FCSTD DOCUMENT  (FreeCAD 0.21R33668 +7 (Git))
Label: assembly
License: All rights reserved
LicenseURL: http://en.wikipedia.org/wiki/All_rights_reserved
objects: App::Link×21, App::DocumentObjectGroup×2, PartDesign::CoordinateSystem×1, App::FeaturePython×1, Sketcher::SketchObject×1, App::Part×1
note: 2 computed .brp shape members not serialized (recipe doc carries the construction recipe); baked Part::Feature solids carry a one-line shape summary decoded from their .brp
EXTERNAL_REF file=planB.FCStd obj=LCS_0
EXTERNAL_REF file=planB.FCStd obj=main
EXTERNAL_REF file=ES-holder-end.FCStd obj=LCS_0
EXTERNAL_REF file=ES-holder-end.FCStd obj=ES_holder
EXTERNAL_REF file=ES-holder.FCStd obj=LCS_0
EXTERNAL_REF file=ES-holder.FCStd obj=ES_holder
EXTERNAL_REF file=ES-holder-end-other.FCStd obj=LCS_0
EXTERNAL_REF file=ES-holder-end-other.FCStd obj=ES_holder
EXTERNAL_REF file=back-base.FCStd obj=LCS_0
EXTERNAL_REF file=back-base.FCStd obj=back_base
EXTERNAL_REF file=speakerbox.FCStd obj=LCS_0
EXTERNAL_REF file=speakerbox.FCStd obj=speakerbox
EXTERNAL_REF file=L-back.FCStd obj=LCS_0
EXTERNAL_REF file=L-back.FCStd obj=L_back
EXTERNAL_REF file=L-front.FCStd obj=LCS_0
EXTERNAL_REF file=L-front.FCStd obj=L_front
EXTERNAL_REF file=side_front_L.FCStd obj=LCS_0
EXTERNAL_REF file=side_front_L.FCStd obj=side_front_L
EXTERNAL_REF file=L-grip-1.FCStd obj=LCS_0
EXTERNAL_REF file=L-grip-1.FCStd obj=L_grip_1
EXTERNAL_REF file=speakerbox-L.FCStd obj=LCS_0
EXTERNAL_REF file=speakerbox-L.FCStd obj=speakerbox
EXTERNAL_REF file=side_front_R.FCStd obj=LCS_0
EXTERNAL_REF file=side_front_R.FCStd obj=side_front_L
EXTERNAL_REF file=planB.FCStd obj=Spreadsheet
EXTERNAL_REF file=leg1.FCStd obj=LCS_0
EXTERNAL_REF file=leg1.FCStd obj=leg1
EXTERNAL_REF file=speaker.FCStd obj=LCS_0
EXTERNAL_REF file=speaker.FCStd obj=speaker
EXTERNAL_REF file=speaker-enclosure-L.FCStd obj=LCS_0
EXTERNAL_REF file=speaker-enclosure-L.FCStd obj=enc_L
EXTERNAL_REF file=speaker-enclosure-R.FCStd obj=LCS_0
EXTERNAL_REF file=speaker-enclosure-R.FCStd obj=enc_L
EXTERNAL_REF file=speaker-enclosure-lid-R.FCStd obj=LCS_0
EXTERNAL_REF file=speaker-enclosure-lid-R.FCStd obj=enc_lid_L
EXTERNAL_REF file=speaker-enclosure-lid-L.FCStd obj=LCS_0
EXTERNAL_REF file=speaker-enclosure-lid-L.FCStd obj=enc_lid_L
EXTERNAL_REF file=volume knob.FCStd obj=LCS_0
EXTERNAL_REF file=volume knob.FCStd obj=knob

FEATURE [App::DocumentObjectGroup] Parts
FEATURE [PartDesign::CoordinateSystem] LCS_Origin
  AttacherType = Attacher::AttachEngine3D
  MapMode = 2
  Support = -> [X_Axis]
FEATURE [App::DocumentObjectGroup] Constraints
FEATURE [App::FeaturePython] Variables  # WARN: FeaturePython — macro-defined, semantics opaque (R4)
FEATURE [App::Link] planB_main
  AssemblyType = Asm4EE
  AttachedBy = #LCS_0
  AttachedTo = Parent Assembly#LCS_Origin
  LinkedObject = -> <external planB.FCStd>#main
  expr: Placement = LCS_Origin.Placement * AttachmentOffset * planB#LCS_0.Placement ^ -1
FEATURE [App::Link] ES_holder_ES_holder  label="ES_holder_end"
  AssemblyType = Asm4EE
  AttachedBy = #LCS_0
  AttachedTo = planB_main#LCS_0
  AttachmentOffset = pos=(87,5,484) rot=(0,0,1;0rad)
  LinkPlacement = pos=(87,5,484) rot=(0,0,1;0rad)
  LinkedObject = -> <external ES-holder-end.FCStd>#ES_holder
  Placement = pos=(87,5,484) rot=(0,0,1;0rad)
  expr: Placement = planB_main.Placement * planB#LCS_0.Placement * AttachmentOffset * ES_holder_end#LCS_0.Placement ^ -1
FEATURE [App::Link] ES_holder1_ES_holder
  AssemblyType = Asm4EE
  AttachedBy = #LCS_0
  AttachedTo = ES_holder_ES_holder#LCS_0
  AttachmentOffset = pos=(0,0,-133) rot=(0,0,1;0rad)
  LinkPlacement = pos=(87,5,351) rot=(0,0,1;0rad)
  LinkedObject = -> <external ES-holder.FCStd>#ES_holder
  Placement = pos=(87,5,351) rot=(0,0,1;0rad)
  expr: Placement = ES_holder_ES_holder.Placement * ES_holder_end#LCS_0.Placement * AttachmentOffset * ES_holder#LCS_0.Placement ^ -1
FEATURE [App::Link] ES_holder1_ES_holder_2
  AssemblyType = Asm4EE
  AttachedBy = #LCS_0
  AttachedTo = ES_holder1_ES_holder#LCS_0
  AttachmentOffset = pos=(0,0,-133) rot=(0,0,1;0rad)
  LinkPlacement = pos=(87,5,218) rot=(0,0,1;0rad)
  LinkedObject = -> <external ES-holder.FCStd>#ES_holder
  Placement = pos=(87,5,218) rot=(0,0,1;0rad)
  expr: Placement = ES_holder1_ES_holder.Placement * ES_holder#LCS_0.Placement * AttachmentOffset * ES_holder#LCS_0.Placement ^ -1
FEATURE [App::Link] ES_holder_ES_holder_otherend  label="ES_holder_ES_holder-otherend"
  AssemblyType = Asm4EE
  AttachedBy = #LCS_0
  AttachedTo = ES_holder1_ES_holder_2#LCS_0
  AttachmentOffset = pos=(0,0,-133) rot=(0,0,1;0rad)
  LinkPlacement = pos=(87,5,85) rot=(0,0,1;0rad)
  LinkedObject = -> <external ES-holder-end-other.FCStd>#ES_holder
  Placement = pos=(87,5,85) rot=(0,0,1;0rad)
  expr: Placement = ES_holder1_ES_holder_2.Placement * ES_holder#LCS_0.Placement * AttachmentOffset * ES_holder_end_other#LCS_0.Placement ^ -1
FEATURE [App::Link] back_base
  AssemblyType = Part::Link
  AttachedBy = #LCS_0
  AttachedTo = planB_main#LCS_0
  AttachmentOffset = pos=(0,0,0) rot=(1,0,0;4.71239rad)
  LinkPlacement = pos=(0,0,0) rot=(1,0,0;4.71239rad)
  LinkedObject = -> <external back-base.FCStd>#back_base
  Placement = pos=(0,0,0) rot=(1,0,0;4.71239rad)
  SolverId = Asm4EE
  expr: Placement = planB_main.Placement * planB#LCS_0.Placement * AttachmentOffset * back_base#LCS_0.Placement ^ -1
FEATURE [App::Link] speakerbox_speakerbox
  AssemblyType = Asm4EE
  AttachedBy = #LCS_0
  AttachedTo = planB_main#LCS_0
  AttachmentOffset = pos=(0,30,0) rot=(0,0,1;0rad)
  LinkPlacement = pos=(0,30,0) rot=(0,0,1;0rad)
  LinkedObject = -> <external speakerbox.FCStd>#speakerbox
  Placement = pos=(0,30,0) rot=(0,0,1;0rad)
  expr: Placement = planB_main.Placement * planB#LCS_0.Placement * AttachmentOffset * speakerbox#LCS_0.Placement ^ -1
FEATURE [App::Link] L_back_L_back
  AssemblyType = Asm4EE
  AttachedBy = #LCS_0
  AttachedTo = planB_main#LCS_0
  AttachmentOffset = pos=(6.4,99.1,5) rot=(0,0,1;0rad)
  LinkPlacement = pos=(6.4,99.1,5) rot=(0,0,1;0rad)
  LinkedObject = -> <external L-back.FCStd>#L_back
  Placement = pos=(6.4,99.1,5) rot=(0,0,1;0rad)
  expr: Placement = planB_main.Placement * planB#LCS_0.Placement * AttachmentOffset * L_back#LCS_0.Placement ^ -1
FEATURE [App::Link] L_front_L_front
  AssemblyType = Asm4EE
  AttachedBy = #LCS_0
  AttachedTo = planB_main#LCS_0
  AttachmentOffset = pos=(299.2,97,5) rot=(0,0,1;1.5708rad)
  LinkPlacement = pos=(299.2,97,5) rot=(0,0,1;1.5708rad)
  LinkedObject = -> <external L-front.FCStd>#L_front
  Placement = pos=(299.2,97,5) rot=(0,0,1;1.5708rad)
  expr: Placement = planB_main.Placement * planB#LCS_0.Placement * AttachmentOffset * L_front#LCS_0.Placement ^ -1
FEATURE [App::Link] side_front_L_side_front_L
  AssemblyType = Asm4EE
  AttachedBy = #LCS_0
  AttachedTo = planB_main#LCS_0
  AttachmentOffset = pos=(168.6,5,0) rot=(0,0,1;0rad)
  LinkPlacement = pos=(168.6,5,0) rot=(0,0,1;0rad)
  LinkedObject = -> <external side_front_L.FCStd>#side_front_L
  Placement = pos=(168.6,5,0) rot=(0,0,1;0rad)
  expr: Placement = planB_main.Placement * planB#LCS_0.Placement * AttachmentOffset * side_front_L#LCS_0.Placement ^ -1
FEATURE [App::Link] L_grip_1_L_grip_1
  AssemblyType = Asm4EE
  AttachedBy = #LCS_0
  AttachedTo = L_front_L_front#LCS_0
  AttachmentOffset = pos=(-0.4,-0.4,491) rot=(0,0,1;0rad)
  LinkPlacement = pos=(299.6,96.6,496) rot=(0,0,1;1.5708rad)
  LinkedObject = -> <external L-grip-1.FCStd>#L_grip_1
  Placement = pos=(299.6,96.6,496) rot=(0,0,1;1.5708rad)
  expr: Placement = L_front_L_front.Placement * L_front#LCS_0.Placement * AttachmentOffset * L_grip_1#LCS_0.Placement ^ -1
FEATURE [App::Link] L_grip_1_L_grip_2
  AssemblyType = Asm4EE
  AttachedBy = #LCS_0
  AttachedTo = L_back_L_back#LCS_0
  AttachmentOffset = pos=(0,0,491) rot=(0,0,1;0rad)
  LinkPlacement = pos=(6.4,99.1,496) rot=(0,0,1;0rad)
  LinkedObject = -> <external L-grip-1.FCStd>#L_grip_1
  Placement = pos=(6.4,99.1,496) rot=(0,0,1;0rad)
  expr: Placement = L_back_L_back.Placement * L_back#LCS_0.Placement * AttachmentOffset * L_grip_1#LCS_0.Placement ^ -1
FEATURE [App::Link] speakerbox_L_speakerbox_L  label="speakerbox_L_speakerbox-L"
  AssemblyType = Asm4EE
  AttachedBy = #LCS_0
  AttachedTo = planB_main#LCS_0
  AttachmentOffset = pos=(0,30,440) rot=(0,0,1;0rad)
  LinkPlacement = pos=(0,30,440) rot=(0,0,1;0rad)
  LinkedObject = -> <external speakerbox-L.FCStd>#speakerbox
  Placement = pos=(0,30,440) rot=(0,0,1;0rad)
  expr: Placement = planB_main.Placement * planB#LCS_0.Placement * AttachmentOffset * speakerbox_L#LCS_0.Placement ^ -1
FEATURE [App::Link] side_front_R_side_front_L
  AssemblyType = Asm4EE
  AttachedBy = #LCS_0
  AttachedTo = planB_main#LCS_0
  AttachmentOffset = pos=(169,5,484) rot=(0,0,1;0rad)
  LinkPlacement = pos=(169,5,484) rot=(0,0,1;0rad)
  LinkedObject = -> <external side_front_R.FCStd>#side_front_L
  Placement = pos=(169,5,484) rot=(0,0,1;0rad)
  expr: Placement = planB_main.Placement * planB#LCS_0.Placement * AttachmentOffset * side_front_R#LCS_0.Placement ^ -1
FEATURE [Sketcher::SketchObject] Sketch003
  FullyConstrained = false
  MapMode = 5
  Support = -> [XY_Plane]
  expr: Constraints[1] = planB#<<data>>.clearance_m3
  sketch-geometry (38):
    g0: Circle CenterX=3.5 CenterY=-246.571 CenterZ=0 NormalX=0 NormalY=0 NormalZ=1 AngleXU=0 Radius=1.75
    g1: Circle CenterX=3.5 CenterY=-253.429 CenterZ=0 NormalX=0 NormalY=0 NormalZ=1 AngleXU=0 Radius=1.75
    g2: LineSegment StartX=3.5 StartY=-246.571 StartZ=0 EndX=3.5 EndY=-253.429 EndZ=0
    g3: GeomPoint X=3.5 Y=-250 Z=0
    g4: LineSegment StartX=227.2 StartY=-93 StartZ=0 EndX=227.2 EndY=-492 EndZ=0
    g5: LineSegment StartX=227.2 StartY=-93 StartZ=0 EndX=99 EndY=-93 EndZ=0
    g6: LineSegment StartX=99 StartY=-93 StartZ=0 EndX=99 EndY=-492 EndZ=0
    g7: LineSegment StartX=176.6 StartY=-93 StartZ=0 EndX=176.6 EndY=-492 EndZ=0
    g8: LineSegment StartX=144.6 StartY=-93 StartZ=0 EndX=144.6 EndY=-492 EndZ=0
    g9: LineSegment StartX=99 StartY=-492 StartZ=0 EndX=227.2 EndY=-492 EndZ=0
    g10: LineSegment StartX=227.2 StartY=-226 StartZ=0 EndX=99 EndY=-226 EndZ=0
    g11: LineSegment StartX=99 StartY=-359 StartZ=0 EndX=227.2 EndY=-359 EndZ=0
    g12: LineSegment StartX=99 StartY=-492 StartZ=0 EndX=12 EndY=-492 EndZ=0
    g13: LineSegment StartX=70 StartY=-492 StartZ=0 EndX=70 EndY=-8 EndZ=0
    g14: LineSegment StartX=227.2 StartY=-93 StartZ=0 EndX=227.2 EndY=-8 EndZ=0
    g15: LineSegment StartX=227.2 StartY=-8 StartZ=0 EndX=12 EndY=-8 EndZ=0
    g16: LineSegment StartX=12 StartY=-8 StartZ=0 EndX=12 EndY=-492 EndZ=0
    g17: Circle CenterX=227.2 CenterY=-492 CenterZ=0 NormalX=0 NormalY=0 NormalZ=1 AngleXU=0 Radius=3.6145
    g18: Circle CenterX=176.6 CenterY=-492 CenterZ=0 NormalX=0 NormalY=0 NormalZ=1 AngleXU=0 Radius=3.6145
    g19: Circle CenterX=144.6 CenterY=-492 CenterZ=0 NormalX=0 NormalY=0 NormalZ=1 AngleXU=0 Radius=3.6145
    g20: Circle CenterX=99 CenterY=-492 CenterZ=0 NormalX=0 NormalY=0 NormalZ=1 AngleXU=0 Radius=3.6145
    g21: Circle CenterX=70 CenterY=-492 CenterZ=0 NormalX=0 NormalY=0 NormalZ=1 AngleXU=0 Radius=3.6145
    g22: Circle CenterX=12 CenterY=-492 CenterZ=0 NormalX=0 NormalY=0 NormalZ=1 AngleXU=0 Radius=3.6145
    g23: Circle CenterX=99 CenterY=-359 CenterZ=0 NormalX=0 NormalY=0 NormalZ=1 AngleXU=0 Radius=3.6145
    g24: Circle CenterX=144.6 CenterY=-359 CenterZ=0 NormalX=0 NormalY=0 NormalZ=1 AngleXU=0 Radius=3.6145
    g25: Circle CenterX=176.6 CenterY=-359 CenterZ=0 NormalX=0 NormalY=0 NormalZ=1 AngleXU=0 Radius=3.6145
    g26: Circle CenterX=227.2 CenterY=-359 CenterZ=0 NormalX=0 NormalY=0 NormalZ=1 AngleXU=0 Radius=3.6145
    g27: Circle CenterX=227.2 CenterY=-226 CenterZ=0 NormalX=0 NormalY=0 NormalZ=1 AngleXU=0 Radius=3.6145
    g28: Circle CenterX=99 CenterY=-226 CenterZ=0 NormalX=0 NormalY=0 NormalZ=1 AngleXU=0 Radius=3.6145
    g29: Circle CenterX=144.6 CenterY=-226 CenterZ=0 NormalX=0 NormalY=0 NormalZ=1 AngleXU=0 Radius=3.6145
    g30: Circle CenterX=176.6 CenterY=-226 CenterZ=0 NormalX=0 NormalY=0 NormalZ=1 AngleXU=0 Radius=3.6145
    g31: Circle CenterX=176.6 CenterY=-93 CenterZ=0 NormalX=0 NormalY=0 NormalZ=1 AngleXU=0 Radius=3.6145
    g32: Circle CenterX=144.6 CenterY=-93 CenterZ=0 NormalX=0 NormalY=0 NormalZ=1 AngleXU=0 Radius=3.6145
    g33: Circle CenterX=99 CenterY=-93 CenterZ=0 NormalX=0 NormalY=0 NormalZ=1 AngleXU=0 Radius=3.6145
    g34: Circle CenterX=227.2 CenterY=-93 CenterZ=0 NormalX=0 NormalY=0 NormalZ=1 AngleXU=0 Radius=3.6145
    g35: Circle CenterX=227.2 CenterY=-8 CenterZ=0 NormalX=0 NormalY=0 NormalZ=1 AngleXU=0 Radius=3.6145
    g36: Circle CenterX=70 CenterY=-8 CenterZ=0 NormalX=0 NormalY=0 NormalZ=1 AngleXU=0 Radius=3.6145
    g37: Circle CenterX=12 CenterY=-8 CenterZ=0 NormalX=0 NormalY=0 NormalZ=1 AngleXU=0 Radius=3.6145
  constraints (96):
    c: Equal(g1,g0)
    c: Diameter(g0) = 3.5
    c: Coincident(g2,g0)
    c: Coincident(g2,g1)
    c: Vertical(g2)
    c: Symmetric(g1,g0,g3)
    c: DistanceX(g3) = 3.5
    c: DistanceY(g3) = -250
    c: Vertical(g4)
    c: Coincident(g5,g4)
    c: Horizontal(g5)
    c: Coincident(g6,g5)
    c: Vertical(g6)
    c: PointOnObject(g7,g5)
    c: Vertical(g7)
    c: PointOnObject(g8,g5)
    c: Vertical(g8)
    c: Coincident(g9,g6)
    c: Coincident(g9,g4)
    c: Horizontal(g9)
    c: PointOnObject(g7,g9)
    c: PointOnObject(g8,g9)
    c: PointOnObject(g10,g4)
    c: PointOnObject(g10,g6)
    c: Horizontal(g10)
    c: PointOnObject(g11,g6)
    c: PointOnObject(g11,g4)
    c: Horizontal(g11)
    c: Distance(g11,g9) = 133
    c: Distance(g11,g10) = 133
    c: Distance(g10,g5) = 133
    c: DistanceX(g4) = 227.2
    c: DistanceY(g4) = -93
    c: DistanceX(g7) = 176.6
    c: DistanceX(g8) = 144.6
    c: DistanceX(g5) = 99
    c: Horizontal(g12)
    c: PointOnObject(g13,g12)
    c: Vertical(g13)
    c: Vertical(g14)
    c: Coincident(g4,g14)
    c: Horizontal(g15)
    c: Vertical(g16)
    c: Coincident(g12,g16)
    c: Coincident(g15,g16)
    c: PointOnObject(g13,g15)
    c: Coincident(g15,g14)
    c: DistanceY(g14) = -8
    c: DistanceX(g15) = 12
    c: DistanceX(g13) = 70
    c: Coincident(g12,g6)
    c: Coincident(g17,g4)
    c: Coincident(g18,g7)
    c: Coincident(g19,g8)
    c: Coincident(g20,g6)
    c: Coincident(g21,g13)
    c: Coincident(g22,g12)
    c: Coincident(g23,g11)
    c: PointOnObject(g24,g8)
    c: PointOnObject(g25,g7)
    c: Coincident(g26,g11)
    c: Coincident(g27,g10)
    c: Coincident(g28,g10)
    c: PointOnObject(g29,g8)
    c: PointOnObject(g30,g7)
    c: Coincident(g31,g7)
    c: Coincident(g32,g8)
    c: Coincident(g33,g5)
    c: Coincident(g34,g4)
    c: Coincident(g35,g14)
    c: Coincident(g36,g13)
    c: Coincident(g37,g15)
    c: Equal(g35,g36)
    c: Equal(g36,g37)
    c: Equal(g37,g33)
    c: Equal(g33,g32)
    c: Equal(g32,g31)
    c: Equal(g31,g34)
    c: Equal(g34,g27)
    c: Equal(g27,g28)
    c: Equal(g28,g29)
    c: Equal(g29,g30)
    c: Equal(g30,g26)
    c: Equal(g26,g25)
    c: Equal(g25,g24)
    c: Equal(g24,g23)
    c: Equal(g23,g17)
    c: Equal(g17,g18)
    c: Equal(g18,g19)
    c: Equal(g19,g20)
    c: Equal(g20,g21)
    c: Equal(g21,g22)
    c: PointOnObject(g25,g11)
    c: PointOnObject(g24,g11)
    c: PointOnObject(g29,g10)
    c: PointOnObject(g30,g10)
FEATURE [App::Link] leg1_leg1
  AssemblyType = Asm4EE
  AttachedBy = #LCS_0
  AttachedTo = planB_main#LCS_0
  AttachmentOffset = pos=(82,12.5,30) rot=(0.707107,0,0.707107;3.14159rad)
  LinkPlacement = pos=(82,12.5,30) rot=(0.707107,0,0.707107;3.14159rad)
  LinkedObject = -> <external leg1.FCStd>#leg1
  Placement = pos=(82,12.5,30) rot=(0.707107,0,0.707107;3.14159rad)
  expr: Placement = planB_main.Placement * planB#LCS_0.Placement * AttachmentOffset * leg1#LCS_0.Placement ^ -1
FEATURE [App::Link] speaker_speaker
  AssemblyType = Asm4EE
  AttachedBy = #LCS_0
  AttachedTo = speakerbox_L_speakerbox_L#LCS_0
  AttachmentOffset = pos=(107,87,27.5) rot=(0.57735,-0.57735,0.57735;2.0944rad)
  LinkPlacement = pos=(107,117,467.5) rot=(0.57735,-0.57735,0.57735;2.0944rad)
  LinkedObject = -> <external speaker.FCStd>#speaker
  Placement = pos=(107,117,467.5) rot=(0.57735,-0.57735,0.57735;2.0944rad)
  expr: Placement = speakerbox_L_speakerbox_L.Placement * speakerbox_L#LCS_0.Placement * AttachmentOffset * speaker#LCS_0.Placement ^ -1
FEATURE [App::Link] speaker_enclosure_L_enc_L
  AssemblyType = Asm4EE
  AttachedBy = #LCS_0
  AttachedTo = speakerbox_L_speakerbox_L#LCS_0
  AttachmentOffset = pos=(147.3,93,0) rot=(0.57735,-0.57735,0.57735;2.0944rad)
  LinkPlacement = pos=(147.3,123,440) rot=(0.57735,-0.57735,0.57735;2.0944rad)
  LinkedObject = -> <external speaker-enclosure-L.FCStd>#enc_L
  Placement = pos=(147.3,123,440) rot=(0.57735,-0.57735,0.57735;2.0944rad)
  expr: Placement = speakerbox_L_speakerbox_L.Placement * speakerbox_L#LCS_0.Placement * AttachmentOffset * speaker_enclosure_L#LCS_0.Placement ^ -1
FEATURE [App::Link] speaker_enclosure_R_enc_R
  AssemblyType = Asm4EE
  AttachedBy = #LCS_0
  AttachedTo = speakerbox_speakerbox#LCS_0
  AttachmentOffset = pos=(147.3,94,5) rot=(0.57735,-0.57735,0.57735;2.0944rad)
  LinkPlacement = pos=(147.3,124,5) rot=(0.57735,-0.57735,0.57735;2.0944rad)
  LinkedObject = -> <external speaker-enclosure-R.FCStd>#enc_L
  Placement = pos=(147.3,124,5) rot=(0.57735,-0.57735,0.57735;2.0944rad)
  expr: Placement = speakerbox_speakerbox.Placement * speakerbox#LCS_0.Placement * AttachmentOffset * speaker_enclosure_R#LCS_0.Placement ^ -1
FEATURE [App::Link] speaker_enclosure_lid_L_enc_lid_R
  AssemblyType = Asm4EE
  AttachedBy = #LCS_0
  AttachedTo = speaker_enclosure_R_enc_R#LCS_0
  LinkPlacement = pos=(147.3,124,5) rot=(0.57735,-0.57735,0.57735;2.0944rad)
  LinkedObject = -> <external speaker-enclosure-lid-R.FCStd>#enc_lid_L
  Placement = pos=(147.3,124,5) rot=(0.57735,-0.57735,0.57735;2.0944rad)
  expr: Placement = speaker_enclosure_R_enc_R.Placement * speaker_enclosure_R#LCS_0.Placement * AttachmentOffset * speaker_enclosure_lid_R#LCS_0.Placement ^ -1
FEATURE [App::Link] speaker_enclosure_lid_L1_enc_lid__L
  AssemblyType = Asm4EE
  AttachedBy = #LCS_0
  AttachedTo = speaker_enclosure_L_enc_L#LCS_0
  LinkPlacement = pos=(147.3,123,440) rot=(0.57735,-0.57735,0.57735;2.0944rad)
  LinkedObject = -> <external speaker-enclosure-lid-L.FCStd>#enc_lid_L
  Placement = pos=(147.3,123,440) rot=(0.57735,-0.57735,0.57735;2.0944rad)
  expr: Placement = speaker_enclosure_L_enc_L.Placement * speaker_enclosure_L#LCS_0.Placement * AttachmentOffset * speaker_enclosure_lid_L#LCS_0.Placement ^ -1
FEATURE [App::Link] volume_knob_knob001
  AssemblyType = Asm4EE
  AttachedBy = #LCS_0
  AttachedTo = speaker_enclosure_lid_L1_enc_lid__L#LCS_0
  AttachmentOffset = pos=(27.5,112.3,0) rot=(0,0,1;0rad)
  LinkPlacement = pos=(35,123,467.5) rot=(0.57735,-0.57735,0.57735;2.0944rad)
  LinkedObject = -> <external volume knob.FCStd>#knob
  Placement = pos=(35,123,467.5) rot=(0.57735,-0.57735,0.57735;2.0944rad)
  expr: Placement = speaker_enclosure_lid_L1_enc_lid__L.Placement * speaker_enclosure_lid_L#LCS_0.Placement * AttachmentOffset * volume_knob#LCS_0.Placement ^ -1
FEATURE [App::Part] Model
  Configuration = 0
  Group = -> [LCS_Origin,Constraints,Variables,planB_main,ES_holder_ES_holder,ES_holder1_ES_holder,ES_holder1_ES_holder_2,ES_holder_ES_holder_otherend,back_base,speakerbox_speakerbox,L_back_L_back,L_front_L_front,side_front_L_side_front_L,L_grip_1_L_grip_1,L_grip_1_L_grip_2,speakerbox_L_speakerbox_L,side_front_R_side_front_L,leg1_leg1,speaker_speaker,speaker_enclosure_L_enc_L,speaker_enclosure_R_enc_R,+3 more]
  Origin = -> Origin
  Type = Assembly4 Model

RESOLVED EXTERNAL PARTS (link-assembly join: the EXTERNAL_REF files above that resolve inside this repo's crawl, each included once):
---- part ES-holder-end-other.FCStd = doc fcstd_7b380cd65d5b ----
FCSTD DOCUMENT  (FreeCAD 0.21R33668 +7 (Git))
Label: ES-holder-end-other
License: All rights reserved
LicenseURL: http://en.wikipedia.org/wiki/All_rights_reserved
objects: Sketcher::SketchObject×7, PartDesign::Pocket×4, PartDesign::Pad×3, PartDesign::CoordinateSystem×1, PartDesign::Plane×1, PartDesign::Chamfer×1, PartDesign::Body×1, App::Part×1
note: 26 computed .brp shape members not serialized (recipe doc carries the construction recipe); baked Part::Feature solids carry a one-line shape summary decoded from their .brp
EXTERNAL_REF file=planB.FCStd obj=Spreadsheet

FEATURE [Sketcher::SketchObject] Sketch
  FullyConstrained = false
  MapMode = 5
  Support = -> [XY_Plane]
  expr: Constraints[33] = <<planB>>#<<data>>.es3_d + 1
  expr: Constraints[34] = <<planB>>#<<data>>.es6_d
  sketch-geometry (19):
    g0: LineSegment StartX=0 StartY=0 StartZ=0 EndX=0 EndY=43 EndZ=0
    g1: LineSegment StartX=152.2 StartY=31 StartZ=0 EndX=152.2 EndY=0 EndZ=0
    g2: LineSegment StartX=152.2 StartY=0 StartZ=0 EndX=0 EndY=0 EndZ=0
    g3: LineSegment StartX=22.6 StartY=-1.74507e-05 StartZ=0 EndX=20 EndY=-1.74507e-05 EndZ=0
    g4: LineSegment StartX=20 StartY=-1.74507e-05 StartZ=0 EndX=20 EndY=43 EndZ=0
    g5: LineSegment StartX=20 StartY=43 StartZ=0 EndX=22.6 EndY=43 EndZ=0
    g6: LineSegment StartX=22.6 StartY=43 StartZ=0 EndX=22.6 EndY=-1.74507e-05 EndZ=0
    g7: LineSegment StartX=132.2 StartY=0 StartZ=0 EndX=129.6 EndY=0 EndZ=0
    g8: LineSegment StartX=129.6 StartY=0 StartZ=0 EndX=129.6 EndY=31 EndZ=0
    g9: LineSegment StartX=129.6 StartY=31 StartZ=0 EndX=132.2 EndY=31 EndZ=0
    g10: LineSegment StartX=132.2 StartY=31 StartZ=0 EndX=132.2 EndY=0 EndZ=0
    g11: LineSegment StartX=76.6 StartY=43 StartZ=0 EndX=76.6 EndY=31 EndZ=0
    g12: LineSegment StartX=76.6 StartY=31 StartZ=0 EndX=152.2 EndY=31 EndZ=0
    g13: LineSegment StartX=27.6 StartY=43 StartZ=0 EndX=27.6 EndY=28 EndZ=0
    g14: LineSegment StartX=27.6 StartY=28 StartZ=0 EndX=47.6 EndY=28 EndZ=0
    g15: LineSegment StartX=47.6 StartY=28 StartZ=0 EndX=47.6 EndY=43 EndZ=0
    g16: LineSegment StartX=0 StartY=43 StartZ=0 EndX=27.6 EndY=43 EndZ=0
    g17: LineSegment StartX=27.6 StartY=43 StartZ=0 EndX=47.6 EndY=43 EndZ=0
    g18: LineSegment StartX=47.6 StartY=43 StartZ=0 EndX=76.6 EndY=43 EndZ=0
  constraints (54):
    c: Coincident(g-1,g0)
    c: PointOnObject(g0,g-2)
    c: Coincident(g0,g16)
    c: Coincident(g12,g1)
    c: PointOnObject(g1,g-1)
    c: Vertical(g1)
    c: Coincident(g1,g2)
    c: Coincident(g3,g4)
    c: Coincident(g4,g5)
    c: Coincident(g5,g6)
    c: Coincident(g6,g3)
    c: Horizontal(g3)
    c: Horizontal(g5)
    c: Vertical(g4)
    c: Vertical(g6)
    c: Coincident(g7,g8)
    c: Coincident(g8,g9)
    c: Coincident(g9,g10)
    c: Coincident(g10,g7)
    c: Horizontal(g7)
    c: Horizontal(g9)
    c: Vertical(g8)
    c: Vertical(g10)
    c: PointOnObject(g7,g2)
    c: Equal(g3,g7)
    c: Distance(g3,g4) = 2.6
    c: Coincident(g18,g11)
    c: Coincident(g11,g12)
    c: Horizontal(g12)
    c: PointOnObject(g8,g12)
    c: Vertical(g11)
    c: Distance(g0) = 43
    c: Distance(g1) = 31
    c: Distance(g5,g11) = 54
    c: Distance(g11,g8) = 53
    c: Distance(g7,g1) = 20
    c: Distance(g3,g0) = 20
    c: Coincident(g2,g0)
    c: Coincident(g13,g14)
    c: Horizontal(g14)
    c: Coincident(g14,g15)
    c: Vertical(g15)
    c: Coincident(g16,g17)
    c: Horizontal(g16)
    c: PointOnObject(g4,g16)
    c: Coincident(g17,g18)
    c: Horizontal(g17)
    c: Horizontal(g18)
    c: Coincident(g17,g15)
    c: Coincident(g16,g13)
    c: Vertical(g13)
    c: Distance(g13) = 15
    c: Distance(g14) = 20
    c: Distance(g5,g13) = 5
FEATURE [PartDesign::Pad] Pad
  Direction = (0,0,1)
  Length = 16
  Length2 = 10
  Profile = -> Sketch
  ReferenceAxis = -> Sketch [N_Axis]
  Type = 0
FEATURE [Sketcher::SketchObject] Sketch001
  FullyConstrained = false
  MapMode = 5
  Placement = pos=(0,0,0) rot=(1,0,0;1.5708rad)
  Support = -> [XZ_Plane]
  expr: Constraints[52] = <<planB>>#<<data>>.es6_d + 1 + <<planB>>#<<data>>.es3_d
  expr: Constraints[60] = <<planB>>#<<data>>.insert_diameter
  expr: Constraints[61] = <<planB>>#<<data>>.insert_d + 5
  sketch-geometry (27):
    g0: LineSegment StartX=20 StartY=0 StartZ=0 EndX=20 EndY=17.2745 EndZ=0
    g1: LineSegment StartX=132.2 StartY=0 StartZ=0 EndX=132.2 EndY=26.3444 EndZ=0
    g2: LineSegment StartX=20 StartY=0 StartZ=0 EndX=22.6 EndY=0 EndZ=0
    g3: LineSegment StartX=22.6 StartY=0 StartZ=0 EndX=22.6 EndY=6 EndZ=0
    g4: LineSegment StartX=22.6 StartY=6 StartZ=0 EndX=20 EndY=6 EndZ=0
    g5: LineSegment StartX=20 StartY=6 StartZ=0 EndX=20 EndY=0 EndZ=0
    g6: LineSegment StartX=20 StartY=10 StartZ=0 EndX=22.6 EndY=10 EndZ=0
    g7: LineSegment StartX=22.6 StartY=10 StartZ=0 EndX=22.6 EndY=16 EndZ=0
    g8: LineSegment StartX=22.6 StartY=16 StartZ=0 EndX=20 EndY=16 EndZ=0
    g9: LineSegment StartX=20 StartY=16 StartZ=0 EndX=20 EndY=10 EndZ=0
    g10: LineSegment StartX=132.2 StartY=10 StartZ=0 EndX=129.6 EndY=10 EndZ=0
    g11: LineSegment StartX=129.6 StartY=10 StartZ=0 EndX=129.6 EndY=16 EndZ=0
    g12: LineSegment StartX=129.6 StartY=16 StartZ=0 EndX=132.2 EndY=16 EndZ=0
    g13: LineSegment StartX=132.2 StartY=16 StartZ=0 EndX=132.2 EndY=10 EndZ=0
    g14: LineSegment StartX=132.2 StartY=6 StartZ=0 EndX=129.6 EndY=6 EndZ=0
    g15: LineSegment StartX=129.6 StartY=6 StartZ=0 EndX=129.6 EndY=0 EndZ=0
    g16: LineSegment StartX=129.6 StartY=0 StartZ=0 EndX=132.2 EndY=0 EndZ=0
    g17: LineSegment StartX=132.2 StartY=0 StartZ=0 EndX=132.2 EndY=6 EndZ=0
    g18: Circle CenterX=12 CenterY=8 CenterZ=0 NormalX=0 NormalY=0 NormalZ=1 AngleXU=0 Radius=2.15
    g19: Circle CenterX=89.6 CenterY=8 CenterZ=0 NormalX=0 NormalY=0 NormalZ=1 AngleXU=0 Radius=2.15
    g20: Circle CenterX=140.2 CenterY=8 CenterZ=0 NormalX=0 NormalY=0 NormalZ=1 AngleXU=0 Radius=2.15
    g21: LineSegment StartX=12 StartY=8 StartZ=0 EndX=140.2 EndY=8 EndZ=0
    g22: Circle CenterX=57.6 CenterY=8 CenterZ=0 NormalX=0 NormalY=0 NormalZ=1 AngleXU=0 Radius=2.15
    g23: Circle CenterX=12 CenterY=-77 CenterZ=0 NormalX=0 NormalY=0 NormalZ=1 AngleXU=0 Radius=2.15
    g24: Circle CenterX=140.2 CenterY=-77 CenterZ=0 NormalX=0 NormalY=0 NormalZ=1 AngleXU=0 Radius=2.15
    g25: LineSegment StartX=12 StartY=-77 StartZ=0 EndX=140.2 EndY=-77 EndZ=0
    g26: LineSegment StartX=12 StartY=8 StartZ=0 EndX=12 EndY=-77 EndZ=0
  constraints (77):
    c: PointOnObject(g0,g-1)
    c: Vertical(g0)
    c: PointOnObject(g1,g-1)
    c: Vertical(g1)
    c: DistanceX(g0) = 20
    c: Coincident(g2,g3)
    c: Coincident(g3,g4)
    c: Coincident(g4,g5)
    c: Coincident(g5,g2)
    c: Horizontal(g2)
    c: Horizontal(g4)
    c: Vertical(g3)
    c: Vertical(g5)
    c: Coincident(g2,g0)
    c: Coincident(g6,g7)
    c: Coincident(g7,g8)
    c: Coincident(g8,g9)
    c: Coincident(g9,g6)
    c: Horizontal(g6)
    c: Horizontal(g8)
    c: Vertical(g7)
    c: Vertical(g9)
    c: PointOnObject(g6,g0)
    c: Coincident(g10,g11)
    c: Coincident(g11,g12)
    c: Coincident(g12,g13)
    c: Coincident(g13,g10)
    c: Horizontal(g10)
    c: Horizontal(g12)
    c: Vertical(g11)
    c: Vertical(g13)
    c: PointOnObject(g10,g1)
    c: Coincident(g14,g15)
    c: Coincident(g15,g16)
    c: Coincident(g16,g17)
    c: Coincident(g17,g14)
    c: Horizontal(g14)
    c: Horizontal(g16)
    c: Vertical(g15)
    c: Vertical(g17)
    c: PointOnObject(g14,g1)
    c: PointOnObject(g15,g-1)
    c: Equal(g2,g16)
    c: Equal(g16,g10)
    c: Equal(g10,g8)
    c: Equal(g3,g7)
    c: Equal(g7,g11)
    c: Equal(g11,g15)
    c: Distance(g16) = 2.6
    c: Distance(g11) = 6
    c: Distance(g14,g10) = 4
    c: Distance(g4,g6) = 4
    c: Distance(g7,g11) = 107
    c: Coincident(g21,g18)
    c: Coincident(g21,g20)
    c: Horizontal(g21)
    c: PointOnObject(g19,g21)
    c: Equal(g20,g19)
    c: Equal(g19,g18)
    c: DistanceY(g18) = 8
    c: Diameter(g18) = 4.3
    c: DistanceX(g18) = 12
    c: PointOnObject(g22,g21)
    c: Equal(g22,g19)
    c: Distance(g22,g3) = 35
    c: Distance(g19,g11) = 40
    c: Distance(g20,g13) = 8
    c: Equal(g24,g23)
    c: Equal(g23,g22)
    c: Coincident(g25,g23)
    c: Coincident(g25,g24)
    c: Horizontal(g25)
    c: Equal(g21,g25)
    c: Coincident(g26,g18)
    c: Coincident(g26,g23)
    c: Vertical(g26)
    c: Distance(g26) = 85
FEATURE [PartDesign::CoordinateSystem] LCS_0
  AttacherType = Attacher::AttachEngine3D
  MapMode = 2
  Support = -> [X_Axis001]
FEATURE [Sketcher::SketchObject] Sketch002
  FullyConstrained = true
  MapMode = 5
  Placement = pos=(0,0,0) rot=(0.57735,0.57735,0.57735;2.0944rad)
  Support = -> [YZ_Plane]
  expr: Constraints[0] = <<planB>>#<<data>>.insert_d + 5
  expr: Constraints[2] = <<planB>>#<<data>>.insert_diameter
  sketch-geometry (1):
    g0: Circle CenterX=12 CenterY=8 CenterZ=0 NormalX=0 NormalY=0 NormalZ=1 AngleXU=0 Radius=2.15
  constraints (3):
    c: DistanceX(g0) = 12
    c: DistanceY(g0) = 8
    c: Diameter(g0) = 4.3
FEATURE [PartDesign::Pocket] Pocket001
  BaseFeature = -> Pad
  Direction = (-1,2e-16,-3e-16)
  Length = 8
  Length2 = 5
  Profile = -> Sketch002
  ReferenceAxis = -> Sketch002 [N_Axis]
  Reversed = true
  Type = 0
  expr: Length = <<planB>>#<<data>>.insert_d + 1
FEATURE [PartDesign::Plane] DatumPlane
  AttachmentOffset = pos=(0,0,152.2) rot=(0,0,1;0rad)
  Length = 60
  MapMode = 5
  Placement = pos=(152.2,-3.38e-14,3.38e-14) rot=(0.57735,0.57735,0.57735;2.0944rad)
  ResizeMode = 0
  Support = -> [YZ_Plane]
  Width = 60
FEATURE [Sketcher::SketchObject] Sketch003
  FullyConstrained = true
  MapMode = 5
  Placement = pos=(152.2,-3.38e-14,3.38e-14) rot=(0.57735,0.57735,0.57735;2.0944rad)
  Support = -> [DatumPlane]
  expr: Constraints[0] = <<planB>>#<<data>>.insert_diameter
  expr: Constraints[1] = <<planB>>#<<data>>.insert_d + 5
  sketch-geometry (1):
    g0: Circle CenterX=12 CenterY=8 CenterZ=0 NormalX=0 NormalY=0 NormalZ=1 AngleXU=0 Radius=2.15
  constraints (3):
    c: Diameter(g0) = 4.3
    c: DistanceX(g0) = 12
    c: DistanceY(g0) = 8
FEATURE [PartDesign::Pocket] Pocket002
  BaseFeature = -> Pocket001
  Direction = (-1,1e-16,-1e-16)
  Length = 8
  Length2 = 5
  Profile = -> Sketch003
  ReferenceAxis = -> Sketch003 [N_Axis]
  Type = 0
  expr: Length = <<planB>>#<<data>>.insert_d + 1
FEATURE [Sketcher::SketchObject] Sketch004
  FullyConstrained = false
  MapMode = 5
  Placement = pos=(0,0,0) rot=(1,0,0;1.5708rad)
  Support = -> [XZ_Plane]
  sketch-geometry (25):
    g0: LineSegment StartX=128 StartY=0 StartZ=0 EndX=152.2 EndY=0 EndZ=0
    g1: LineSegment StartX=128 StartY=-65 StartZ=0 EndX=128 EndY=0 EndZ=0
    g2: LineSegment StartX=0 StartY=0 StartZ=0 EndX=12 EndY=0 EndZ=0
    g3: LineSegment StartX=12 StartY=0 StartZ=0 EndX=12 EndY=-65 EndZ=0
    g4: LineSegment StartX=0 StartY=-65 StartZ=0 EndX=0 EndY=0 EndZ=0
    g5: LineSegment StartX=0 StartY=-65 StartZ=0 EndX=0 EndY=-85 EndZ=0
    g6: LineSegment StartX=0 StartY=-85 StartZ=0 EndX=12 EndY=-85 EndZ=0
    g7: LineSegment StartX=12 StartY=-85 StartZ=0 EndX=12 EndY=-68 EndZ=0
    g8: LineSegment StartX=12 StartY=-68 StartZ=0 EndX=5.5 EndY=-68 EndZ=0
    g9: LineSegment StartX=5.5 StartY=-68 StartZ=0 EndX=5.5 EndY=-65 EndZ=0
    g10: LineSegment StartX=134.5 StartY=-65 StartZ=0 EndX=134.5 EndY=-68 EndZ=0
    g11: LineSegment StartX=134.5 StartY=-68 StartZ=0 EndX=128 EndY=-68 EndZ=0
    g12: LineSegment StartX=128 StartY=-68 StartZ=0 EndX=128 EndY=-85 EndZ=0
    g13: LineSegment StartX=128 StartY=-85 StartZ=0 EndX=152.2 EndY=-85 EndZ=0
    g14: LineSegment StartX=152.2 StartY=-85 StartZ=0 EndX=152.2 EndY=-69 EndZ=0
    g15: LineSegment StartX=12 StartY=-65 StartZ=0 EndX=5.5 EndY=-65 EndZ=0
    g16: LineSegment StartX=5.5 StartY=-65 StartZ=0 EndX=0 EndY=-65 EndZ=0
    g17: LineSegment StartX=134.5 StartY=-65 StartZ=0 EndX=128 EndY=-65 EndZ=0
    g18: LineSegment StartX=152.2 StartY=0 StartZ=0 EndX=152.2 EndY=-5 EndZ=0
    g19: LineSegment StartX=152.2 StartY=-5 StartZ=0 EndX=152.2 EndY=-69 EndZ=0
    g20: LineSegment StartX=152.2 StartY=-5 StartZ=0 EndX=133 EndY=-5 EndZ=0
    g21: LineSegment StartX=133 StartY=-5 StartZ=0 EndX=133 EndY=-60 EndZ=0
    g22: LineSegment StartX=133 StartY=-60 StartZ=0 EndX=139.92 EndY=-60 EndZ=0
    g23: LineSegment StartX=139.92 StartY=-60 StartZ=0 EndX=139.92 EndY=-69 EndZ=0
    g24: LineSegment StartX=139.92 StartY=-69 StartZ=0 EndX=152.2 EndY=-69 EndZ=0
  constraints (71):
    c: Coincident(g0,g18)
    c: Coincident(g17,g1)
    c: Coincident(g1,g0)
    c: Horizontal(g0)
    c: Vertical(g1)
    c: PointOnObject(g0,g-1)
    c: Coincident(g2,g3)
    c: Coincident(g3,g15)
    c: Coincident(g16,g4)
    c: Coincident(g4,g2)
    c: Horizontal(g2)
    c: Vertical(g3)
    c: Vertical(g4)
    c: Equal(g3,g1)
    c: Distance(g2,g1) = 116
    c: DistanceX(g2,g2) = 12
    c: Coincident(g2,g-1)
    c: Coincident(g16,g5)
    c: Vertical(g5)
    c: Coincident(g5,g6)
    c: Horizontal(g6)
    c: Coincident(g6,g7)
    c: Vertical(g7)
    c: Coincident(g7,g8)
    c: Horizontal(g8)
    c: Coincident(g8,g9)
    c: Vertical(g10)
    c: Coincident(g10,g11)
    c: Horizontal(g11)
    c: Coincident(g11,g12)
    c: Vertical(g12)
    c: Coincident(g12,g13)
    c: Horizontal(g13)
    c: Coincident(g13,g14)
    c: Vertical(g14)
    c: Vertical(g9)
    c: Coincident(g15,g16)
    c: Horizontal(g15)
    c: Horizontal(g16)
    c: Horizontal(g17)
    c: Coincident(g17,g10)
    c: Coincident(g9,g15)
    c: Equal(g9,g10)
    c: Equal(g17,g15)
    c: Equal(g7,g12)
    c: Distance(g9) = 3
    c: PointOnObject(g3,g7)
    c: DistanceY(g7,g7) = 17
    c: Distance(g15) = 6.5
    c: PointOnObject(g11,g1)
    c: DistanceX(g0) = 152.2
    c: Vertical(g18)
    c: Vertical(g19)
    c: Horizontal(g20)
    c: Coincident(g20,g21)
    c: Vertical(g21)
    c: Coincident(g21,g22)
    c: Horizontal(g22)
    c: Distance(g20,g1) = 5
    c: DistanceY(g4,g4) = 65
    c: Coincident(g22,g23)
    c: Vertical(g23)
    c: Coincident(g23,g24)
    c: Coincident(g24,g14)
    c: Horizontal(g24)
    c: Coincident(g19,g14)
    c: DistanceY(g18,g18) = 5
    c: Distance(g21,g17) = 5
    c: Coincident(g20,g19)
    c: Coincident(g18,g20)
    c: DistanceY(g14,g14) = 16
FEATURE [PartDesign::Pad] Pad001
  BaseFeature = -> Pocket002
  Direction = (0,-1,-2e-16)
  Length = 62
  Length2 = 10
  Profile = -> Sketch004
  ReferenceAxis = -> Sketch004 [N_Axis]
  Reversed = true
  Type = 0
FEATURE [Sketcher::SketchObject] Sketch005
  FullyConstrained = false
  MapMode = 5
  Support = -> [XY_Plane]
  expr: Constraints[35] = <<planB>>#<<data>>.es3_d + 1
  expr: Constraints[36] = <<planB>>#<<data>>.es6_d
  sketch-geometry (18):
    g0: LineSegment StartX=0 StartY=0 StartZ=0 EndX=0 EndY=43 EndZ=0
    g1: LineSegment StartX=152.2 StartY=31 StartZ=0 EndX=152.2 EndY=0 EndZ=0
    g2: LineSegment StartX=152.2 StartY=0 StartZ=0 EndX=0 EndY=0 EndZ=0
    g3: LineSegment StartX=22.6 StartY=0 StartZ=0 EndX=20 EndY=0 EndZ=0
    g4: LineSegment StartX=20 StartY=0 StartZ=0 EndX=20 EndY=43 EndZ=0
    g5: LineSegment StartX=20 StartY=43 StartZ=0 EndX=22.6 EndY=43 EndZ=0
    g6: LineSegment StartX=22.6 StartY=43 StartZ=0 EndX=22.6 EndY=0 EndZ=0
    g7: LineSegment StartX=132.2 StartY=0 StartZ=0 EndX=129.6 EndY=0 EndZ=0
    g8: LineSegment StartX=129.6 StartY=0 StartZ=0 EndX=129.6 EndY=31 EndZ=0
    g9: LineSegment StartX=129.6 StartY=31 StartZ=0 EndX=132.2 EndY=31 EndZ=0
    g10: LineSegment StartX=132.2 StartY=31 StartZ=0 EndX=132.2 EndY=0 EndZ=0
    g11: LineSegment StartX=0 StartY=43 StartZ=0 EndX=76.6 EndY=43 EndZ=0
    g12: LineSegment StartX=76.6 StartY=43 StartZ=0 EndX=76.6 EndY=31 EndZ=0
    g13: LineSegment StartX=76.6 StartY=31 StartZ=0 EndX=152.2 EndY=31 EndZ=0
    g14: LineSegment StartX=-256.513 StartY=459.686 StartZ=0 EndX=467.29 EndY=459.686 EndZ=0
    g15: LineSegment StartX=467.29 StartY=459.686 StartZ=0 EndX=467.29 EndY=-198.667 EndZ=0
    g16: LineSegment StartX=467.29 StartY=-198.667 StartZ=0 EndX=-256.513 EndY=-198.667 EndZ=0
    g17: LineSegment StartX=-256.513 StartY=-198.667 StartZ=0 EndX=-256.513 EndY=459.686 EndZ=0
  constraints (48):
    c: Coincident(g-1,g0)
    c: PointOnObject(g0,g-2)
    c: Coincident(g0,g11)
    c: Coincident(g13,g1)
    c: PointOnObject(g1,g-1)
    c: Vertical(g1)
    c: Coincident(g1,g2)
    c: Coincident(g3,g4)
    c: Coincident(g4,g5)
    c: Coincident(g5,g6)
    c: Coincident(g6,g3)
    c: Horizontal(g3)
    c: Horizontal(g5)
    c: Vertical(g4)
    c: Vertical(g6)
    c: Coincident(g7,g8)
    c: Coincident(g8,g9)
    c: Coincident(g9,g10)
    c: Coincident(g10,g7)
    c: Horizontal(g7)
    c: Horizontal(g9)
    c: Vertical(g8)
    c: Vertical(g10)
    c: PointOnObject(g7,g2)
    c: Equal(g3,g7)
    c: Distance(g3,g4) = 2.6
    c: Coincident(g11,g12)
    c: Horizontal(g11)
    c: PointOnObject(g4,g11)
    c: Coincident(g12,g13)
    c: Horizontal(g13)
    c: PointOnObject(g8,g13)
    c: Vertical(g12)
    c: Distance(g0) = 43
    c: Distance(g1) = 31
    c: Distance(g5,g12) = 54
    c: Distance(g12,g8) = 53
    c: Distance(g7,g1) = 20
    c: Distance(g3,g0) = 20
    c: Coincident(g2,g0)
    c: Coincident(g14,g15)
    c: Coincident(g15,g16)
    c: Coincident(g16,g17)
    c: Coincident(g17,g14)
    c: Horizontal(g14)
    c: Horizontal(g16)
    c: Vertical(g15)
    c: Vertical(g17)
FEATURE [PartDesign::Pocket] Pocket003
  BaseFeature = -> Pad001
  Direction = (0,0,-1)
  Length = 30
  Length2 = 5
  Profile = -> Sketch005
  ReferenceAxis = -> Sketch005 [N_Axis]
  Type = 0
FEATURE [PartDesign::Chamfer] Chamfer
  Angle = 45
  Base = -> Pocket003 [Edge74,Edge76,Edge78,Edge80,Edge36,Edge5]
  BaseFeature = -> Pocket003
  ChamferType = 0
  FlipDirection = false
  Size = 1
  Size2 = 1
  SupportTransform = false
  UseAllEdges = false
FEATURE [PartDesign::Pocket] Pocket
  BaseFeature = -> Chamfer
  Direction = (0,1,2e-16)
  Length = 5
  Length2 = 5
  Profile = -> Sketch001
  ReferenceAxis = -> Sketch001 [N_Axis]
  Type = 1
FEATURE [Sketcher::SketchObject] Sketch006
  FullyConstrained = true
  MapMode = 5
  Placement = pos=(0,0,0) rot=(1,0,0;1.5708rad)
  Support = -> [XZ_Plane]
  sketch-geometry (4):
    g0: LineSegment StartX=12 StartY=-85 StartZ=0 EndX=128 EndY=-85 EndZ=0
    g1: LineSegment StartX=128 StartY=-85 StartZ=0 EndX=128 EndY=-69 EndZ=0
    g2: LineSegment StartX=128 StartY=-69 StartZ=0 EndX=12 EndY=-69 EndZ=0
    g3: LineSegment StartX=12 StartY=-69 StartZ=0 EndX=12 EndY=-85 EndZ=0
  constraints (12):
    c: Coincident(g0,g1)
    c: Coincident(g1,g2)
    c: Coincident(g2,g3)
    c: Coincident(g3,g0)
    c: Horizontal(g0)
    c: Horizontal(g2)
    c: Vertical(g1)
    c: Vertical(g3)
    c: DistanceY(g1,g1) = 16
    c: DistanceX(g2) = 12
    c: DistanceX(g1) = 128
    c: DistanceY(g0) = -85
FEATURE [PartDesign::Pad] Pad002
  BaseFeature = -> Pocket
  Direction = (0,-1,-2e-16)
  Length = 2
  Length2 = 10
  Profile = -> Sketch006
  ReferenceAxis = -> Sketch006 [N_Axis]
  Reversed = true
  Type = 0
FEATURE [PartDesign::Body] Body
  Group = -> [Sketch,Pad,Sketch001,Sketch002,Pocket001,DatumPlane,Sketch003,Pocket002,Sketch004,Pad001,Sketch005,Pocket003,Chamfer,Pocket,Sketch006,Pad002]
  Origin = -> Origin
  Tip = -> Pad002
FEATURE [App::Part] ES_holder
  Group = -> [LCS_0,Body]
  Origin = -> Origin001
---- part ES-holder-end.FCStd = doc fcstd_aee367d4bce2 ----
FCSTD DOCUMENT  (FreeCAD 0.21R33668 +7 (Git))
Label: ES-holder-end
License: All rights reserved
LicenseURL: http://en.wikipedia.org/wiki/All_rights_reserved
objects: Sketcher::SketchObject×4, PartDesign::Pocket×3, PartDesign::Pad×1, PartDesign::CoordinateSystem×1, PartDesign::Plane×1, PartDesign::Chamfer×1, PartDesign::Body×1, App::Part×1
note: 17 computed .brp shape members not serialized (recipe doc carries the construction recipe); baked Part::Feature solids carry a one-line shape summary decoded from their .brp
EXTERNAL_REF file=planB.FCStd obj=Spreadsheet

FEATURE [Sketcher::SketchObject] Sketch
  FullyConstrained = false
  MapMode = 5
  Support = -> [XY_Plane]
  expr: Constraints[35] = <<planB>>#<<data>>.es3_d + 1
  expr: Constraints[36] = <<planB>>#<<data>>.es6_d
  sketch-geometry (14):
    g0: LineSegment StartX=0 StartY=0 StartZ=0 EndX=0 EndY=43 EndZ=0
    g1: LineSegment StartX=152.2 StartY=31 StartZ=0 EndX=152.2 EndY=0 EndZ=0
    g2: LineSegment StartX=152.2 StartY=0 StartZ=0 EndX=0 EndY=0 EndZ=0
    g3: LineSegment StartX=22.6 StartY=0 StartZ=0 EndX=20 EndY=0 EndZ=0
    g4: LineSegment StartX=20 StartY=0 StartZ=0 EndX=20 EndY=43 EndZ=0
    g5: LineSegment StartX=20 StartY=43 StartZ=0 EndX=22.6 EndY=43 EndZ=0
    g6: LineSegment StartX=22.6 StartY=43 StartZ=0 EndX=22.6 EndY=0 EndZ=0
    g7: LineSegment StartX=132.2 StartY=0 StartZ=0 EndX=129.6 EndY=0 EndZ=0
    g8: LineSegment StartX=129.6 StartY=0 StartZ=0 EndX=129.6 EndY=31 EndZ=0
    g9: LineSegment StartX=129.6 StartY=31 StartZ=0 EndX=132.2 EndY=31 EndZ=0
    g10: LineSegment StartX=132.2 StartY=31 StartZ=0 EndX=132.2 EndY=0 EndZ=0
    g11: LineSegment StartX=0 StartY=43 StartZ=0 EndX=76.6 EndY=43 EndZ=0
    g12: LineSegment StartX=76.6 StartY=43 StartZ=0 EndX=76.6 EndY=31 EndZ=0
    g13: LineSegment StartX=76.6 StartY=31 StartZ=0 EndX=152.2 EndY=31 EndZ=0
  constraints (40):
    c: Coincident(g-1,g0)
    c: PointOnObject(g0,g-2)
    c: Coincident(g0,g11)
    c: Coincident(g13,g1)
    c: PointOnObject(g1,g-1)
    c: Vertical(g1)
    c: Coincident(g1,g2)
    c: Coincident(g3,g4)
    c: Coincident(g4,g5)
    c: Coincident(g5,g6)
    c: Coincident(g6,g3)
    c: Horizontal(g3)
    c: Horizontal(g5)
    c: Vertical(g4)
    c: Vertical(g6)
    c: Coincident(g7,g8)
    c: Coincident(g8,g9)
    c: Coincident(g9,g10)
    c: Coincident(g10,g7)
    c: Horizontal(g7)
    c: Horizontal(g9)
    c: Vertical(g8)
    c: Vertical(g10)
    c: PointOnObject(g7,g2)
    c: Equal(g3,g7)
    c: Distance(g3,g4) = 2.6
    c: Coincident(g11,g12)
    c: Horizontal(g11)
    c: PointOnObject(g4,g11)
    c: Coincident(g12,g13)
    c: Horizontal(g13)
    c: PointOnObject(g8,g13)
    c: Vertical(g12)
    c: Distance(g0) = 43
    c: Distance(g1) = 31
    c: Distance(g5,g12) = 54
    c: Distance(g12,g8) = 53
    c: Distance(g7,g1) = 20
    c: Distance(g3,g0) = 20
    c: Coincident(g2,g0)
FEATURE [PartDesign::Pad] Pad
  Direction = (0,0,1)
  Length = 16
  Length2 = 10
  Profile = -> Sketch
  ReferenceAxis = -> Sketch [N_Axis]
  Type = 0
FEATURE [Sketcher::SketchObject] Sketch001
  FullyConstrained = false
  MapMode = 5
  Placement = pos=(0,0,0) rot=(1,0,0;1.5708rad)
  Support = -> [XZ_Plane]
  expr: Constraints[52] = <<planB>>#<<data>>.es6_d + 1 + <<planB>>#<<data>>.es3_d
  expr: Constraints[60] = <<planB>>#<<data>>.insert_diameter
  expr: Constraints[61] = <<planB>>#<<data>>.insert_d + 5
  sketch-geometry (23):
    g0: LineSegment StartX=20 StartY=0 StartZ=0 EndX=20 EndY=17.2745 EndZ=0
    g1: LineSegment StartX=132.2 StartY=0 StartZ=0 EndX=132.2 EndY=26.3444 EndZ=0
    g2: LineSegment StartX=20 StartY=0 StartZ=0 EndX=22.6 EndY=0 EndZ=0
    g3: LineSegment StartX=22.6 StartY=0 StartZ=0 EndX=22.6 EndY=6 EndZ=0
    g4: LineSegment StartX=22.6 StartY=6 StartZ=0 EndX=20 EndY=6 EndZ=0
    g5: LineSegment StartX=20 StartY=6 StartZ=0 EndX=20 EndY=0 EndZ=0
    g6: LineSegment StartX=20 StartY=10 StartZ=0 EndX=22.6 EndY=10 EndZ=0
    g7: LineSegment StartX=22.6 StartY=10 StartZ=0 EndX=22.6 EndY=16 EndZ=0
    g8: LineSegment StartX=22.6 StartY=16 StartZ=0 EndX=20 EndY=16 EndZ=0
    g9: LineSegment StartX=20 StartY=16 StartZ=0 EndX=20 EndY=10 EndZ=0
    g10: LineSegment StartX=132.2 StartY=10 StartZ=0 EndX=129.6 EndY=10 EndZ=0
    g11: LineSegment StartX=129.6 StartY=10 StartZ=0 EndX=129.6 EndY=16 EndZ=0
    g12: LineSegment StartX=129.6 StartY=16 StartZ=0 EndX=132.2 EndY=16 EndZ=0
    g13: LineSegment StartX=132.2 StartY=16 StartZ=0 EndX=132.2 EndY=10 EndZ=0
    g14: LineSegment StartX=132.2 StartY=6 StartZ=0 EndX=129.6 EndY=6 EndZ=0
    g15: LineSegment StartX=129.6 StartY=6 StartZ=0 EndX=129.6 EndY=0 EndZ=0
    g16: LineSegment StartX=129.6 StartY=0 StartZ=0 EndX=132.2 EndY=0 EndZ=0
    g17: LineSegment StartX=132.2 StartY=0 StartZ=0 EndX=132.2 EndY=6 EndZ=0
    g18: Circle CenterX=12 CenterY=8 CenterZ=0 NormalX=0 NormalY=0 NormalZ=1 AngleXU=0 Radius=2.15
    g19: Circle CenterX=89.6 CenterY=8 CenterZ=0 NormalX=0 NormalY=0 NormalZ=1 AngleXU=0 Radius=2.15
    g20: Circle CenterX=140.2 CenterY=8 CenterZ=0 NormalX=0 NormalY=0 NormalZ=1 AngleXU=0 Radius=2.15
    g21: LineSegment StartX=12 StartY=8 StartZ=0 EndX=140.2 EndY=8 EndZ=0
    g22: Circle CenterX=57.6 CenterY=8 CenterZ=0 NormalX=0 NormalY=0 NormalZ=1 AngleXU=0 Radius=2.15
  constraints (67):
    c: PointOnObject(g0,g-1)
    c: Vertical(g0)
    c: PointOnObject(g1,g-1)
    c: Vertical(g1)
    c: DistanceX(g0) = 20
    c: Coincident(g2,g3)
    c: Coincident(g3,g4)
    c: Coincident(g4,g5)
    c: Coincident(g5,g2)
    c: Horizontal(g2)
    c: Horizontal(g4)
    c: Vertical(g3)
    c: Vertical(g5)
    c: Coincident(g2,g0)
    c: Coincident(g6,g7)
    c: Coincident(g7,g8)
    c: Coincident(g8,g9)
    c: Coincident(g9,g6)
    c: Horizontal(g6)
    c: Horizontal(g8)
    c: Vertical(g7)
    c: Vertical(g9)
    c: PointOnObject(g6,g0)
    c: Coincident(g10,g11)
    c: Coincident(g11,g12)
    c: Coincident(g12,g13)
    c: Coincident(g13,g10)
    c: Horizontal(g10)
    c: Horizontal(g12)
    c: Vertical(g11)
    c: Vertical(g13)
    c: PointOnObject(g10,g1)
    c: Coincident(g14,g15)
    c: Coincident(g15,g16)
    c: Coincident(g16,g17)
    c: Coincident(g17,g14)
    c: Horizontal(g14)
    c: Horizontal(g16)
    c: Vertical(g15)
    c: Vertical(g17)
    c: PointOnObject(g14,g1)
    c: PointOnObject(g15,g-1)
    c: Equal(g2,g16)
    c: Equal(g16,g10)
    c: Equal(g10,g8)
    c: Equal(g3,g7)
    c: Equal(g7,g11)
    c: Equal(g11,g15)
    c: Distance(g16) = 2.6
    c: Distance(g11) = 6
    c: Distance(g14,g10) = 4
    c: Distance(g4,g6) = 4
    c: Distance(g7,g11) = 107
    c: Coincident(g21,g18)
    c: Coincident(g21,g20)
    c: Horizontal(g21)
    c: PointOnObject(g19,g21)
    c: Equal(g20,g19)
    c: Equal(g19,g18)
    c: DistanceY(g18) = 8
    c: Diameter(g18) = 4.3
    c: DistanceX(g18) = 12
    c: PointOnObject(g22,g21)
    c: Equal(g22,g19)
    c: Distance(g22,g3) = 35
    c: Distance(g19,g11) = 40
    c: Distance(g20,g13) = 8
FEATURE [PartDesign::Pocket] Pocket
  BaseFeature = -> Pad
  Direction = (0,1,2e-16)
  Length = 5
  Length2 = 5
  Profile = -> Sketch001
  ReferenceAxis = -> Sketch001 [N_Axis]
  Type = 1
FEATURE [PartDesign::CoordinateSystem] LCS_0
  AttacherType = Attacher::AttachEngine3D
  MapMode = 2
  Support = -> [X_Axis001]
FEATURE [Sketcher::SketchObject] Sketch002
  FullyConstrained = true
  MapMode = 5
  Placement = pos=(0,0,0) rot=(0.57735,0.57735,0.57735;2.0944rad)
  Support = -> [YZ_Plane]
  expr: Constraints[0] = <<planB>>#<<data>>.insert_d + 5
  expr: Constraints[2] = <<planB>>#<<data>>.insert_diameter
  sketch-geometry (1):
    g0: Circle CenterX=12 CenterY=8 CenterZ=0 NormalX=0 NormalY=0 NormalZ=1 AngleXU=0 Radius=2.15
  constraints (3):
    c: DistanceX(g0) = 12
    c: DistanceY(g0) = 8
    c: Diameter(g0) = 4.3
FEATURE [PartDesign::Pocket] Pocket001
  BaseFeature = -> Pocket
  Direction = (-1,2e-16,-3e-16)
  Length = 8
  Length2 = 5
  Profile = -> Sketch002
  ReferenceAxis = -> Sketch002 [N_Axis]
  Reversed = true
  Type = 0
  expr: Length = <<planB>>#<<data>>.insert_d + 1
FEATURE [PartDesign::Plane] DatumPlane
  AttachmentOffset = pos=(0,0,152.2) rot=(0,0,1;0rad)
  Length = 60
  MapMode = 5
  Placement = pos=(152.2,-3.38e-14,3.38e-14) rot=(0.57735,0.57735,0.57735;2.0944rad)
  ResizeMode = 0
  Support = -> [YZ_Plane]
  Width = 60
FEATURE [Sketcher::SketchObject] Sketch003
  FullyConstrained = true
  MapMode = 5
  Placement = pos=(152.2,-3.38e-14,3.38e-14) rot=(0.57735,0.57735,0.57735;2.0944rad)
  Support = -> [DatumPlane]
  expr: Constraints[0] = <<planB>>#<<data>>.insert_diameter
  expr: Constraints[1] = <<planB>>#<<data>>.insert_d + 5
  sketch-geometry (1):
    g0: Circle CenterX=12 CenterY=8 CenterZ=0 NormalX=0 NormalY=0 NormalZ=1 AngleXU=0 Radius=2.15
  constraints (3):
    c: Diameter(g0) = 4.3
    c: DistanceX(g0) = 12
    c: DistanceY(g0) = 8
FEATURE [PartDesign::Pocket] Pocket002
  BaseFeature = -> Pocket001
  Direction = (-1,1e-16,-1e-16)
  Length = 8
  Length2 = 5
  Profile = -> Sketch003
  ReferenceAxis = -> Sketch003 [N_Axis]
  Type = 0
  expr: Length = <<planB>>#<<data>>.insert_d + 1
FEATURE [PartDesign::Chamfer] Chamfer
  Angle = 45
  Base = -> Pocket002 [Edge5,Edge20,Edge19,Edge18,Edge17,Edge51,Edge53,Edge55,Edge33,Edge32]
  BaseFeature = -> Pocket002
  ChamferType = 0
  FlipDirection = false
  Size = 1
  Size2 = 1
  SupportTransform = false
  UseAllEdges = false
FEATURE [PartDesign::Body] Body
  Group = -> [Sketch,Pad,Sketch001,Pocket,Sketch002,Pocket001,DatumPlane,Sketch003,Pocket002,Chamfer]
  Origin = -> Origin
  Tip = -> Chamfer
FEATURE [App::Part] ES_holder
  Group = -> [LCS_0,Body]
  Origin = -> Origin001
---- part ES-holder.FCStd = doc fcstd_81ebfeb92755 ----
FCSTD DOCUMENT  (FreeCAD 0.21R33668 +7 (Git))
Label: ES-holder
License: All rights reserved
LicenseURL: http://en.wikipedia.org/wiki/All_rights_reserved
objects: Sketcher::SketchObject×4, PartDesign::Pocket×3, PartDesign::Chamfer×2, PartDesign::Pad×1, PartDesign::CoordinateSystem×1, PartDesign::Plane×1, PartDesign::Body×1, App::Part×1
note: 19 computed .brp shape members not serialized (recipe doc carries the construction recipe); baked Part::Feature solids carry a one-line shape summary decoded from their .brp
EXTERNAL_REF file=planB.FCStd obj=Spreadsheet

FEATURE [Sketcher::SketchObject] Sketch
  FullyConstrained = false
  MapMode = 5
  Support = -> [XY_Plane]
  expr: Constraints[35] = <<planB>>#<<data>>.es3_d + 1
  expr: Constraints[36] = <<planB>>#<<data>>.es6_d
  sketch-geometry (14):
    g0: LineSegment StartX=0 StartY=0 StartZ=0 EndX=0 EndY=43 EndZ=0
    g1: LineSegment StartX=152.2 StartY=31 StartZ=0 EndX=152.2 EndY=0 EndZ=0
    g2: LineSegment StartX=152.2 StartY=0 StartZ=0 EndX=0 EndY=0 EndZ=0
    g3: LineSegment StartX=22.6 StartY=0 StartZ=0 EndX=20 EndY=0 EndZ=0
    g4: LineSegment StartX=20 StartY=0 StartZ=0 EndX=20 EndY=43 EndZ=0
    g5: LineSegment StartX=20 StartY=43 StartZ=0 EndX=22.6 EndY=43 EndZ=0
    g6: LineSegment StartX=22.6 StartY=43 StartZ=0 EndX=22.6 EndY=0 EndZ=0
    g7: LineSegment StartX=132.2 StartY=0 StartZ=0 EndX=129.6 EndY=0 EndZ=0
    g8: LineSegment StartX=129.6 StartY=0 StartZ=0 EndX=129.6 EndY=31 EndZ=0
    g9: LineSegment StartX=129.6 StartY=31 StartZ=0 EndX=132.2 EndY=31 EndZ=0
    g10: LineSegment StartX=132.2 StartY=31 StartZ=0 EndX=132.2 EndY=0 EndZ=0
    g11: LineSegment StartX=0 StartY=43 StartZ=0 EndX=76.6 EndY=43 EndZ=0
    g12: LineSegment StartX=76.6 StartY=43 StartZ=0 EndX=76.6 EndY=31 EndZ=0
    g13: LineSegment StartX=76.6 StartY=31 StartZ=0 EndX=152.2 EndY=31 EndZ=0
  constraints (40):
    c: Coincident(g-1,g0)
    c: PointOnObject(g0,g-2)
    c: Coincident(g0,g11)
    c: Coincident(g13,g1)
    c: PointOnObject(g1,g-1)
    c: Vertical(g1)
    c: Coincident(g1,g2)
    c: Coincident(g3,g4)
    c: Coincident(g4,g5)
    c: Coincident(g5,g6)
    c: Coincident(g6,g3)
    c: Horizontal(g3)
    c: Horizontal(g5)
    c: Vertical(g4)
    c: Vertical(g6)
    c: Coincident(g7,g8)
    c: Coincident(g8,g9)
    c: Coincident(g9,g10)
    c: Coincident(g10,g7)
    c: Horizontal(g7)
    c: Horizontal(g9)
    c: Vertical(g8)
    c: Vertical(g10)
    c: PointOnObject(g7,g2)
    c: Equal(g3,g7)
    c: Distance(g3,g4) = 2.6
    c: Coincident(g11,g12)
    c: Horizontal(g11)
    c: PointOnObject(g4,g11)
    c: Coincident(g12,g13)
    c: Horizontal(g13)
    c: PointOnObject(g8,g13)
    c: Vertical(g12)
    c: Distance(g0) = 43
    c: Distance(g1) = 31
    c: Distance(g5,g12) = 54
    c: Distance(g12,g8) = 53
    c: Distance(g7,g1) = 20
    c: Distance(g3,g0) = 20
    c: Coincident(g2,g0)
FEATURE [PartDesign::Pad] Pad
  Direction = (0,0,1)
  Length = 16
  Length2 = 10
  Profile = -> Sketch
  ReferenceAxis = -> Sketch [N_Axis]
  Type = 0
FEATURE [Sketcher::SketchObject] Sketch001
  FullyConstrained = false
  MapMode = 5
  Placement = pos=(0,0,0) rot=(1,0,0;1.5708rad)
  Support = -> [XZ_Plane]
  expr: Constraints[52] = <<planB>>#<<data>>.es6_d + 1 + <<planB>>#<<data>>.es3_d
  expr: Constraints[60] = <<planB>>#<<data>>.insert_diameter
  expr: Constraints[61] = <<planB>>#<<data>>.insert_d + 5
  sketch-geometry (23):
    g0: LineSegment StartX=20 StartY=0 StartZ=0 EndX=20 EndY=17.2745 EndZ=0
    g1: LineSegment StartX=132.2 StartY=0 StartZ=0 EndX=132.2 EndY=26.3444 EndZ=0
    g2: LineSegment StartX=20 StartY=0 StartZ=0 EndX=22.6 EndY=0 EndZ=0
    g3: LineSegment StartX=22.6 StartY=0 StartZ=0 EndX=22.6 EndY=6 EndZ=0
    g4: LineSegment StartX=22.6 StartY=6 StartZ=0 EndX=20 EndY=6 EndZ=0
    g5: LineSegment StartX=20 StartY=6 StartZ=0 EndX=20 EndY=0 EndZ=0
    g6: LineSegment StartX=20 StartY=10 StartZ=0 EndX=22.6 EndY=10 EndZ=0
    g7: LineSegment StartX=22.6 StartY=10 StartZ=0 EndX=22.6 EndY=16 EndZ=0
    g8: LineSegment StartX=22.6 StartY=16 StartZ=0 EndX=20 EndY=16 EndZ=0
    g9: LineSegment StartX=20 StartY=16 StartZ=0 EndX=20 EndY=10 EndZ=0
    g10: LineSegment StartX=132.2 StartY=10 StartZ=0 EndX=129.6 EndY=10 EndZ=0
    g11: LineSegment StartX=129.6 StartY=10 StartZ=0 EndX=129.6 EndY=16 EndZ=0
    g12: LineSegment StartX=129.6 StartY=16 StartZ=0 EndX=132.2 EndY=16 EndZ=0
    g13: LineSegment StartX=132.2 StartY=16 StartZ=0 EndX=132.2 EndY=10 EndZ=0
    g14: LineSegment StartX=132.2 StartY=6 StartZ=0 EndX=129.6 EndY=6 EndZ=0
    g15: LineSegment StartX=129.6 StartY=6 StartZ=0 EndX=129.6 EndY=0 EndZ=0
    g16: LineSegment StartX=129.6 StartY=0 StartZ=0 EndX=132.2 EndY=0 EndZ=0
    g17: LineSegment StartX=132.2 StartY=0 StartZ=0 EndX=132.2 EndY=6 EndZ=0
    g18: Circle CenterX=12 CenterY=8 CenterZ=0 NormalX=0 NormalY=0 NormalZ=1 AngleXU=0 Radius=2.15
    g19: Circle CenterX=89.6 CenterY=8 CenterZ=0 NormalX=0 NormalY=0 NormalZ=1 AngleXU=0 Radius=2.15
    g20: Circle CenterX=140.2 CenterY=8 CenterZ=0 NormalX=0 NormalY=0 NormalZ=1 AngleXU=0 Radius=2.15
    g21: LineSegment StartX=12 StartY=8 StartZ=0 EndX=140.2 EndY=8 EndZ=0
    g22: Circle CenterX=57.6 CenterY=8 CenterZ=0 NormalX=0 NormalY=0 NormalZ=1 AngleXU=0 Radius=2.15
  constraints (67):
    c: PointOnObject(g0,g-1)
    c: Vertical(g0)
    c: PointOnObject(g1,g-1)
    c: Vertical(g1)
    c: DistanceX(g0) = 20
    c: Coincident(g2,g3)
    c: Coincident(g3,g4)
    c: Coincident(g4,g5)
    c: Coincident(g5,g2)
    c: Horizontal(g2)
    c: Horizontal(g4)
    c: Vertical(g3)
    c: Vertical(g5)
    c: Coincident(g2,g0)
    c: Coincident(g6,g7)
    c: Coincident(g7,g8)
    c: Coincident(g8,g9)
    c: Coincident(g9,g6)
    c: Horizontal(g6)
    c: Horizontal(g8)
    c: Vertical(g7)
    c: Vertical(g9)
    c: PointOnObject(g6,g0)
    c: Coincident(g10,g11)
    c: Coincident(g11,g12)
    c: Coincident(g12,g13)
    c: Coincident(g13,g10)
    c: Horizontal(g10)
    c: Horizontal(g12)
    c: Vertical(g11)
    c: Vertical(g13)
    c: PointOnObject(g10,g1)
    c: Coincident(g14,g15)
    c: Coincident(g15,g16)
    c: Coincident(g16,g17)
    c: Coincident(g17,g14)
    c: Horizontal(g14)
    c: Horizontal(g16)
    c: Vertical(g15)
    c: Vertical(g17)
    c: PointOnObject(g14,g1)
    c: PointOnObject(g15,g-1)
    c: Equal(g2,g16)
    c: Equal(g16,g10)
    c: Equal(g10,g8)
    c: Equal(g3,g7)
    c: Equal(g7,g11)
    c: Equal(g11,g15)
    c: Distance(g16) = 2.6
    c: Distance(g11) = 6
    c: Distance(g14,g10) = 4
    c: Distance(g4,g6) = 4
    c: Distance(g7,g11) = 107
    c: Coincident(g21,g18)
    c: Coincident(g21,g20)
    c: Horizontal(g21)
    c: PointOnObject(g19,g21)
    c: Equal(g20,g19)
    c: Equal(g19,g18)
    c: DistanceY(g18) = 8
    c: Diameter(g18) = 4.3
    c: DistanceX(g18) = 12
    c: PointOnObject(g22,g21)
    c: Equal(g22,g19)
    c: Distance(g22,g3) = 35
    c: Distance(g19,g11) = 40
    c: Distance(g20,g13) = 8
FEATURE [PartDesign::Pocket] Pocket
  BaseFeature = -> Pad
  Direction = (0,1,2e-16)
  Length = 5
  Length2 = 5
  Profile = -> Sketch001
  ReferenceAxis = -> Sketch001 [N_Axis]
  Type = 1
FEATURE [PartDesign::CoordinateSystem] LCS_0
  AttacherType = Attacher::AttachEngine3D
  MapMode = 2
  Support = -> [X_Axis001]
FEATURE [PartDesign::Chamfer] Chamfer
  Angle = 45
  Base = -> Pocket [Edge27,Edge26,Edge25,Edge24,Edge39,Edge40,Edge75,Edge73]
  BaseFeature = -> Pocket
  ChamferType = 0
  FlipDirection = false
  Size = 1
  Size2 = 1
  SupportTransform = false
  UseAllEdges = false
FEATURE [Sketcher::SketchObject] Sketch002
  FullyConstrained = true
  MapMode = 5
  Placement = pos=(0,0,0) rot=(0.57735,0.57735,0.57735;2.0944rad)
  Support = -> [YZ_Plane]
  expr: Constraints[0] = <<planB>>#<<data>>.insert_d + 5
  expr: Constraints[2] = <<planB>>#<<data>>.insert_diameter
  sketch-geometry (1):
    g0: Circle CenterX=12 CenterY=8 CenterZ=0 NormalX=0 NormalY=0 NormalZ=1 AngleXU=0 Radius=2.15
  constraints (3):
    c: DistanceX(g0) = 12
    c: DistanceY(g0) = 8
    c: Diameter(g0) = 4.3
FEATURE [PartDesign::Pocket] Pocket001
  BaseFeature = -> Chamfer
  Direction = (-1,2e-16,-3e-16)
  Length = 8
  Length2 = 5
  Profile = -> Sketch002
  ReferenceAxis = -> Sketch002 [N_Axis]
  Reversed = true
  Type = 0
  expr: Length = <<planB>>#<<data>>.insert_d + 1
FEATURE [PartDesign::Plane] DatumPlane
  AttachmentOffset = pos=(0,0,152.2) rot=(0,0,1;0rad)
  Length = 60
  MapMode = 5
  Placement = pos=(152.2,-3.38e-14,3.38e-14) rot=(0.57735,0.57735,0.57735;2.0944rad)
  ResizeMode = 0
  Support = -> [YZ_Plane]
  Width = 60
FEATURE [Sketcher::SketchObject] Sketch003
  FullyConstrained = true
  MapMode = 5
  Placement = pos=(152.2,-3.38e-14,3.38e-14) rot=(0.57735,0.57735,0.57735;2.0944rad)
  Support = -> [DatumPlane]
  expr: Constraints[0] = <<planB>>#<<data>>.insert_diameter
  expr: Constraints[1] = <<planB>>#<<data>>.insert_d + 5
  sketch-geometry (1):
    g0: Circle CenterX=12 CenterY=8 CenterZ=0 NormalX=0 NormalY=0 NormalZ=1 AngleXU=0 Radius=2.15
  constraints (3):
    c: Diameter(g0) = 4.3
    c: DistanceX(g0) = 12
    c: DistanceY(g0) = 8
FEATURE [PartDesign::Pocket] Pocket002
  BaseFeature = -> Pocket001
  Direction = (-1,1e-16,-1e-16)
  Length = 8
  Length2 = 5
  Profile = -> Sketch003
  ReferenceAxis = -> Sketch003 [N_Axis]
  Type = 0
  expr: Length = <<planB>>#<<data>>.insert_d + 1
FEATURE [PartDesign::Chamfer] Chamfer001
  Angle = 45
  Base = -> Pocket002 [Edge72,Edge50]
  BaseFeature = -> Pocket002
  ChamferType = 0
  FlipDirection = false
  Size = 1
  Size2 = 1
  SupportTransform = false
  UseAllEdges = false
FEATURE [PartDesign::Body] Body
  Group = -> [Sketch,Pad,Sketch001,Pocket,Chamfer,Sketch002,Pocket001,DatumPlane,Sketch003,Pocket002,Chamfer001]
  Origin = -> Origin
  Tip = -> Chamfer001
FEATURE [App::Part] ES_holder
  Group = -> [LCS_0,Body]
  Origin = -> Origin001
---- part L-back.FCStd = doc fcstd_edf278344a96 ----
FCSTD DOCUMENT  (FreeCAD 0.21R33668 +7 (Git))
Label: L-back
License: All rights reserved
LicenseURL: http://en.wikipedia.org/wiki/All_rights_reserved
objects: Sketcher::SketchObject×1, PartDesign::Pad×1, PartDesign::Body×1, PartDesign::CoordinateSystem×1, App::Part×1
note: 5 computed .brp shape members not serialized (recipe doc carries the construction recipe); baked Part::Feature solids carry a one-line shape summary decoded from their .brp
EXTERNAL_REF file=planB.FCStd obj=Spreadsheet

FEATURE [Sketcher::SketchObject] Sketch
  FullyConstrained = true
  MapMode = 5
  Support = -> [XY_Plane]
  expr: Constraints[14] = planB#<<data>>.L_thickness
  expr: Constraints[16] = planB#<<data>>.L_size
  sketch-geometry (6):
    g0: LineSegment StartX=0 StartY=0 StartZ=0 EndX=0 EndY=9.5 EndZ=0
    g1: LineSegment StartX=0 StartY=9.5 StartZ=0 EndX=1.6 EndY=9.5 EndZ=0
    g2: LineSegment StartX=1.6 StartY=9.5 StartZ=0 EndX=1.6 EndY=1.6 EndZ=0
    g3: LineSegment StartX=1.6 StartY=1.6 StartZ=0 EndX=9.5 EndY=1.6 EndZ=0
    g4: LineSegment StartX=9.5 StartY=1.6 StartZ=0 EndX=9.5 EndY=0 EndZ=0
    g5: LineSegment StartX=9.5 StartY=0 StartZ=0 EndX=0 EndY=0 EndZ=0
  constraints (17):
    c: Coincident(g-1,g0)
    c: PointOnObject(g0,g-2)
    c: Coincident(g0,g1)
    c: Horizontal(g1)
    c: Coincident(g1,g2)
    c: Vertical(g2)
    c: Coincident(g2,g3)
    c: Horizontal(g3)
    c: Coincident(g3,g4)
    c: PointOnObject(g4,g-1)
    c: Vertical(g4)
    c: Coincident(g4,g5)
    c: Coincident(g5,g0)
    c: Equal(g4,g1)
    c: Distance(g1) = 1.6
    c: Equal(g0,g5)
    c: Distance(g0) = 9.5
FEATURE [PartDesign::Pad] Pad
  Direction = (0,0,1)
  Length = 490
  Length2 = 10
  Profile = -> Sketch
  ReferenceAxis = -> Sketch [N_Axis]
  Type = 0
  expr: Length = planB#<<data>>.case_w - 10
FEATURE [PartDesign::Body] Body
  Group = -> [Sketch,Pad]
  Origin = -> Origin
  Tip = -> Pad
FEATURE [PartDesign::CoordinateSystem] LCS_0
  AttacherType = Attacher::AttachEngine3D
  MapMode = 2
  Support = -> [X_Axis001]
FEATURE [App::Part] L_back
  Group = -> [LCS_0,Body]
  Origin = -> Origin001
---- part L-front.FCStd = doc fcstd_a248784362d2 ----
FCSTD DOCUMENT  (FreeCAD 0.21R33668 +7 (Git))
Label: L-front
License: All rights reserved
LicenseURL: http://en.wikipedia.org/wiki/All_rights_reserved
objects: Sketcher::SketchObject×1, PartDesign::Pad×1, PartDesign::Body×1, PartDesign::CoordinateSystem×1, App::Part×1
note: 5 computed .brp shape members not serialized (recipe doc carries the construction recipe); baked Part::Feature solids carry a one-line shape summary decoded from their .brp
EXTERNAL_REF file=planB.FCStd obj=Spreadsheet

FEATURE [Sketcher::SketchObject] Sketch
  FullyConstrained = true
  MapMode = 5
  Support = -> [XY_Plane]
  expr: Constraints[14] = planB#<<data>>.L_thickness
  expr: Constraints[16] = planB#<<data>>.L_size
  sketch-geometry (6):
    g0: LineSegment StartX=0 StartY=0 StartZ=0 EndX=0 EndY=9.5 EndZ=0
    g1: LineSegment StartX=0 StartY=9.5 StartZ=0 EndX=1.6 EndY=9.5 EndZ=0
    g2: LineSegment StartX=1.6 StartY=9.5 StartZ=0 EndX=1.6 EndY=1.6 EndZ=0
    g3: LineSegment StartX=1.6 StartY=1.6 StartZ=0 EndX=9.5 EndY=1.6 EndZ=0
    g4: LineSegment StartX=9.5 StartY=1.6 StartZ=0 EndX=9.5 EndY=0 EndZ=0
    g5: LineSegment StartX=9.5 StartY=0 StartZ=0 EndX=0 EndY=0 EndZ=0
  constraints (17):
    c: Coincident(g-1,g0)
    c: PointOnObject(g0,g-2)
    c: Coincident(g0,g1)
    c: Horizontal(g1)
    c: Coincident(g1,g2)
    c: Vertical(g2)
    c: Coincident(g2,g3)
    c: Horizontal(g3)
    c: Coincident(g3,g4)
    c: PointOnObject(g4,g-1)
    c: Vertical(g4)
    c: Coincident(g4,g5)
    c: Coincident(g5,g0)
    c: Equal(g4,g1)
    c: Distance(g1) = 1.6
    c: Equal(g0,g5)
    c: Distance(g0) = 9.5
FEATURE [PartDesign::Pad] Pad
  Direction = (0,0,1)
  Length = 490
  Length2 = 10
  Profile = -> Sketch
  ReferenceAxis = -> Sketch [N_Axis]
  Type = 0
  expr: Length = planB#<<data>>.case_w - 10
FEATURE [PartDesign::Body] Body
  Group = -> [Sketch,Pad]
  Origin = -> Origin
  Tip = -> Pad
FEATURE [PartDesign::CoordinateSystem] LCS_0
  AttacherType = Attacher::AttachEngine3D
  MapMode = 2
  Support = -> [X_Axis001]
FEATURE [App::Part] L_front
  Group = -> [LCS_0,Body]
  Origin = -> Origin001
---- part L-grip-1.FCStd = doc fcstd_6e0011aa34aa ----
FCSTD DOCUMENT  (FreeCAD 0.21R33668 +7 (Git))
Label: L-grip-1
License: All rights reserved
LicenseURL: http://en.wikipedia.org/wiki/All_rights_reserved
objects: Sketcher::SketchObject×4, PartDesign::Pad×3, PartDesign::Draft×1, PartDesign::CoordinateSystem×1, PartDesign::Pocket×1, PartDesign::Body×1, App::Part×1
note: 16 computed .brp shape members not serialized (recipe doc carries the construction recipe); baked Part::Feature solids carry a one-line shape summary decoded from their .brp
EXTERNAL_REF file=planB.FCStd obj=Spreadsheet

FEATURE [Sketcher::SketchObject] Sketch
  FullyConstrained = true
  MapMode = 5
  Support = -> [XY_Plane]
  expr: Constraints[13] = planB#<<data>>.L_size + 0.5 + 0.4
  expr: Constraints[16] = planB#<<data>>.L_thickness + 0.4
  sketch-geometry (19):
    g0: LineSegment StartX=0 StartY=0 StartZ=0 EndX=0 EndY=10.4 EndZ=0
    g1: LineSegment StartX=0 StartY=10.4 StartZ=0 EndX=2 EndY=10.4 EndZ=0
    g2: LineSegment StartX=2 StartY=10.4 StartZ=0 EndX=2 EndY=2 EndZ=0
    g3: LineSegment StartX=2 StartY=2 StartZ=0 EndX=10.4 EndY=2 EndZ=0
    g4: LineSegment StartX=10.4 StartY=2 StartZ=0 EndX=10.4 EndY=0 EndZ=0
    g5: LineSegment StartX=10.4 StartY=0 StartZ=0 EndX=0 EndY=0 EndZ=0
    g6: LineSegment StartX=-0.6 StartY=-0.6 StartZ=0 EndX=11 EndY=-0.6 EndZ=0
    g7: LineSegment StartX=-0.6 StartY=11 StartZ=0 EndX=-0.6 EndY=-0.6 EndZ=0
    g8: LineSegment StartX=0 StartY=0 StartZ=0 EndX=0 EndY=-0.6 EndZ=0
    g9: LineSegment StartX=0 StartY=0 StartZ=0 EndX=-0.6 EndY=0 EndZ=0
    g10: LineSegment StartX=0 StartY=10.4 StartZ=0 EndX=0 EndY=11 EndZ=0
    g11: LineSegment StartX=10.4 StartY=0 StartZ=0 EndX=11 EndY=0 EndZ=0
    g12: LineSegment StartX=11 StartY=11 StartZ=0 EndX=2.6 EndY=11 EndZ=0
    g13: LineSegment StartX=2.6 StartY=11 StartZ=0 EndX=-0.6 EndY=11 EndZ=0
    g14: LineSegment StartX=11 StartY=-0.6 StartZ=0 EndX=11 EndY=2.6 EndZ=0
    g15: LineSegment StartX=11 StartY=2.6 StartZ=0 EndX=11 EndY=11 EndZ=0
    g16: LineSegment StartX=2.6 StartY=11 StartZ=0 EndX=2.6 EndY=2.6 EndZ=0
    g17: LineSegment StartX=2.6 StartY=2.6 StartZ=0 EndX=11 EndY=2.6 EndZ=0
    g18: LineSegment StartX=2.6 StartY=2.6 StartZ=0 EndX=2 EndY=2.6 EndZ=0
  constraints (55):
    c: Coincident(g-1,g0)
    c: PointOnObject(g0,g-2)
    c: Coincident(g0,g1)
    c: Horizontal(g1)
    c: Coincident(g1,g2)
    c: Vertical(g2)
    c: Coincident(g2,g3)
    c: Horizontal(g3)
    c: Coincident(g3,g4)
    c: Vertical(g4)
    c: Coincident(g4,g5)
    c: Coincident(g5,g0)
    c: Horizontal(g5)
    c: DistanceX(g5,g5) = 10.4
    c: Equal(g5,g0)
    c: Equal(g1,g4)
    c: Distance(g4) = 2
    c: Coincident(g6,g14)
    c: Coincident(g15,g12)
    c: Coincident(g13,g7)
    c: Coincident(g7,g6)
    c: Horizontal(g6)
    c: Vertical(g7)
    c: Coincident(g8,g0)
    c: PointOnObject(g8,g6)
    c: Vertical(g8)
    c: Coincident(g9,g0)
    c: PointOnObject(g9,g7)
    c: Horizontal(g9)
    c: Coincident(g10,g0)
    c: Vertical(g10)
    c: Coincident(g11,g4)
    c: Horizontal(g11)
    c: Equal(g8,g9)
    c: Equal(g9,g11)
    c: Equal(g11,g10)
    c: Distance(g9) = 0.6
    c: Coincident(g12,g13)
    c: Horizontal(g12)
    c: Horizontal(g13)
    c: PointOnObject(g10,g13)
    c: Coincident(g14,g15)
    c: Vertical(g14)
    c: Vertical(g15)
    c: PointOnObject(g11,g14)
    c: Coincident(g13,g16)
    c: Vertical(g16)
    c: Coincident(g16,g17)
    c: Coincident(g17,g14)
    c: Horizontal(g17)
    c: Equal(g12,g15)
    c: Coincident(g18,g16)
    c: PointOnObject(g18,g2)
    c: Horizontal(g18)
    c: Equal(g18,g9)
FEATURE [PartDesign::Pad] Pad
  Direction = (0,0,1)
  Length = 6
  Length2 = 10
  Profile = -> Sketch
  ReferenceAxis = -> Sketch [N_Axis]
  Reversed = true
  Type = 0
FEATURE [Sketcher::SketchObject] Sketch001
  FullyConstrained = true
  MapMode = 5
  Support = -> [XY_Plane]
  sketch-geometry (4):
    g0: LineSegment StartX=0 StartY=0 StartZ=0 EndX=10 EndY=0 EndZ=0
    g1: LineSegment StartX=10 StartY=0 StartZ=0 EndX=10 EndY=10 EndZ=0
    g2: LineSegment StartX=10 StartY=10 StartZ=0 EndX=0 EndY=10 EndZ=0
    g3: LineSegment StartX=0 StartY=10 StartZ=0 EndX=0 EndY=0 EndZ=0
  constraints (11):
    c: Coincident(g0,g1)
    c: Coincident(g1,g2)
    c: Coincident(g2,g3)
    c: Coincident(g3,g0)
    c: Horizontal(g0)
    c: Horizontal(g2)
    c: Vertical(g1)
    c: Vertical(g3)
    c: DistanceX(g2,g2) = 10
    c: Equal(g2,g3)
    c: Coincident(g0,g-1)
FEATURE [PartDesign::Pad] Pad001
  BaseFeature = -> Pad
  Direction = (0,0,1)
  Length = 5
  Length2 = 10
  Profile = -> Sketch001
  ReferenceAxis = -> Sketch001 [N_Axis]
  Type = 0
FEATURE [PartDesign::Draft] Draft
  Angle = 0.75
  Base = -> Pad001 [Face14,Face15,Face12,Face17,Face16,Face13]
  BaseFeature = -> Pad001
  NeutralPlane = -> XY_Plane
  Reversed = true
  SupportTransform = false
FEATURE [PartDesign::CoordinateSystem] LCS_0
  AttacherType = Attacher::AttachEngine3D
  MapMode = 2
  Support = -> [X_Axis001]
FEATURE [Sketcher::SketchObject] Sketch002
  FullyConstrained = true
  MapMode = 5
  Support = -> [XY_Plane]
  sketch-geometry (8):
    g0: LineSegment StartX=-0.6 StartY=-0.6 StartZ=0 EndX=11 EndY=-0.6 EndZ=0
    g1: LineSegment StartX=-0.6 StartY=11 StartZ=0 EndX=-0.6 EndY=-0.6 EndZ=0
    g2: LineSegment StartX=11 StartY=11 StartZ=0 EndX=3 EndY=11 EndZ=0
    g3: LineSegment StartX=3 StartY=11 StartZ=0 EndX=-0.6 EndY=11 EndZ=0
    g4: LineSegment StartX=11 StartY=-0.6 StartZ=0 EndX=11 EndY=3 EndZ=0
    g5: LineSegment StartX=11 StartY=3 StartZ=0 EndX=11 EndY=11 EndZ=0
    g6: LineSegment StartX=3 StartY=11 StartZ=0 EndX=3 EndY=3 EndZ=0
    g7: LineSegment StartX=3 StartY=3 StartZ=0 EndX=11 EndY=3 EndZ=0
  constraints (23):
    c: Coincident(g0,g4)
    c: Coincident(g5,g2)
    c: Coincident(g3,g1)
    c: Coincident(g1,g0)
    c: Horizontal(g0)
    c: Vertical(g1)
    c: DistanceX(g0) = -0.6
    c: DistanceY(g0) = -0.6
    c: DistanceX(g5) = 11
    c: DistanceY(g5) = 11
    c: Coincident(g2,g3)
    c: Horizontal(g2)
    c: Horizontal(g3)
    c: Coincident(g4,g5)
    c: Vertical(g4)
    c: Vertical(g5)
    c: Coincident(g2,g6)
    c: Vertical(g6)
    c: Coincident(g6,g7)
    c: Coincident(g7,g4)
    c: Horizontal(g7)
    c: Equal(g3,g4)
    c: Distance(g3) = 3.6
FEATURE [PartDesign::Pad] Pad002
  BaseFeature = -> Draft
  Direction = (0,0,1)
  Length = 0.4
  Length2 = 10
  Profile = -> Sketch002
  ReferenceAxis = -> Sketch002 [N_Axis]
  Reversed = true
  Type = 0
FEATURE [Sketcher::SketchObject] Sketch003
  FullyConstrained = false
  MapMode = 5
  Support = -> [XY_Plane]
  sketch-geometry (4):
    g0: LineSegment StartX=2.6 StartY=2.6 StartZ=0 EndX=11.3763 EndY=2.6 EndZ=0
    g1: LineSegment StartX=11.3763 StartY=2.6 StartZ=0 EndX=11.3763 EndY=11.0694 EndZ=0
    g2: LineSegment StartX=11.3763 StartY=11.0694 StartZ=0 EndX=2.6 EndY=11.0694 EndZ=0
    g3: LineSegment StartX=2.6 StartY=11.0694 StartZ=0 EndX=2.6 EndY=2.6 EndZ=0
  constraints (10):
    c: Coincident(g0,g1)
    c: Coincident(g1,g2)
    c: Coincident(g2,g3)
    c: Coincident(g3,g0)
    c: Horizontal(g0)
    c: Horizontal(g2)
    c: Vertical(g1)
    c: Vertical(g3)
    c: DistanceX(g0) = 2.6
    c: DistanceY(g0) = 2.6
FEATURE [PartDesign::Pocket] Pocket
  BaseFeature = -> Pad002
  Direction = (0,0,-1)
  Length = 2
  Length2 = 5
  Midplane = true
  Profile = -> Sketch003
  ReferenceAxis = -> Sketch003 [N_Axis]
  Type = 0
FEATURE [PartDesign::Body] Body
  Group = -> [Sketch,Pad,Sketch001,Pad001,Draft,Sketch002,Pad002,Sketch003,Pocket]
  Origin = -> Origin
  Tip = -> Pocket
FEATURE [App::Part] L_grip_1
  Group = -> [LCS_0,Body]
  Origin = -> Origin001
---- part back-base.FCStd = doc fcstd_2be91ee090de ----
FCSTD DOCUMENT  (FreeCAD 0.21R33668 +7 (Git))
Label: back-base
License: All rights reserved
LicenseURL: http://en.wikipedia.org/wiki/All_rights_reserved
objects: Sketcher::SketchObject×8, PartDesign::Pocket×6, PartDesign::Plane×2, PartDesign::Pad×1, PartDesign::CoordinateSystem×1, PartDesign::Chamfer×1, PartDesign::Body×1, App::Part×1
note: 28 computed .brp shape members not serialized (recipe doc carries the construction recipe); baked Part::Feature solids carry a one-line shape summary decoded from their .brp
EXTERNAL_REF file=planB.FCStd obj=Spreadsheet

FEATURE [Sketcher::SketchObject] Sketch
  FullyConstrained = true
  MapMode = 5
  Placement = pos=(0,0,0) rot=(1,0,0;1.5708rad)
  Support = -> [XZ_Plane]
  expr: Constraints[13] = <<planB>>#<<data>>.base_t
  expr: Constraints[14] = <<planB>>#<<data>>.mungo_h
  expr: Constraints[15] = <<planB>>#<<data>>.mungo_d + <<planB>>#<<data>>.central_h + 2
  sketch-geometry (8):
    g0: LineSegment StartX=0 StartY=0 StartZ=0 EndX=0 EndY=25 EndZ=0
    g1: LineSegment StartX=0 StartY=25 StartZ=0 EndX=82 EndY=25 EndZ=0
    g2: LineSegment StartX=82 StartY=25 StartZ=0 EndX=82 EndY=5 EndZ=0
    g3: LineSegment StartX=82 StartY=5 StartZ=0 EndX=239 EndY=5 EndZ=0
    g4: LineSegment StartX=239 StartY=5 StartZ=0 EndX=239 EndY=0 EndZ=0
    g5: LineSegment StartX=239 StartY=0 StartZ=0 EndX=236.113 EndY=0 EndZ=0
    g6: LineSegment StartX=236.113 StartY=0 StartZ=0 EndX=0 EndY=0 EndZ=0
    g7: LineSegment StartX=236.113 StartY=0 StartZ=0 EndX=239 EndY=5 EndZ=0
  constraints (22):
    c: Coincident(g-1,g0)
    c: PointOnObject(g0,g-2)
    c: Coincident(g0,g1)
    c: Horizontal(g1)
    c: Coincident(g1,g2)
    c: Vertical(g2)
    c: Coincident(g2,g3)
    c: Horizontal(g3)
    c: Coincident(g3,g4)
    c: PointOnObject(g4,g-1)
    c: Coincident(g4,g5)
    c: Coincident(g6,g0)
    c: Vertical(g4)
    c: Distance(g4) = 5
    c: Distance(g2) = 20
    c: Distance(g1) = 82
    c: DistanceX(g4) = 239
    c: Coincident(g5,g6)
    c: Coincident(g7,g5)
    c: Coincident(g7,g3)
    c: Angle(g5,g7) = 1.0472
    c: Horizontal(g5)
FEATURE [PartDesign::Pad] Pad
  Direction = (0,-1,-2e-16)
  Length = 500
  Length2 = 10
  Placement = pos=(0,0,0) rot=(1,0,0;1.5708rad)
  Profile = -> Sketch
  ReferenceAxis = -> Sketch [N_Axis]
  Type = 0
  expr: Length = <<planB>>#<<data>>.case_w
FEATURE [PartDesign::CoordinateSystem] LCS_0
  AttacherType = Attacher::AttachEngine3D
  MapMode = 2
  Support = -> [X_Axis001]
FEATURE [PartDesign::Plane] DatumPlane
  AttachmentOffset = pos=(0,0,-5) rot=(0,0,1;0rad)
  Length = 338.458
  MapMode = 3
  Placement = pos=(0,-1.1e-15,5) rot=(1,0,0;3.14159rad)
  ResizeMode = 0
  Support = -> [XZ_Plane]
  Width = 599.458
  expr: .AttachmentOffset.Base.z = -<<planB>>#<<data>>.base_t
FEATURE [Sketcher::SketchObject] Sketch001
  FullyConstrained = false
  MapMode = 5
  Placement = pos=(0,-1.1e-15,5) rot=(1,0,0;3.14159rad)
  Support = -> [DatumPlane]
  expr: Constraints[18] = planB#<<data>>.clearance_m3
  expr: Constraints[3] = <<planB>>#<<data>>.central_h
  sketch-geometry (51):
    g0: LineSegment StartX=311.545 StartY=16 StartZ=0 EndX=311.545 EndY=484 EndZ=0
    g1: GeomPoint X=5 Y=250 Z=0
    g2: LineSegment StartX=5 StartY=257 StartZ=0 EndX=7 EndY=257 EndZ=0
    g3: LineSegment StartX=7 StartY=257 StartZ=0 EndX=7 EndY=243 EndZ=0
    g4: LineSegment StartX=7 StartY=243 StartZ=0 EndX=5 EndY=243 EndZ=0
    g5: LineSegment StartX=5 StartY=257 StartZ=0 EndX=5 EndY=243 EndZ=0
    g6: Circle CenterX=3.5 CenterY=253.5 CenterZ=0 NormalX=0 NormalY=0 NormalZ=1 AngleXU=0 Radius=1.8
    g7: LineSegment StartX=0 StartY=253.5 StartZ=0 EndX=3.5 EndY=253.5 EndZ=0
    g8: LineSegment StartX=3.5 StartY=253.5 StartZ=0 EndX=3.5 EndY=257 EndZ=0
    g9: LineSegment StartX=3.5 StartY=253.5 StartZ=0 EndX=7 EndY=253.5 EndZ=0
    g10: LineSegment StartX=5 StartY=250 StartZ=0 EndX=3.5 EndY=250 EndZ=0
    g11: LineSegment StartX=3.5 StartY=250 StartZ=0 EndX=3.5 EndY=253.5 EndZ=0
    g12: LineSegment StartX=74 StartY=40 StartZ=0 EndX=78 EndY=40 EndZ=0
    g13: LineSegment StartX=78 StartY=40 StartZ=0 EndX=78 EndY=16 EndZ=0
    g14: LineSegment StartX=78 StartY=16 StartZ=0 EndX=74 EndY=16 EndZ=0
    g15: LineSegment StartX=74 StartY=23.5 StartZ=0 EndX=74 EndY=40 EndZ=0
    g16: LineSegment StartX=12.5 StartY=16 StartZ=0 EndX=66.5 EndY=16 EndZ=0
    g17: LineSegment StartX=78 StartY=16 StartZ=0 EndX=311.545 EndY=16 EndZ=0
    g18: LineSegment StartX=74 StartY=476.5 StartZ=0 EndX=74 EndY=460 EndZ=0
    g19: LineSegment StartX=74 StartY=460 StartZ=0 EndX=78 EndY=460 EndZ=0
    g20: LineSegment StartX=78 StartY=460 StartZ=0 EndX=78 EndY=484 EndZ=0
    g21: LineSegment StartX=66.5 StartY=484 StartZ=0 EndX=12.5 EndY=484 EndZ=0
    g22: LineSegment StartX=311.545 StartY=484 StartZ=0 EndX=78 EndY=484 EndZ=0
    g23: LineSegment StartX=78 StartY=484 StartZ=0 EndX=74 EndY=484 EndZ=0
    g24: GeomPoint X=5 Y=367 Z=0
    g25: LineSegment StartX=5 StartY=476.5 StartZ=0 EndX=5 EndY=371 EndZ=0
    g26: LineSegment StartX=5 StartY=371 StartZ=0 EndX=5 EndY=363 EndZ=0
    g27: LineSegment StartX=5 StartY=363 StartZ=0 EndX=5 EndY=257 EndZ=0
    g28: Circle CenterX=3.5 CenterY=367 CenterZ=0 NormalX=0 NormalY=0 NormalZ=1 AngleXU=0 Radius=1.8
    g29: LineSegment StartX=5 StartY=367 StartZ=0 EndX=3.5 EndY=367 EndZ=0
    g30: LineSegment StartX=5 StartY=371 StartZ=0 EndX=7 EndY=371 EndZ=0
    g31: LineSegment StartX=7 StartY=371 StartZ=0 EndX=7 EndY=363 EndZ=0
    g32: LineSegment StartX=7 StartY=363 StartZ=0 EndX=5 EndY=363 EndZ=0
    g33: LineSegment StartX=5 StartY=129 StartZ=0 EndX=5 EndY=23.5 EndZ=0
    g34: LineSegment StartX=5 StartY=243 StartZ=0 EndX=5 EndY=137 EndZ=0
    g35: LineSegment StartX=5 StartY=137 StartZ=0 EndX=5 EndY=129 EndZ=0
    g36: LineSegment StartX=5 StartY=137 StartZ=0 EndX=7 EndY=137 EndZ=0
    g37: LineSegment StartX=7 StartY=137 StartZ=0 EndX=7 EndY=129 EndZ=0
    g38: LineSegment StartX=7 StartY=129 StartZ=0 EndX=5 EndY=129 EndZ=0
    g39: GeomPoint X=5 Y=133 Z=0
    g40: ArcOfCircle CenterX=12.5 CenterY=476.5 CenterZ=0 NormalX=0 NormalY=0 NormalZ=1 AngleXU=0 Radius=7.5 StartAngle=1.5708 EndAngle=3.14159
    g41: GeomPoint X=5 Y=484 Z=0
    g42: ArcOfCircle CenterX=12.5 CenterY=23.5 CenterZ=0 NormalX=0 NormalY=0 NormalZ=1 AngleXU=0 Radius=7.5 StartAngle=3.14159 EndAngle=4.71239
    g43: GeomPoint X=5 Y=16 Z=0
    g44: ArcOfCircle CenterX=66.5 CenterY=23.5 CenterZ=0 NormalX=0 NormalY=0 NormalZ=1 AngleXU=0 Radius=7.5 StartAngle=4.71239 EndAngle=6.28319
    g45: GeomPoint X=74 Y=16 Z=0
    g46: ArcOfCircle CenterX=66.5 CenterY=476.5 CenterZ=0 NormalX=0 NormalY=0 NormalZ=1 AngleXU=0 Radius=7.5 StartAngle=1.4e-15 EndAngle=1.5708
    g47: GeomPoint X=74 Y=484 Z=0
    g48: Circle CenterX=81 CenterY=8 CenterZ=0 NormalX=0 NormalY=0 NormalZ=1 AngleXU=0 Radius=5
    g49: LineSegment StartX=81 StartY=8 StartZ=0 EndX=81 EndY=492 EndZ=0
    g50: Circle CenterX=81 CenterY=492 CenterZ=0 NormalX=0 NormalY=0 NormalZ=1 AngleXU=0 Radius=5
  constraints (125):
    c: Coincident(g17,g0)
    c: Coincident(g0,g22)
    c: Vertical(g0)
    c: DistanceX(g43) = 5
    c: DistanceY(g43) = 16
    c: Symmetric(g43,g41,g1)
    c: Horizontal(g2)
    c: Coincident(g2,g3)
    c: Vertical(g3)
    c: Coincident(g3,g4)
    c: Horizontal(g4)
    c: Coincident(g27,g5)
    c: Distance(g41,g43) = 468
    c: Coincident(g5,g34)
    c: Vertical(g5)
    c: Coincident(g5,g4)
    c: Coincident(g27,g2)
    c: Symmetric(g4,g2,g1)
    c: Diameter(g6) = 3.6
    c: PointOnObject(g7,g-2)
    c: Coincident(g7,g6)
    c: Horizontal(g7)
    c: Coincident(g8,g6)
    c: PointOnObject(g8,g2)
    c: Vertical(g8)
    c: Coincident(g9,g6)
    c: Horizontal(g9)
    c: PointOnObject(g9,g3)
    c: Equal(g9,g8)
    c: Equal(g8,g7)
    c: Coincident(g10,g1)
    c: Horizontal(g10)
    c: Coincident(g11,g10)
    c: Coincident(g11,g6)
    c: Vertical(g11)
    c: Equal(g8,g11)
    c: DistanceX(g2) = 7
    c: Coincident(g12,g13)
    c: Coincident(g13,g14)
    c: Coincident(g14,g45)
    c: Coincident(g15,g12)
    c: Horizontal(g12)
    c: Horizontal(g14)
    c: Vertical(g13)
    c: Vertical(g15)
    c: Horizontal(g16)
    c: Horizontal(g17)
    c: DistanceX(g12) = 78
    c: DistanceY(g12) = 40
    c: DistanceX(g45) = 74
    c: Vertical(g18)
    c: Coincident(g18,g19)
    c: Horizontal(g19)
    c: Coincident(g19,g20)
    c: Vertical(g20)
    c: Coincident(g23,g47)
    c: Horizontal(g21)
    c: Coincident(g22,g23)
    c: Horizontal(g22)
    c: Horizontal(g23)
    c: Coincident(g20,g22)
    c: PointOnObject(g19,g13)
    c: PointOnObject(g18,g15)
    c: Equal(g20,g13)
    c: Symmetric(g41,g1,g24)
    c: Coincident(g25,g26)
    c: Vertical(g25)
    c: Coincident(g26,g27)
    c: Vertical(g26)
    c: Coincident(g29,g28)
    c: Horizontal(g29)
    c: DistanceX(g28) = 3.5
    c: Equal(g28,g6)
    c: Coincident(g25,g30)
    c: Horizontal(g30)
    c: Coincident(g30,g31)
    c: Vertical(g31)
    c: Coincident(g31,g32)
    c: Coincident(g32,g27)
    c: Horizontal(g32)
    c: DistanceX(g31) = 7
    c: Symmetric(g27,g25,g24)
    c: DistanceY(g31,g31) = 8
    c: Coincident(g35,g33)
    c: Coincident(g34,g35)
    c: Coincident(g34,g36)
    c: Coincident(g36,g37)
    c: Vertical(g37)
    c: Coincident(g37,g38)
    c: Coincident(g38,g33)
    c: Horizontal(g38)
    c: Horizontal(g36)
    c: Vertical(g35)
    c: PointOnObject(g36,g3)
    c: Symmetric(g33,g34,g39)
    c: Symmetric(g1,g43,g39)
    c: DistanceY(g37,g37) = 8
    c: PointOnObject(g41,g21)
    c: PointOnObject(g41,g25)
    c: Tangent(g21,g40) = -1.5708
    c: Tangent(g25,g40) = -1.5708
    c: PointOnObject(g43,g16)
    c: PointOnObject(g43,g33)
    c: Tangent(g16,g42) = -1.5708
    c: Tangent(g33,g42) = -1.5708
    c: PointOnObject(g45,g16)
    c: PointOnObject(g45,g15)
    c: Tangent(g16,g44) = -1.5708
    c: Tangent(g15,g44) = -1.5708
    c: PointOnObject(g47,g21)
    c: PointOnObject(g47,g18)
    c: Tangent(g21,g46) = -1.5708
    c: Tangent(g18,g46) = 1.5708
    c: Diameter(g40) = 15
    c: Equal(g46,g40)
    c: Equal(g40,g42)
    c: Equal(g42,g44)
    c: DistanceY(g48) = 8
    c: Diameter(g48) = 10
    c: Distance(g48,g13) = 3
    c: Coincident(g49,g48)
    c: Vertical(g49)
    c: Coincident(g50,g49)
    c: Equal(g50,g48)
    c: DistanceY(g49,g49) = 484
FEATURE [PartDesign::Pocket] Pocket
  BaseFeature = -> Pad
  Direction = (0,-2e-16,1)
  Length = 5
  Length2 = 5
  Placement = pos=(0,0,0) rot=(1,0,0;1.5708rad)
  Profile = -> Sketch001
  ReferenceAxis = -> Sketch001 [N_Axis]
  Type = 1
FEATURE [Sketcher::SketchObject] Sketch002
  FullyConstrained = false
  MapMode = 5
  Support = -> [XY_Plane]
  sketch-geometry (15):
    g0: LineSegment StartX=92.4 StartY=-127.6 StartZ=0 EndX=77.7 EndY=-127.6 EndZ=0
    g1: LineSegment StartX=77.7 StartY=-127.6 StartZ=0 EndX=77.7 EndY=-16.3 EndZ=0
    g2: LineSegment StartX=92.4 StartY=-16.3 StartZ=0 EndX=92.4 EndY=-42 EndZ=0
    g3: LineSegment StartX=92.4 StartY=-42 StartZ=0 EndX=92.4 EndY=-127.6 EndZ=0
    g4: LineSegment StartX=77.7 StartY=-16.3 StartZ=0 EndX=82.1 EndY=-16.3 EndZ=0
    g5: LineSegment StartX=82.1 StartY=-16.3 StartZ=0 EndX=92.4 EndY=-16.3 EndZ=0
    g6: LineSegment StartX=92.4 StartY=-42 StartZ=0 EndX=82.1 EndY=-42 EndZ=0
    g7: LineSegment StartX=82.1 StartY=-42 StartZ=0 EndX=82.1 EndY=-16.3 EndZ=0
    g8: LineSegment StartX=0 StartY=-500 StartZ=0 EndX=173.261 EndY=-500 EndZ=0
    g9: LineSegment StartX=77.7 StartY=-483.7 StartZ=0 EndX=77.7 EndY=-372.4 EndZ=0
    g10: LineSegment StartX=77.7 StartY=-372.4 StartZ=0 EndX=92.4 EndY=-372.4 EndZ=0
    g11: LineSegment StartX=92.4 StartY=-372.4 StartZ=0 EndX=92.4 EndY=-458 EndZ=0
    g12: LineSegment StartX=92.4 StartY=-458 StartZ=0 EndX=82.1 EndY=-458 EndZ=0
    g13: LineSegment StartX=82.1 StartY=-458 StartZ=0 EndX=82.1 EndY=-483.7 EndZ=0
    g14: LineSegment StartX=82.1 StartY=-483.7 StartZ=0 EndX=77.7 EndY=-483.7 EndZ=0
  constraints (44):
    c: Coincident(g5,g2)
    c: Coincident(g3,g0)
    c: Coincident(g0,g1)
    c: Coincident(g1,g4)
    c: Horizontal(g0)
    c: Vertical(g1)
    c: DistanceX(g4) = 77.7
    c: DistanceY(g4) = -16.3
    c: DistanceX(g3) = 92.4
    c: DistanceY(g3) = -127.6
    c: Coincident(g2,g3)
    c: Vertical(g2)
    c: Vertical(g3)
    c: Coincident(g4,g5)
    c: Horizontal(g4)
    c: Horizontal(g5)
    c: Horizontal(g6)
    c: Coincident(g6,g7)
    c: Vertical(g7)
    c: Coincident(g6,g2)
    c: Coincident(g7,g4)
    c: Distance(g4) = 4.4
    c: DistanceY(g6) = -42
    c: PointOnObject(g8,g-2)
    c: Horizontal(g8)
    c: DistanceY(g8) = -500
    c: Vertical(g9)
    c: Coincident(g9,g10)
    c: Horizontal(g10)
    c: Coincident(g10,g11)
    c: Vertical(g11)
    c: Coincident(g11,g12)
    c: Horizontal(g12)
    c: Coincident(g12,g13)
    c: Vertical(g13)
    c: Coincident(g13,g14)
    c: Coincident(g14,g9)
    c: PointOnObject(g9,g1)
    c: PointOnObject(g10,g3)
    c: Equal(g2,g13)
    c: Horizontal(g14)
    c: Equal(g4,g14)
    c: Equal(g1,g9)
    c: Distance(g9,g8) = 16.3
FEATURE [PartDesign::Pocket] Pocket001
  BaseFeature = -> Pocket
  Direction = (0,0,-1)
  Length = 5
  Length2 = 5
  Placement = pos=(0,0,0) rot=(1,0,0;1.5708rad)
  Profile = -> Sketch002
  ReferenceAxis = -> Sketch002 [N_Axis]
  Reversed = true
  Type = 1
FEATURE [Sketcher::SketchObject] Sketch003
  FullyConstrained = true
  MapMode = 5
  Support = -> [XY_Plane]
  expr: Constraints[1] = planB#<<data>>.clearance_m3
  expr: Constraints[96] = planB#<<data>>.clearance_m3
  sketch-geometry (42):
    g0: Circle CenterX=3.5 CenterY=-246.5 CenterZ=0 NormalX=0 NormalY=0 NormalZ=1 AngleXU=0 Radius=1.8
    g1: Circle CenterX=3.5 CenterY=-253.5 CenterZ=0 NormalX=0 NormalY=0 NormalZ=1 AngleXU=0 Radius=1.8
    g2: LineSegment StartX=3.5 StartY=-246.5 StartZ=0 EndX=3.5 EndY=-253.5 EndZ=0
    g3: GeomPoint X=3.5 Y=-250 Z=0
    g4: LineSegment StartX=227.2 StartY=-93 StartZ=0 EndX=227.2 EndY=-492 EndZ=0
    g5: LineSegment StartX=227.2 StartY=-93 StartZ=0 EndX=99 EndY=-93 EndZ=0
    g6: LineSegment StartX=99 StartY=-93 StartZ=0 EndX=99 EndY=-492 EndZ=0
    g7: LineSegment StartX=176.6 StartY=-93 StartZ=0 EndX=176.6 EndY=-492 EndZ=0
    g8: LineSegment StartX=144.6 StartY=-93 StartZ=0 EndX=144.6 EndY=-492 EndZ=0
    g9: LineSegment StartX=99 StartY=-492 StartZ=0 EndX=227.2 EndY=-492 EndZ=0
    g10: LineSegment StartX=227.2 StartY=-226 StartZ=0 EndX=99 EndY=-226 EndZ=0
    g11: LineSegment StartX=99 StartY=-359 StartZ=0 EndX=227.2 EndY=-359 EndZ=0
    g12: LineSegment StartX=99 StartY=-492 StartZ=0 EndX=12 EndY=-492 EndZ=0
    g13: LineSegment StartX=70 StartY=-492 StartZ=0 EndX=70 EndY=-8 EndZ=0
    g14: LineSegment StartX=227.2 StartY=-93 StartZ=0 EndX=227.2 EndY=-8 EndZ=0
    g15: LineSegment StartX=227.2 StartY=-8 StartZ=0 EndX=12 EndY=-8 EndZ=0
    g16: LineSegment StartX=12 StartY=-8 StartZ=0 EndX=12 EndY=-492 EndZ=0
    g17: Circle CenterX=227.2 CenterY=-492 CenterZ=0 NormalX=0 NormalY=0 NormalZ=1 AngleXU=0 Radius=1.8
    g18: Circle CenterX=176.6 CenterY=-492 CenterZ=0 NormalX=0 NormalY=0 NormalZ=1 AngleXU=0 Radius=1.8
    g19: Circle CenterX=144.6 CenterY=-492 CenterZ=0 NormalX=0 NormalY=0 NormalZ=1 AngleXU=0 Radius=1.8
    g20: Circle CenterX=99 CenterY=-492 CenterZ=0 NormalX=0 NormalY=0 NormalZ=1 AngleXU=0 Radius=1.8
    g21: Circle CenterX=70 CenterY=-492 CenterZ=0 NormalX=0 NormalY=0 NormalZ=1 AngleXU=0 Radius=1.8
    g22: Circle CenterX=12 CenterY=-492 CenterZ=0 NormalX=0 NormalY=0 NormalZ=1 AngleXU=0 Radius=1.8
    g23: Circle CenterX=99 CenterY=-359 CenterZ=0 NormalX=0 NormalY=0 NormalZ=1 AngleXU=0 Radius=1.8
    g24: Circle CenterX=144.6 CenterY=-359 CenterZ=0 NormalX=0 NormalY=0 NormalZ=1 AngleXU=0 Radius=1.8
    g25: Circle CenterX=176.6 CenterY=-359 CenterZ=0 NormalX=0 NormalY=0 NormalZ=1 AngleXU=0 Radius=1.8
    g26: Circle CenterX=227.2 CenterY=-359 CenterZ=0 NormalX=0 NormalY=0 NormalZ=1 AngleXU=0 Radius=1.8
    g27: Circle CenterX=227.2 CenterY=-226 CenterZ=0 NormalX=0 NormalY=0 NormalZ=1 AngleXU=0 Radius=1.8
    g28: Circle CenterX=99 CenterY=-226 CenterZ=0 NormalX=0 NormalY=0 NormalZ=1 AngleXU=0 Radius=1.8
    g29: Circle CenterX=144.6 CenterY=-226 CenterZ=0 NormalX=0 NormalY=0 NormalZ=1 AngleXU=0 Radius=1.8
    g30: Circle CenterX=176.6 CenterY=-226 CenterZ=0 NormalX=0 NormalY=0 NormalZ=1 AngleXU=0 Radius=1.8
    g31: Circle CenterX=176.6 CenterY=-93 CenterZ=0 NormalX=0 NormalY=0 NormalZ=1 AngleXU=0 Radius=1.8
    g32: Circle CenterX=144.6 CenterY=-93 CenterZ=0 NormalX=0 NormalY=0 NormalZ=1 AngleXU=0 Radius=1.8
    g33: Circle CenterX=99 CenterY=-93 CenterZ=0 NormalX=0 NormalY=0 NormalZ=1 AngleXU=0 Radius=1.8
    g34: Circle CenterX=227.2 CenterY=-93 CenterZ=0 NormalX=0 NormalY=0 NormalZ=1 AngleXU=0 Radius=1.8
    g35: Circle CenterX=227.2 CenterY=-8 CenterZ=0 NormalX=0 NormalY=0 NormalZ=1 AngleXU=0 Radius=1.8
    g36: Circle CenterX=70 CenterY=-8 CenterZ=0 NormalX=0 NormalY=0 NormalZ=1 AngleXU=0 Radius=1.8
    g37: Circle CenterX=12 CenterY=-8 CenterZ=0 NormalX=0 NormalY=0 NormalZ=1 AngleXU=0 Radius=1.8
    g38: LineSegment StartX=3.5 StartY=-253.5 StartZ=0 EndX=3.5 EndY=-367 EndZ=0
    g39: LineSegment StartX=3.5 StartY=-246.5 StartZ=0 EndX=3.5 EndY=-133 EndZ=0
    g40: Circle CenterX=3.5 CenterY=-133 CenterZ=0 NormalX=0 NormalY=0 NormalZ=1 AngleXU=0 Radius=1.8
    g41: Circle CenterX=3.5 CenterY=-367 CenterZ=0 NormalX=0 NormalY=0 NormalZ=1 AngleXU=0 Radius=1.8
  constraints (108):
    c: Equal(g1,g0)
    c: Diameter(g0) = 3.6
    c: Coincident(g2,g0)
    c: Coincident(g2,g1)
    c: Vertical(g2)
    c: Symmetric(g1,g0,g3)
    c: DistanceX(g3) = 3.5
    c: DistanceY(g3) = -250
    c: Vertical(g4)
    c: Coincident(g5,g4)
    c: Horizontal(g5)
    c: Coincident(g6,g5)
    c: Vertical(g6)
    c: PointOnObject(g7,g5)
    c: Vertical(g7)
    c: PointOnObject(g8,g5)
    c: Vertical(g8)
    c: Coincident(g9,g6)
    c: Coincident(g9,g4)
    c: Horizontal(g9)
    c: PointOnObject(g7,g9)
    c: PointOnObject(g8,g9)
    c: PointOnObject(g10,g4)
    c: PointOnObject(g10,g6)
    c: Horizontal(g10)
    c: PointOnObject(g11,g6)
    c: PointOnObject(g11,g4)
    c: Horizontal(g11)
    c: Distance(g11,g9) = 133
    c: Distance(g11,g10) = 133
    c: Distance(g10,g5) = 133
    c: DistanceX(g4) = 227.2
    c: DistanceY(g4) = -93
    c: DistanceX(g7) = 176.6
    c: DistanceX(g8) = 144.6
    c: DistanceX(g5) = 99
    c: Horizontal(g12)
    c: PointOnObject(g13,g12)
    c: Vertical(g13)
    c: Vertical(g14)
    c: Coincident(g4,g14)
    c: Horizontal(g15)
    c: Vertical(g16)
    c: Coincident(g12,g16)
    c: Coincident(g15,g16)
    c: PointOnObject(g13,g15)
    c: Coincident(g15,g14)
    c: DistanceY(g14) = -8
    c: DistanceX(g15) = 12
    c: DistanceX(g13) = 70
    c: Coincident(g12,g6)
    c: Coincident(g17,g4)
    c: Coincident(g18,g7)
    c: Coincident(g19,g8)
    c: Coincident(g20,g6)
    c: Coincident(g21,g13)
    c: Coincident(g22,g12)
    c: Coincident(g23,g11)
    c: PointOnObject(g24,g8)
    c: PointOnObject(g25,g7)
    c: Coincident(g26,g11)
    c: Coincident(g27,g10)
    c: Coincident(g28,g10)
    c: PointOnObject(g29,g8)
    c: PointOnObject(g30,g7)
    c: Coincident(g31,g7)
    c: Coincident(g32,g8)
    c: Coincident(g33,g5)
    c: Coincident(g34,g4)
    c: Coincident(g35,g14)
    c: Coincident(g36,g13)
    c: Coincident(g37,g15)
    c: Equal(g35,g36)
    c: Equal(g36,g37)
    c: Equal(g37,g33)
    c: Equal(g33,g32)
    c: Equal(g32,g31)
    c: Equal(g31,g34)
    c: Equal(g34,g27)
    c: Equal(g27,g28)
    c: Equal(g28,g29)
    c: Equal(g29,g30)
    c: Equal(g30,g26)
    c: Equal(g26,g25)
    c: Equal(g25,g24)
    c: Equal(g24,g23)
    c: Equal(g23,g17)
    c: Equal(g17,g18)
    c: Equal(g18,g19)
    c: Equal(g19,g20)
    c: Equal(g20,g21)
    c: Equal(g21,g22)
    c: PointOnObject(g25,g11)
    c: PointOnObject(g24,g11)
    c: PointOnObject(g29,g10)
    c: PointOnObject(g30,g10)
    c: Diameter(g36) = 3.6
    c: Coincident(g38,g1)
    c: Vertical(g38)
    c: Coincident(g39,g0)
    c: Vertical(g39)
    c: Coincident(g40,g39)
    c: Coincident(g41,g38)
    c: Equal(g41,g1)
    c: Equal(g0,g40)
    c: Equal(g39,g38)
    c: DistanceY(g40) = -133
    c: DistanceY(g2,g2) = 7
FEATURE [PartDesign::Pocket] Pocket002
  BaseFeature = -> Pocket001
  Direction = (0,0,-1)
  Length = 63
  Length2 = 5
  Midplane = true
  Placement = pos=(0,0,0) rot=(1,0,0;1.5708rad)
  Profile = -> Sketch003
  ReferenceAxis = -> Sketch003 [N_Axis]
  Type = 0
FEATURE [Sketcher::SketchObject] Sketch004
  FullyConstrained = false
  MapMode = 5
  Support = -> [XY_Plane]
  expr: Constraints[1] = planB#<<data>>.clearance_m3
  sketch-geometry (10):
    g0: Circle CenterX=3.5 CenterY=-246.5 CenterZ=0 NormalX=0 NormalY=0 NormalZ=1 AngleXU=0 Radius=1.8
    g1: Circle CenterX=3.5 CenterY=-253.5 CenterZ=0 NormalX=0 NormalY=0 NormalZ=1 AngleXU=0 Radius=1.8
    g2: LineSegment StartX=3.5 StartY=-246.5 StartZ=0 EndX=3.5 EndY=-253.5 EndZ=0
    g3: GeomPoint X=3.5 Y=-250 Z=0
    g4: ArcOfCircle CenterX=3.5 CenterY=-246.5 CenterZ=0 NormalX=0 NormalY=0 NormalZ=1 AngleXU=0 Radius=3.5 StartAngle=3.1e-15 EndAngle=1.57652
    g5: ArcOfCircle CenterX=3.5 CenterY=-253.5 CenterZ=0 NormalX=0 NormalY=0 NormalZ=1 AngleXU=0 Radius=3.5 StartAngle=4.72257 EndAngle=6.28319
    g6: LineSegment StartX=7 StartY=-253.5 StartZ=0 EndX=7 EndY=-246.5 EndZ=0
    g7: LineSegment StartX=3.47998 StartY=-243 StartZ=0 EndX=0 EndY=-243 EndZ=0
    g8: LineSegment StartX=3.53564 StartY=-257 StartZ=0 EndX=0 EndY=-257 EndZ=0
    g9: LineSegment StartX=0 StartY=-243 StartZ=0 EndX=0 EndY=-257 EndZ=0
  constraints (23):
    c: Equal(g1,g0)
    c: Diameter(g0) = 3.6
    c: Coincident(g2,g0)
    c: Coincident(g2,g1)
    c: Vertical(g2)
    c: Symmetric(g1,g0,g3)
    c: DistanceX(g3) = 3.5
    c: DistanceY(g3) = -250
    c: Coincident(g4,g0)
    c: Coincident(g5,g1)
    c: Vertical(g6)
    c: Coincident(g7,g4)
    c: PointOnObject(g7,g-2)
    c: Horizontal(g7)
    c: Coincident(g8,g5)
    c: PointOnObject(g8,g-2)
    c: Horizontal(g8)
    c: Tangent(g6,g5) = -1.5708
    c: Tangent(g6,g4) = -1.5708
    c: DistanceY(g5,g4) = 7
    c: Coincident(g9,g7)
    c: Coincident(g9,g8)
    c: Diameter(g4) = 7
FEATURE [Sketcher::SketchObject] Sketch005
  FullyConstrained = false
  MapMode = 5
  Support = -> [XY_Plane]
  expr: Constraints[1] = planB#<<data>>.clearance_m3
  sketch-geometry (50):
    g0: Circle CenterX=3.5 CenterY=-246.5 CenterZ=0 NormalX=0 NormalY=0 NormalZ=1 AngleXU=0 Radius=1.8
    g1: Circle CenterX=3.5 CenterY=-253.5 CenterZ=0 NormalX=0 NormalY=0 NormalZ=1 AngleXU=0 Radius=1.8
    g2: LineSegment StartX=3.5 StartY=-246.5 StartZ=0 EndX=3.5 EndY=-253.5 EndZ=0
    g3: GeomPoint X=3.5 Y=-250 Z=0
    g4: LineSegment StartX=227.2 StartY=-93 StartZ=0 EndX=227.2 EndY=-492 EndZ=0
    g5: LineSegment StartX=227.2 StartY=-93 StartZ=0 EndX=99 EndY=-93 EndZ=0
    g6: LineSegment StartX=99 StartY=-93 StartZ=0 EndX=99 EndY=-492 EndZ=0
    g7: LineSegment StartX=176.6 StartY=-93 StartZ=0 EndX=176.6 EndY=-492 EndZ=0
    g8: LineSegment StartX=144.6 StartY=-93 StartZ=0 EndX=144.6 EndY=-492 EndZ=0
    g9: LineSegment StartX=99 StartY=-492 StartZ=0 EndX=227.2 EndY=-492 EndZ=0
    g10: LineSegment StartX=227.2 StartY=-226 StartZ=0 EndX=99 EndY=-226 EndZ=0
    g11: LineSegment StartX=99 StartY=-359 StartZ=0 EndX=227.2 EndY=-359 EndZ=0
    g12: LineSegment StartX=99 StartY=-492 StartZ=0 EndX=12 EndY=-492 EndZ=0
    g13: LineSegment StartX=70 StartY=-492 StartZ=0 EndX=70 EndY=-8 EndZ=0
    g14: LineSegment StartX=227.2 StartY=-93 StartZ=0 EndX=227.2 EndY=-8 EndZ=0
    g15: LineSegment StartX=227.2 StartY=-8 StartZ=0 EndX=12 EndY=-8 EndZ=0
    g16: LineSegment StartX=12 StartY=-8 StartZ=0 EndX=12 EndY=-492 EndZ=0
    g17: Circle CenterX=227.2 CenterY=-492 CenterZ=0 NormalX=0 NormalY=0 NormalZ=1 AngleXU=0 Radius=4
    g18: Circle CenterX=176.6 CenterY=-492 CenterZ=0 NormalX=0 NormalY=0 NormalZ=1 AngleXU=0 Radius=4
    g19: Circle CenterX=144.6 CenterY=-492 CenterZ=0 NormalX=0 NormalY=0 NormalZ=1 AngleXU=0 Radius=4
    g20: Circle CenterX=99 CenterY=-492 CenterZ=0 NormalX=0 NormalY=0 NormalZ=1 AngleXU=0 Radius=4
    g21: Circle CenterX=70 CenterY=-492 CenterZ=0 NormalX=0 NormalY=0 NormalZ=1 AngleXU=0 Radius=4
    g22: Circle CenterX=12 CenterY=-492 CenterZ=0 NormalX=0 NormalY=0 NormalZ=1 AngleXU=0 Radius=4
    g23: Circle CenterX=99 CenterY=-359 CenterZ=0 NormalX=0 NormalY=0 NormalZ=1 AngleXU=0 Radius=4
    g24: Circle CenterX=144.6 CenterY=-359 CenterZ=0 NormalX=0 NormalY=0 NormalZ=1 AngleXU=0 Radius=4
    g25: Circle CenterX=176.6 CenterY=-359 CenterZ=0 NormalX=0 NormalY=0 NormalZ=1 AngleXU=0 Radius=4
    g26: Circle CenterX=227.2 CenterY=-359 CenterZ=0 NormalX=0 NormalY=0 NormalZ=1 AngleXU=0 Radius=4
    g27: Circle CenterX=227.2 CenterY=-226 CenterZ=0 NormalX=0 NormalY=0 NormalZ=1 AngleXU=0 Radius=4
    g28: Circle CenterX=99 CenterY=-226 CenterZ=0 NormalX=0 NormalY=0 NormalZ=1 AngleXU=0 Radius=4
    g29: Circle CenterX=144.6 CenterY=-226 CenterZ=0 NormalX=0 NormalY=0 NormalZ=1 AngleXU=0 Radius=4
    g30: Circle CenterX=176.6 CenterY=-226 CenterZ=0 NormalX=0 NormalY=0 NormalZ=1 AngleXU=0 Radius=4
    g31: Circle CenterX=176.6 CenterY=-93 CenterZ=0 NormalX=0 NormalY=0 NormalZ=1 AngleXU=0 Radius=4
    g32: Circle CenterX=144.6 CenterY=-93 CenterZ=0 NormalX=0 NormalY=0 NormalZ=1 AngleXU=0 Radius=4
    g33: Circle CenterX=99 CenterY=-93 CenterZ=0 NormalX=0 NormalY=0 NormalZ=1 AngleXU=0 Radius=4
    g34: Circle CenterX=227.2 CenterY=-93 CenterZ=0 NormalX=0 NormalY=0 NormalZ=1 AngleXU=0 Radius=4
    g35: Circle CenterX=227.2 CenterY=-8 CenterZ=0 NormalX=0 NormalY=0 NormalZ=1 AngleXU=0 Radius=4
    g36: Circle CenterX=70 CenterY=-8 CenterZ=0 NormalX=0 NormalY=0 NormalZ=1 AngleXU=0 Radius=4
    g37: Circle CenterX=12 CenterY=-8 CenterZ=0 NormalX=0 NormalY=0 NormalZ=1 AngleXU=0 Radius=4
    g38: LineSegment StartX=3.5 StartY=-253.5 StartZ=0 EndX=3.5 EndY=-367 EndZ=0
    g39: LineSegment StartX=3.5 StartY=-246.5 StartZ=0 EndX=3.5 EndY=-133 EndZ=0
    g40: Circle CenterX=3.5 CenterY=-133 CenterZ=0 NormalX=0 NormalY=0 NormalZ=1 AngleXU=0 Radius=4
    g41: Circle CenterX=3.5 CenterY=-367 CenterZ=0 NormalX=0 NormalY=0 NormalZ=1 AngleXU=0 Radius=4
    g42: ArcOfCircle CenterX=3.5 CenterY=-133 CenterZ=0 NormalX=0 NormalY=0 NormalZ=1 AngleXU=0 Radius=4 StartAngle=4.71239 EndAngle=7.85398
    g43: ArcOfCircle CenterX=-20.3762 CenterY=-133 CenterZ=0 NormalX=0 NormalY=0 NormalZ=1 AngleXU=0 Radius=4 StartAngle=1.5708 EndAngle=4.71239
    g44: LineSegment StartX=3.5 StartY=-129 StartZ=0 EndX=-20.3762 EndY=-129 EndZ=0
    g45: LineSegment StartX=-20.3762 StartY=-137 StartZ=0 EndX=3.5 EndY=-137 EndZ=0
    g46: ArcOfCircle CenterX=3.5 CenterY=-367 CenterZ=0 NormalX=0 NormalY=0 NormalZ=1 AngleXU=0 Radius=4 StartAngle=4.71239 EndAngle=7.85398
    g47: ArcOfCircle CenterX=-12.5759 CenterY=-367 CenterZ=0 NormalX=0 NormalY=0 NormalZ=1 AngleXU=0 Radius=4 StartAngle=1.5708 EndAngle=4.71239
    g48: LineSegment StartX=3.5 StartY=-363 StartZ=0 EndX=-12.5759 EndY=-363 EndZ=0
    g49: LineSegment StartX=-12.5759 StartY=-371 StartZ=0 EndX=3.5 EndY=-371 EndZ=0
  constraints (124):
    c: Equal(g1,g0)
    c: Diameter(g0) = 3.6
    c: Coincident(g2,g0)
    c: Coincident(g2,g1)
    c: Vertical(g2)
    c: Symmetric(g1,g0,g3)
    c: DistanceX(g3) = 3.5
    c: DistanceY(g3) = -250
    c: Vertical(g4)
    c: Coincident(g5,g4)
    c: Horizontal(g5)
    c: Coincident(g6,g5)
    c: Vertical(g6)
    c: PointOnObject(g7,g5)
    c: Vertical(g7)
    c: PointOnObject(g8,g5)
    c: Vertical(g8)
    c: Coincident(g9,g6)
    c: Coincident(g9,g4)
    c: Horizontal(g9)
    c: PointOnObject(g7,g9)
    c: PointOnObject(g8,g9)
    c: PointOnObject(g10,g4)
    c: PointOnObject(g10,g6)
    c: Horizontal(g10)
    c: PointOnObject(g11,g6)
    c: PointOnObject(g11,g4)
    c: Horizontal(g11)
    c: Distance(g11,g9) = 133
    c: Distance(g11,g10) = 133
    c: Distance(g10,g5) = 133
    c: DistanceX(g4) = 227.2
    c: DistanceY(g4) = -93
    c: DistanceX(g7) = 176.6
    c: DistanceX(g8) = 144.6
    c: DistanceX(g5) = 99
    c: Horizontal(g12)
    c: PointOnObject(g13,g12)
    c: Vertical(g13)
    c: Vertical(g14)
    c: Coincident(g4,g14)
    c: Horizontal(g15)
    c: Vertical(g16)
    c: Coincident(g12,g16)
    c: Coincident(g15,g16)
    c: PointOnObject(g13,g15)
    c: Coincident(g15,g14)
    c: DistanceY(g14) = -8
    c: DistanceX(g15) = 12
    c: DistanceX(g13) = 70
    c: Coincident(g12,g6)
    c: Coincident(g17,g4)
    c: Coincident(g18,g7)
    c: Coincident(g19,g8)
    c: Coincident(g20,g6)
    c: Coincident(g21,g13)
    c: Coincident(g22,g12)
    c: Coincident(g23,g11)
    c: PointOnObject(g24,g8)
    c: PointOnObject(g25,g7)
    c: Coincident(g26,g11)
    c: Coincident(g27,g10)
    c: Coincident(g28,g10)
    c: PointOnObject(g29,g8)
    c: PointOnObject(g30,g7)
    c: Coincident(g31,g7)
    c: Coincident(g32,g8)
    c: Coincident(g33,g5)
    c: Coincident(g34,g4)
    c: Coincident(g35,g14)
    c: Coincident(g36,g13)
    c: Coincident(g37,g15)
    c: Equal(g35,g36)
    c: Equal(g36,g37)
    c: Equal(g37,g33)
    c: Equal(g33,g32)
    c: Equal(g32,g31)
    c: Equal(g31,g34)
    c: Equal(g34,g27)
    c: Equal(g27,g28)
    c: Equal(g28,g29)
    c: Equal(g29,g30)
    c: Equal(g30,g26)
    c: Equal(g26,g25)
    c: Equal(g25,g24)
    c: Equal(g24,g23)
    c: Equal(g23,g17)
    c: Equal(g17,g18)
    c: Equal(g18,g19)
    c: Equal(g19,g20)
    c: Equal(g20,g21)
    c: Equal(g21,g22)
    c: PointOnObject(g25,g11)
    c: PointOnObject(g24,g11)
    c: PointOnObject(g29,g10)
    c: PointOnObject(g30,g10)
    c: Diameter(g37) = 8
    c: Coincident(g38,g1)
    c: Vertical(g38)
    c: Coincident(g39,g0)
    c: Vertical(g39)
    c: Coincident(g40,g39)
    c: Coincident(g41,g38)
    c: DistanceY(g1,g0) = 7
    c: Equal(g38,g39)
    c: DistanceY(g40) = -133
    c: Equal(g41,g23)
    c: Equal(g40,g41)
    c: Tangent(g42,g44) = -1.5708
    c: Tangent(g44,g43) = -1.5708
    c: Tangent(g43,g45) = -1.5708
    c: Tangent(g45,g42) = -1.5708
    c: Equal(g42,g43)
    c: Coincident(g42,g39)
    c: Horizontal(g44)
    c: Tangent(g46,g48) = -1.5708
    c: Tangent(g48,g47) = -1.5708
    c: Tangent(g47,g49) = -1.5708
    c: Tangent(g49,g46) = -1.5708
    c: Equal(g46,g47)
    c: Coincident(g46,g38)
    c: Horizontal(g48)
    c: Equal(g41,g46)
    c: Equal(g40,g42)
FEATURE [PartDesign::Plane] DatumPlane001
  AttachmentOffset = pos=(0,0,79) rot=(0,0,1;0rad)
  Length = 557.404
  MapMode = 5
  Placement = pos=(79,-1.75e-14,1.75e-14) rot=(0.57735,0.57735,0.57735;2.0944rad)
  ResizeMode = 0
  Support = -> [YZ_Plane]
  Width = 82.4037
FEATURE [Sketcher::SketchObject] Sketch006
  FullyConstrained = false
  MapMode = 5
  Placement = pos=(79,-1.75e-14,1.75e-14) rot=(0.57735,0.57735,0.57735;2.0944rad)
  Support = -> [DatumPlane001]
  sketch-geometry (9):
    g0: ArcOfCircle CenterX=-30 CenterY=12.5 CenterZ=0 NormalX=0 NormalY=0 NormalZ=1 AngleXU=0 Radius=5 StartAngle=3.14159 EndAngle=6.28319
    g1: LineSegment StartX=-35 StartY=12.5 StartZ=0 EndX=-35 EndY=55.1269 EndZ=0
    g2: LineSegment StartX=-35 StartY=55.1269 StartZ=0 EndX=-25 EndY=55.1269 EndZ=0
    g3: LineSegment StartX=-25 StartY=55.1269 StartZ=0 EndX=-25 EndY=12.5 EndZ=0
    g4: ArcOfCircle CenterX=-470 CenterY=12.5 CenterZ=0 NormalX=0 NormalY=0 NormalZ=1 AngleXU=0 Radius=5 StartAngle=3.14159 EndAngle=6.28319
    g5: ArcOfCircle CenterX=-470 CenterY=75.1601 CenterZ=0 NormalX=0 NormalY=0 NormalZ=1 AngleXU=0 Radius=5 StartAngle=0 EndAngle=3.14159
    g6: LineSegment StartX=-465 StartY=12.5 StartZ=0 EndX=-465 EndY=75.1601 EndZ=0
    g7: LineSegment StartX=-475 StartY=75.1601 StartZ=0 EndX=-475 EndY=12.5 EndZ=0
    g8: LineSegment StartX=-470 StartY=12.5 StartZ=0 EndX=-30 EndY=12.5 EndZ=0
  constraints (21):
    c: DistanceY(g0) = 12.5
    c: Diameter(g0) = 10
    c: DistanceX(g0) = -30
    c: Vertical(g1)
    c: Coincident(g1,g2)
    c: Horizontal(g2)
    c: Coincident(g2,g3)
    c: Vertical(g3)
    c: Tangent(g0,g3) = 1.5708
    c: Tangent(g0,g1) = 1.5708
    c: Tangent(g4,g6) = -1.5708
    c: Tangent(g6,g5) = -1.5708
    c: Tangent(g5,g7) = -1.5708
    c: Tangent(g7,g4) = -1.5708
    c: Equal(g4,g5)
    c: Vertical(g6)
    c: Equal(g0,g4)
    c: Coincident(g8,g4)
    c: Coincident(g8,g0)
    c: Horizontal(g8)
    c: Distance(g8) = 440
FEATURE [PartDesign::Pocket] Pocket005
  BaseFeature = -> Pocket002
  Direction = (-1,1e-16,-1e-16)
  Length = 6
  Length2 = 5
  Placement = pos=(0,0,0) rot=(1,0,0;1.5708rad)
  Profile = -> Sketch006
  ReferenceAxis = -> Sketch006 [N_Axis]
  Type = 0
FEATURE [Sketcher::SketchObject] Sketch007
  FullyConstrained = false
  MapMode = 5
  Support = -> [XY_Plane]
  sketch-geometry (12):
    g0: LineSegment StartX=7.5 StartY=-2.7e-15 StartZ=0 EndX=252.941 EndY=-2.7e-15 EndZ=0
    g1: LineSegment StartX=252.941 StartY=-2.7e-15 StartZ=0 EndX=252.941 EndY=-500 EndZ=0
    g2: LineSegment StartX=252.941 StartY=-500 StartZ=0 EndX=7.5 EndY=-500 EndZ=0
    g3: LineSegment StartX=2.7e-15 StartY=-492.5 StartZ=0 EndX=2.7e-15 EndY=-7.5 EndZ=0
    g4: ArcOfCircle CenterX=7.5 CenterY=-492.5 CenterZ=0 NormalX=0 NormalY=0 NormalZ=1 AngleXU=0 Radius=7.5 StartAngle=3.14159 EndAngle=4.71239
    g5: GeomPoint X=0 Y=-500 Z=0
    g6: ArcOfCircle CenterX=7.5 CenterY=-7.5 CenterZ=0 NormalX=0 NormalY=0 NormalZ=1 AngleXU=0 Radius=7.5 StartAngle=1.5708 EndAngle=3.14159
    g7: GeomPoint X=0 Y=0 Z=0
    g8: LineSegment StartX=-59.6212 StartY=32.9892 StartZ=0 EndX=360.075 EndY=32.9892 EndZ=0
    g9: LineSegment StartX=360.075 StartY=32.9892 StartZ=0 EndX=360.075 EndY=-541.729 EndZ=0
    g10: LineSegment StartX=360.075 StartY=-541.729 StartZ=0 EndX=-59.6212 EndY=-541.729 EndZ=0
    g11: LineSegment StartX=-59.6212 StartY=-541.729 StartZ=0 EndX=-59.6212 EndY=32.9892 EndZ=0
  constraints (26):
    c: Coincident(g0,g1)
    c: Coincident(g1,g2)
    c: Horizontal(g0)
    c: Horizontal(g2)
    c: Vertical(g1)
    c: Vertical(g3)
    c: Coincident(g7,g-1)
    c: Distance(g1) = 500
    c: PointOnObject(g5,g2)
    c: PointOnObject(g5,g3)
    c: Tangent(g2,g4) = 1.5708
    c: Tangent(g3,g4) = 1.5708
    c: PointOnObject(g7,g3)
    c: PointOnObject(g7,g0)
    c: Tangent(g3,g6) = 1.5708
    c: Tangent(g0,g6) = 1.5708
    c: Equal(g6,g4)
    c: Diameter(g6) = 15
    c: Coincident(g8,g9)
    c: Coincident(g9,g10)
    c: Coincident(g10,g11)
    c: Coincident(g11,g8)
    c: Horizontal(g8)
    c: Horizontal(g10)
    c: Vertical(g9)
    c: Vertical(g11)
FEATURE [PartDesign::Pocket] Pocket006
  BaseFeature = -> Pocket005
  Direction = (0,0,-1)
  Length = 50
  Length2 = 5
  Midplane = true
  Placement = pos=(0,0,0) rot=(1,0,0;1.5708rad)
  Profile = -> Sketch007
  ReferenceAxis = -> Sketch007 [N_Axis]
  TaperAngle = -7
  Type = 0
FEATURE [PartDesign::Chamfer] Chamfer
  Angle = 45
  Base = -> Pocket006 [Edge61,Edge64,Edge79,Edge82,Edge84,Edge83,Edge85,Edge89,Edge86,Edge81,Edge80,Edge96,Edge97,Edge88,Edge77,Edge75,Edge68,Edge67,Edge63,Edge62,Edge65,Edge66,Edge76]
  BaseFeature = -> Pocket006
  ChamferType = 0
  FlipDirection = false
  Placement = pos=(0,0,0) rot=(1,0,0;1.5708rad)
  Size = 1.7
  Size2 = 1
  SupportTransform = false
  UseAllEdges = false
FEATURE [PartDesign::Pocket] Pocket007
  BaseFeature = -> Chamfer
  Direction = (0,0,-1)
  Length = 3
  Length2 = 5
  Placement = pos=(0,0,0) rot=(1,0,0;1.5708rad)
  Profile = -> Sketch004
  ReferenceAxis = -> Sketch004 [N_Axis]
  Reversed = true
  Type = 0
FEATURE [PartDesign::Body] Body
  Group = -> [Sketch,Pad,DatumPlane,Sketch001,Pocket,Sketch002,Pocket001,Sketch003,Pocket002,Sketch004,Sketch005,DatumPlane001,Sketch006,Pocket005,Sketch007,Pocket006,Chamfer,Pocket007]
  Origin = -> Origin
  Tip = -> Pocket007
FEATURE [App::Part] back_base
  Group = -> [LCS_0,Body]
  Origin = -> Origin001
---- part leg1.FCStd = doc fcstd_bf433d822e19 ----
FCSTD DOCUMENT  (FreeCAD 0.21R33668 +7 (Git))
Label: leg1
License: All rights reserved
LicenseURL: http://en.wikipedia.org/wiki/All_rights_reserved
objects: Sketcher::SketchObject×5, PartDesign::Pad×3, PartDesign::CoordinateSystem×1, PartDesign::Body×1, App::Part×1
note: 13 computed .brp shape members not serialized (recipe doc carries the construction recipe); baked Part::Feature solids carry a one-line shape summary decoded from their .brp

FEATURE [Sketcher::SketchObject] Sketch
  FullyConstrained = true
  MapMode = 5
  Support = -> [XY_Plane]
  sketch-geometry (2):
    g0: Circle CenterX=0 CenterY=0 CenterZ=0 NormalX=0 NormalY=0 NormalZ=1 AngleXU=0 Radius=2.25
    g1: Circle CenterX=0 CenterY=0 CenterZ=0 NormalX=0 NormalY=0 NormalZ=1 AngleXU=0 Radius=1.7
  constraints (4):
    c: Coincident(g0,g-1)
    c: Diameter(g0) = 4.5
    c: Coincident(g1,g0)
    c: Diameter(g1) = 3.4
FEATURE [Sketcher::SketchObject] Sketch001
  FullyConstrained = false
  MapMode = 5
  Support = -> [XY_Plane]
  sketch-geometry (6):
    g0: ArcOfCircle CenterX=0 CenterY=0 CenterZ=0 NormalX=0 NormalY=0 NormalZ=1 AngleXU=0 Radius=4.75 StartAngle=2.96706 EndAngle=6.33885
    g1: LineSegment StartX=97.3808 StartY=12.5 StartZ=0 EndX=96.1212 EndY=5.35648 EndZ=0
    g2: LineSegment StartX=96.1212 StartY=5.35648 StartZ=0 EndX=4.74264 EndY=0.26429 EndZ=0
    g3: LineSegment StartX=-4.67784 StartY=0.824829 StartZ=0 EndX=-2.61919 EndY=12.5 EndZ=0
    g4: LineSegment StartX=-2.61919 StartY=12.5 StartZ=0 EndX=97.3808 EndY=12.5 EndZ=0
    g5: Circle CenterX=0 CenterY=0 CenterZ=0 NormalX=0 NormalY=0 NormalZ=1 AngleXU=0 Radius=1.7
  constraints (15):
    c: Coincident(g0,g-1)
    c: Coincident(g1,g2)
    c: Coincident(g0,g2)
    c: Diameter(g0) = 9.5
    c: Coincident(g4,g3)
    c: Coincident(g1,g4)
    c: DistanceY(g3) = 12.5
    c: Tangent(g3,g0) = 1.5708
    c: Angle(g3,g4) = 1.74533
    c: Distance(g4) = 100
    c: Horizontal(g4)
    c: PointOnObject(g0,g2)
    c: Angle(g4,g1) = 1.39626
    c: Coincident(g5,g0)
    c: Diameter(g5) = 3.4
FEATURE [PartDesign::Pad] Pad001
  Direction = (0,0,1)
  Length = 4
  Length2 = 10
  Profile = -> Sketch001
  ReferenceAxis = -> Sketch001 [N_Axis]
  Reversed = true
  Type = 0
FEATURE [PartDesign::CoordinateSystem] LCS_0
  AttacherType = Attacher::AttachEngine3D
  MapMode = 2
  Support = -> [X_Axis001]
FEATURE [Sketcher::SketchObject] Sketch002
  FullyConstrained = true
  MapMode = 5
  Support = -> [XY_Plane]
  sketch-geometry (8):
    g0: ArcOfCircle CenterX=0 CenterY=0 CenterZ=0 NormalX=0 NormalY=0 NormalZ=1 AngleXU=0 Radius=4.75 StartAngle=4.71239 EndAngle=8.08017
    g1: LineSegment StartX=-29.2201 StartY=93.7308 StartZ=0 EndX=-21.5701 EndY=93.7308 EndZ=0
    g2: LineSegment StartX=-21.5701 StartY=93.7308 StartZ=0 EndX=-1.06527 EndY=4.62901 EndZ=0
    g3: LineSegment StartX=-6.5274e-12 StartY=-4.75 StartZ=0 EndX=-11.8553 EndY=-4.75 EndZ=0
    g4: LineSegment StartX=-11.8553 StartY=-4.75 StartZ=0 EndX=-29.2201 EndY=93.7308 EndZ=0
    g5: LineSegment StartX=-12.6928 StartY=0 StartZ=0 EndX=-14.8969 EndY=12.5 EndZ=0
    g6: LineSegment StartX=-14.8969 StartY=12.5 StartZ=0 EndX=-14.8969 EndY=0 EndZ=0
    g7: LineSegment StartX=-14.8969 StartY=0 StartZ=0 EndX=-12.6928 EndY=0 EndZ=0
  constraints (23):
    c: Coincident(g0,g-1)
    c: Coincident(g1,g2)
    c: Coincident(g0,g2)
    c: Diameter(g0) = 9.5
    c: Coincident(g4,g3)
    c: Coincident(g1,g4)
    c: Tangent(g3,g0) = 1.5708
    c: Angle(g3,g4) = 1.74533
    c: Angle(g4,g1) = 1.39626
    c: Distance(g4) = 100
    c: Distance(g1) = 7.65
    c: Distance(g0,g4) = 12.5
    c: Horizontal(g3)
    c: PointOnObject(g5,g4)
    c: PointOnObject(g5,g4)
    c: Coincident(g5,g6)
    c: PointOnObject(g6,g-1)
    c: Vertical(g6)
    c: Coincident(g6,g7)
    c: Coincident(g7,g5)
    c: PointOnObject(g5,g-1)
    c: DistanceY(g5) = 12.5
    c: PointOnObject(g0,g2)
FEATURE [Sketcher::SketchObject] Sketch003
  FullyConstrained = true
  MapMode = 5
  Support = -> [XY_Plane]
  sketch-geometry (1):
    g0: Circle CenterX=0 CenterY=0 CenterZ=0 NormalX=0 NormalY=0 NormalZ=1 AngleXU=0 Radius=4.75
  constraints (2):
    c: Coincident(g0,g-1)
    c: Diameter(g0) = 9.5
FEATURE [Sketcher::SketchObject] Sketch004
  FullyConstrained = false
  MapMode = 5
  Support = -> [XY_Plane]
  sketch-geometry (12):
    g0: LineSegment StartX=14.8968 StartY=12.5 StartZ=0 EndX=97.3637 EndY=12.5 EndZ=0
    g1: LineSegment StartX=96.4669 StartY=7.5 StartZ=0 EndX=14 EndY=7.5 EndZ=0
    g2: LineSegment StartX=0 StartY=0 StartZ=0 EndX=2.1706 EndY=12.3101 EndZ=0
    g3: LineSegment StartX=2.1706 StartY=12.3101 StartZ=0 EndX=14.4807 EndY=10.1395 EndZ=0
    g4: LineSegment StartX=14.4807 StartY=10.1395 StartZ=0 EndX=21.8405 EndY=51.8788 EndZ=0
    g5: LineSegment StartX=14.4807 StartY=10.1395 StartZ=0 EndX=13.1891 EndY=2.81463 EndZ=0
    g6: LineSegment StartX=14 StartY=7.5 StartZ=0 EndX=14.6849 EndY=11.3188 EndZ=0
    g7: LineSegment StartX=14.6849 StartY=11.3188 StartZ=0 EndX=14.8968 EndY=12.5 EndZ=0
    g8: LineSegment StartX=97.3637 StartY=12.5 StartZ=0 EndX=96.8256 EndY=9.5 EndZ=0
    g9: LineSegment StartX=96.8256 StartY=9.5 StartZ=0 EndX=96.4669 EndY=7.5 EndZ=0
    g10: LineSegment StartX=96.8256 StartY=9.5 StartZ=0 EndX=39.9825 EndY=9.5 EndZ=0
    g11: LineSegment StartX=14.6849 StartY=11.3188 StartZ=0 EndX=39.9825 EndY=9.5 EndZ=0
  constraints (30):
    c: Coincident(g0,g8)
    c: Coincident(g9,g1)
    c: Coincident(g1,g6)
    c: Coincident(g7,g0)
    c: Horizontal(g0)
    c: Horizontal(g1)
    c: Distance(g0,g1) = 5
    c: DistanceY(g0) = 12.5
    c: Coincident(g2,g-1)
    c: Distance(g2) = 12.5
    c: Coincident(g3,g2)
    c: Equal(g3,g2)
    c: Angle(g2,g3) = 1.5708
    c: Coincident(g4,g3)
    c: Angle(g4,g3) = 1.5708
    c: Coincident(g5,g3)
    c: Parallel(g5,g4)
    c: Angle(g2,g-2) = 0.174533
    c: DistanceX(g1) = 14
    c: Coincident(g6,g7)
    c: Coincident(g8,g9)
    c: Parallel(g6,g8)
    c: Parallel(g6,g9)
    c: Parallel(g7,g8)
    c: Coincident(g10,g8)
    c: Horizontal(g10)
    c: Coincident(g11,g7)
    c: Coincident(g11,g10)
    c: Distance(g10,g1) = 2
    c: Distance(g7) = 1.2
FEATURE [PartDesign::Pad] Pad003
  BaseFeature = -> Pad001
  Direction = (0,0,1)
  Length = 10
  Length2 = 10
  Profile = -> Sketch004
  ReferenceAxis = -> Sketch004 [N_Axis]
  Type = 0
FEATURE [PartDesign::Pad] Pad
  BaseFeature = -> Pad003
  Direction = (0,0,1)
  Length = 4
  Length2 = 10
  Profile = -> Sketch
  ReferenceAxis = -> Sketch [N_Axis]
  Type = 0
FEATURE [PartDesign::Body] Body
  Group = -> [Sketch,Sketch001,Pad001,Sketch002,Sketch003,Sketch004,Pad003,Pad]
  Origin = -> Origin
  Tip = -> Pad
FEATURE [App::Part] leg1
  Group = -> [LCS_0,Body]
  Origin = -> Origin001
---- part planB.FCStd = doc fcstd_3b57660e1374 (68144 chars; too large to inline — full recipe in that document) ----
---- part side_front_L.FCStd = doc fcstd_5f74e89c0f4a ----
FCSTD DOCUMENT  (FreeCAD 0.21R33668 +7 (Git))
Label: side_front_L
License: All rights reserved
LicenseURL: http://en.wikipedia.org/wiki/All_rights_reserved
objects: Sketcher::SketchObject×9, PartDesign::Pocket×8, PartDesign::Plane×3, PartDesign::Pad×1, PartDesign::CoordinateSystem×1, PartDesign::Body×1, App::Part×1
note: 32 computed .brp shape members not serialized (recipe doc carries the construction recipe); baked Part::Feature solids carry a one-line shape summary decoded from their .brp
EXTERNAL_REF file=planB.FCStd obj=Spreadsheet

FEATURE [Sketcher::SketchObject] Sketch
  FullyConstrained = false
  MapMode = 5
  Support = -> [XY_Plane]
  expr: Constraints[26] = planB#<<data>>.clearance_m4
  sketch-geometry (27):
    g0: LineSegment StartX=75.6 StartY=36 StartZ=0 EndX=75.6 EndY=0 EndZ=0
    g1: LineSegment StartX=75.6 StartY=0 StartZ=0 EndX=134 EndY=0 EndZ=0
    g2: LineSegment StartX=126.5 StartY=107.1 StartZ=0 EndX=-1.5 EndY=107.1 EndZ=0
    g3: LineSegment StartX=-1.5 StartY=107.1 StartZ=0 EndX=-1.5 EndY=104.4 EndZ=0
    g4: LineSegment StartX=-1.5 StartY=104.4 StartZ=0 EndX=-5.7 EndY=104.4 EndZ=0
    g5: LineSegment StartX=-5.7 StartY=104.4 StartZ=0 EndX=-5.7 EndY=102.4 EndZ=0
    g6: LineSegment StartX=-5.7 StartY=102.4 StartZ=0 EndX=0 EndY=102.4 EndZ=0
    g7: Circle CenterX=123.4 CenterY=70.6 CenterZ=0 NormalX=0 NormalY=0 NormalZ=1 AngleXU=0 Radius=2.25
    g8: LineSegment StartX=134 StartY=0 StartZ=0 EndX=134 EndY=36 EndZ=0
    g9: LineSegment StartX=0 StartY=36 StartZ=0 EndX=48.7292 EndY=36 EndZ=0
    g10: LineSegment StartX=48.7292 StartY=36 StartZ=0 EndX=70.6 EndY=36 EndZ=0
    g11: LineSegment StartX=70.6 StartY=36 StartZ=0 EndX=75.6 EndY=36 EndZ=0
    g12: LineSegment StartX=0 StartY=62 StartZ=0 EndX=70.6 EndY=62 EndZ=0
    g13: LineSegment StartX=70.6 StartY=62 StartZ=0 EndX=70.6 EndY=36 EndZ=0
    g14: LineSegment StartX=0 StartY=102.4 StartZ=0 EndX=0 EndY=62 EndZ=0
    g15: LineSegment StartX=0 StartY=62 StartZ=0 EndX=0 EndY=36 EndZ=0
    g16: ArcOfCircle CenterX=126.5 CenterY=99.6 CenterZ=0 NormalX=0 NormalY=0 NormalZ=1 AngleXU=0 Radius=7.5 StartAngle=-9e-16 EndAngle=1.5708
    g17: GeomPoint X=134 Y=107.1 Z=0
    g18: LineSegment StartX=134 StartY=44.7751 StartZ=0 EndX=134 EndY=38.5 EndZ=0
    g19: LineSegment StartX=126.5 StartY=31 StartZ=0 EndX=75.6 EndY=31 EndZ=0
    g20: GeomPoint X=134 Y=31 Z=0
    g21: LineSegment StartX=75.6 StartY=36 StartZ=0 EndX=133.571 EndY=36 EndZ=0
    g22: LineSegment StartX=133.571 StartY=36 StartZ=0 EndX=134 EndY=36 EndZ=0
    g23: ArcOfCircle CenterX=126.5 CenterY=38.5 CenterZ=0 NormalX=0 NormalY=0 NormalZ=1 AngleXU=0 Radius=7.5 StartAngle=4.71239 EndAngle=5.94335
    g24: ArcOfCircle CenterX=126.5 CenterY=38.5 CenterZ=0 NormalX=0 NormalY=0 NormalZ=1 AngleXU=0 Radius=7.5 StartAngle=5.94335 EndAngle=6.28319
    g25: LineSegment StartX=134 StartY=36 StartZ=0 EndX=134 EndY=38.5 EndZ=0
    g26: LineSegment StartX=134 StartY=38.5 StartZ=0 EndX=134 EndY=99.6 EndZ=0
  constraints (72):
    c: PointOnObject(g9,g-2)
    c: Coincident(g11,g0)
    c: PointOnObject(g0,g-1)
    c: Vertical(g0)
    c: Coincident(g0,g1)
    c: PointOnObject(g1,g-1)
    c: Coincident(g1,g8)
    c: Horizontal(g2)
    c: Coincident(g2,g3)
    c: Vertical(g3)
    c: Coincident(g3,g4)
    c: Horizontal(g4)
    c: Coincident(g4,g5)
    c: Vertical(g5)
    c: Coincident(g5,g6)
    c: PointOnObject(g6,g-2)
    c: Horizontal(g6)
    c: Coincident(g6,g14)
    c: Coincident(g15,g9)
    c: Distance(g6) = 5.7
    c: Distance(g5) = 2
    c: Distance(g3) = 2.7
    c: Distance(g0) = 36
    c: DistanceX(g1) = 134
    c: DistanceY(g2) = 107.1
    c: DistanceX(g11) = 75.6
    c: Diameter(g7) = 4.5
    c: DistanceX(g7) = 123.4
    c: DistanceY(g7) = 70.6
    c: Coincident(g21,g11)
    c: Coincident(g8,g25)
    c: Vertical(g8)
    c: Coincident(g8,g22)
    c: Coincident(g9,g10)
    c: Horizontal(g9)
    c: Coincident(g10,g11)
    c: Horizontal(g10)
    c: Horizontal(g11)
    c: Horizontal(g12)
    c: Coincident(g12,g13)
    c: Coincident(g13,g11)
    c: Vertical(g13)
    c: DistanceX(g12) = 70.6
    c: DistanceY(g12) = 62
    c: Coincident(g14,g15)
    c: Coincident(g14,g12)
    c: Distance(g4) = 4.2
    c: Vertical(g14)
    c: PointOnObject(g17,g2)
    c: Tangent(g2,g16) = -1.5708
    c: Tangent(g26,g16) = -1.5708
    c: PointOnObject(g19,g0)
    c: Horizontal(g19)
    c: PointOnObject(g20,g18)
    c: PointOnObject(g20,g19)
    c: Tangent(g18,g24) = 1.5708
    c: Tangent(g19,g23) = 1.5708
    c: Vertical(g18)
    c: Diameter(g16) = 15
    c: Coincident(g21,g22)
    c: Horizontal(g21)
    c: Horizontal(g22)
    c: Distance(g19,g21) = 5
    c: Coincident(g23,g24)
    c: Coincident(g23,g24)
    c: Equal(g23,g16)
    c: Coincident(g25,g26)
    c: Vertical(g25)
    c: Vertical(g26)
    c: PointOnObject(g17,g26)
    c: Coincident(g25,g18)
    c: Coincident(g21,g23)
FEATURE [PartDesign::Pad] Pad
  Direction = (0,0,1)
  Length = 16
  Length2 = 10
  Profile = -> Sketch
  ReferenceAxis = -> Sketch [N_Axis]
  Type = 0
FEATURE [PartDesign::CoordinateSystem] LCS_0
  AttacherType = Attacher::AttachEngine3D
  MapMode = 2
  Support = -> [X_Axis001]
FEATURE [PartDesign::Plane] DatumPlane  label="insideplane"
  AttachmentOffset = pos=(0,0,5) rot=(0,0,1;0rad)
  Length = 187.985
  MapMode = 5
  Placement = pos=(0,0,5) rot=(0,0,1;0rad)
  ResizeMode = 0
  Support = -> [XY_Plane]
  Width = 161.085
FEATURE [Sketcher::SketchObject] Sketch001
  FullyConstrained = false
  MapMode = 5
  Placement = pos=(0,0,5) rot=(0,0,1;0rad)
  Support = -> [DatumPlane]
  expr: Constraints[30] = planB#<<data>>.L_thickness + 0.4 * 2
  expr: Constraints[31] = planB#<<data>>.L_size - planB#<<data>>.L_thickness
  expr: Constraints[32] = planB#<<data>>.L_size + 2 * 0.4
  sketch-geometry (39):
    g0: LineSegment StartX=116.7 StartY=102.3 StartZ=0 EndX=124.3 EndY=102.3 EndZ=0
    g1: LineSegment StartX=116.7 StartY=93.6 StartZ=0 EndX=116.7 EndY=102.3 EndZ=0
    g2: LineSegment StartX=128.6 StartY=101.8 StartZ=0 EndX=131 EndY=101.8 EndZ=0
    g3: LineSegment StartX=131 StartY=101.8 StartZ=0 EndX=131 EndY=79.9 EndZ=0
    g4: LineSegment StartX=131 StartY=79.9 StartZ=0 EndX=120.7 EndY=79.9 EndZ=0
    g5: LineSegment StartX=128.6 StartY=93.9 StartZ=0 EndX=128.6 EndY=101.8 EndZ=0
    g6: LineSegment StartX=80 StartY=41.6 StartZ=0 EndX=80 EndY=5 EndZ=0
    g7: LineSegment StartX=80 StartY=5 StartZ=0 EndX=122 EndY=5 EndZ=0
    g8: LineSegment StartX=120.7 StartY=79.9 StartZ=0 EndX=120.7 EndY=93.6 EndZ=0
    g9: LineSegment StartX=120.7 StartY=93.6 StartZ=0 EndX=120.7 EndY=93.9 EndZ=0
    g10: LineSegment StartX=124.3 StartY=102.3 StartZ=0 EndX=124.3 EndY=93.9 EndZ=0
    g11: LineSegment StartX=124.3 StartY=93.9 StartZ=0 EndX=124.3 EndY=93.6 EndZ=0
    g12: LineSegment StartX=120.7 StartY=93.9 StartZ=0 EndX=124.3 EndY=93.9 EndZ=0
    g13: LineSegment StartX=124.3 StartY=93.9 StartZ=0 EndX=128.6 EndY=93.9 EndZ=0
    g14: LineSegment StartX=124.3 StartY=93.6 StartZ=0 EndX=120.7 EndY=93.6 EndZ=0
    g15: LineSegment StartX=120.7 StartY=93.6 StartZ=0 EndX=116.7 EndY=93.6 EndZ=0
    g16-g20: Circle x5 (B-spline internal-alignment scaffolding for g21; pole/knot coordinates omitted)
    g21: BSplineCurve PolesCount=5 KnotsCount=3 Degree=3 IsPeriodic=0
    g22: GeomPoint X=13.2891 Y=102.5 Z=0
    g23: GeomPoint X=58.9375 Y=89.0501 Z=0
    g24: GeomPoint X=97.4529 Y=102.5 Z=0
    g25: LineSegment StartX=13.2891 StartY=102.5 StartZ=0 EndX=4 EndY=102.5 EndZ=0
    g26: LineSegment StartX=109.7 StartY=102.5 StartZ=0 EndX=98.3319 EndY=102.5 EndZ=0
    g27: LineSegment StartX=98.3319 StartY=102.5 StartZ=0 EndX=13.2891 EndY=102.5 EndZ=0
    g28: LineSegment StartX=109.7 StartY=58 StartZ=0 EndX=109.7 EndY=102.5 EndZ=0
    g29: LineSegment StartX=122 StartY=58 StartZ=0 EndX=109.7 EndY=58 EndZ=0
    g30: LineSegment StartX=122 StartY=5 StartZ=0 EndX=122 EndY=41.6 EndZ=0
    g31: LineSegment StartX=122 StartY=41.6 StartZ=0 EndX=122 EndY=58 EndZ=0
    g32: LineSegment StartX=122 StartY=41.6 StartZ=0 EndX=80 EndY=41.6 EndZ=0
    g33: LineSegment StartX=4 StartY=102.5 StartZ=0 EndX=4 EndY=67 EndZ=0
    g34: LineSegment StartX=4 StartY=67 StartZ=0 EndX=4 EndY=41.6 EndZ=0
    g35: LineSegment StartX=4 StartY=41.6 StartZ=0 EndX=75.6 EndY=41.6 EndZ=0
    g36: LineSegment StartX=75.6 StartY=41.6 StartZ=0 EndX=80 EndY=41.6 EndZ=0
    g37: LineSegment StartX=4 StartY=67 StartZ=0 EndX=75.6 EndY=67 EndZ=0
    g38: LineSegment StartX=75.6 StartY=67 StartZ=0 EndX=75.6 EndY=41.6 EndZ=0
  constraints (93):
    c: Coincident(g0,g10)
    c: Coincident(g11,g14)
    c: Coincident(g15,g1)
    c: Coincident(g1,g0)
    c: Horizontal(g0)
    c: Vertical(g1)
    c: Coincident(g7,g30)
    c: Coincident(g28,g26)
    c: Coincident(g25,g33)
    c: Coincident(g34,g35)
    c: Horizontal(g2)
    c: Coincident(g2,g3)
    c: Vertical(g3)
    c: Coincident(g3,g4)
    c: Horizontal(g4)
    c: Coincident(g4,g8)
    c: Coincident(g9,g12)
    c: Coincident(g13,g5)
    c: Coincident(g5,g2)
    c: Vertical(g5)
    c: Coincident(g36,g6)
    c: Coincident(g6,g7)
    c: Horizontal(g7)
    c: Vertical(g6)
    c: DistanceX(g-2,g25) = 4
    c: DistanceY(g34) = 41.6
    c: DistanceY(g6) = 5
    c: DistanceX(g6) = 80
    c: DistanceY(g0) = 102.3
    c: DistanceY(g11) = 93.6
    c: Distance(g2) = 2.4
    c: Distance(g5) = 7.9
    c: Distance(g4) = 10.3
    c: DistanceX(g13) = 128.6
    c: Coincident(g8,g9)
    c: Vertical(g8)
    c: Vertical(g9)
    c: Distance(g8,g9) = 14
    c: Coincident(g10,g11)
    c: Vertical(g10)
    c: Vertical(g11)
    c: Coincident(g12,g13)
    c: Horizontal(g12)
    c: Horizontal(g13)
    c: Coincident(g10,g12)
    c: Coincident(g14,g15)
    c: Horizontal(g14)
    c: Horizontal(g15)
    c: Distance(g9,g14) = 0.3
    c: Coincident(g14,g8)
    c: DistanceX(g0) = 124.3
    c: DistanceX(g0) = 116.7
    c: DistanceY(g25) = 102.5
    c: Weight(g16) = 1
    c: Equal(g16, g17-g20) x4
    c: InternalAlignment(g16-g20 -> g21) x5
    c: InternalAlignment(g22,g21)
    c: InternalAlignment(g23,g21)
    c: Coincident(g27,g25)
    c: Horizontal(g25)
    c: PointOnObject(g17,g25)
    c: Coincident(g26,g27)
    c: Horizontal(g26)
    c: Horizontal(g27)
    c: PointOnObject(g19,g26)
    c: Coincident(g21,g25)
    c: Coincident(g26,g21)
    c: Coincident(g29,g28)
    c: Vertical(g28)
    c: Distance(g1,g28) = 7
    c: Coincident(g31,g29)
    c: Horizontal(g29)
    c: DistanceX(g31) = 122
    c: DistanceY(g28) = 58
    c: Coincident(g30,g31)
    c: Vertical(g30)
    c: Vertical(g31)
    c: Coincident(g32,g31)
    c: Coincident(g32,g36)
    c: Horizontal(g32)
    c: Coincident(g33,g34)
    c: Vertical(g33)
    c: Vertical(g34)
    c: Coincident(g35,g36)
    c: Horizontal(g35)
    c: Horizontal(g36)
    c: Coincident(g33,g37)
    c: Horizontal(g37)
    c: Coincident(g37,g38)
    c: Coincident(g38,g36)
    c: Vertical(g38)
    c: DistanceX(g37) = 75.6
    c: DistanceY(g37) = 67
FEATURE [PartDesign::Pocket] Pocket
  BaseFeature = -> Pad
  Direction = (0,0,-1)
  Length = 21
  Length2 = 5
  Profile = -> Sketch001
  ReferenceAxis = -> Sketch001 [N_Axis]
  Reversed = true
  Type = 0
FEATURE [Sketcher::SketchObject] Sketch002
  FullyConstrained = false
  MapMode = 5
  Placement = pos=(0,0,0) rot=(0.57735,0.57735,0.57735;2.0944rad)
  Support = -> [YZ_Plane]
  expr: Constraints[0] = planB#<<data>>.clearance_m3
  sketch-geometry (4):
    g0: Circle CenterX=12 CenterY=8 CenterZ=0 NormalX=0 NormalY=0 NormalZ=1 AngleXU=0 Radius=1.75
    g1: LineSegment StartX=12 StartY=8 StartZ=0 EndX=134.137 EndY=8 EndZ=0
    g2: Circle CenterX=60 CenterY=8 CenterZ=0 NormalX=0 NormalY=0 NormalZ=1 AngleXU=0 Radius=1.75
    g3: Circle CenterX=90 CenterY=8 CenterZ=0 NormalX=0 NormalY=0 NormalZ=1 AngleXU=0 Radius=1.75
  constraints (11):
    c: Diameter(g0) = 3.5
    c: DistanceY(g0) = 8
    c: DistanceX(g0) = 12
    c: Coincident(g1,g0)
    c: Horizontal(g1)
    c: PointOnObject(g2,g1)
    c: PointOnObject(g3,g1)
    c: Equal(g0,g2)
    c: Equal(g2,g3)
    c: DistanceX(g2) = 60
    c: DistanceX(g3) = 90
FEATURE [PartDesign::Pocket] Pocket001
  BaseFeature = -> Pocket
  Direction = (-1,2e-16,-3e-16)
  Length = 23
  Length2 = 5
  Profile = -> Sketch002
  ReferenceAxis = -> Sketch002 [N_Axis]
  Reversed = true
  Type = 0
FEATURE [Sketcher::SketchObject] Sketch003
  FullyConstrained = true
  MapMode = 5
  Placement = pos=(0,0,0) rot=(1,0,0;1.5708rad)
  Support = -> [XZ_Plane]
  expr: Constraints[5] = planB#<<data>>.clearance_m3
  expr: Constraints[9] = planB#<<data>>.insert_diameter
  sketch-geometry (4):
    g0: Circle CenterX=58.6 CenterY=8 CenterZ=0 NormalX=0 NormalY=0 NormalZ=1 AngleXU=0 Radius=1.75
    g1: Circle CenterX=8 CenterY=8 CenterZ=0 NormalX=0 NormalY=0 NormalZ=1 AngleXU=0 Radius=1.75
    g2: LineSegment StartX=58.6 StartY=8 StartZ=0 EndX=8 EndY=8 EndZ=0
    g3: Circle CenterX=125 CenterY=8 CenterZ=0 NormalX=0 NormalY=0 NormalZ=1 AngleXU=0 Radius=2.15
  constraints (11):
    c: Coincident(g2,g0)
    c: Coincident(g2,g1)
    c: Horizontal(g2)
    c: DistanceY(g1) = 8
    c: Equal(g1,g0)
    c: Diameter(g0) = 3.5
    c: DistanceX(g-2,g1) = 8
    c: DistanceX(g0) = 58.6
    c: PointOnObject(g3,g2)
    c: Diameter(g3) = 4.3
    c: DistanceX(g3) = 125
FEATURE [PartDesign::Pocket] Pocket002
  BaseFeature = -> Pocket001
  Direction = (0,1,2e-16)
  Length = 46
  Length2 = 5
  Profile = -> Sketch003
  ReferenceAxis = -> Sketch003 [N_Axis]
  Type = 0
FEATURE [PartDesign::Plane] DatumPlane001
  AttachmentOffset = pos=(0,0,107) rot=(0,0,1;0rad)
  Length = 148.354
  MapMode = 5
  Placement = pos=(107,-2.38e-14,2.38e-14) rot=(0.57735,0.57735,0.57735;2.0944rad)
  ResizeMode = 0
  Support = -> [YZ_Plane]
  Width = 66.2542
FEATURE [Sketcher::SketchObject] Sketch005
  FullyConstrained = true
  MapMode = 5
  Placement = pos=(0,0,5) rot=(0,0,1;0rad)
  Support = -> [DatumPlane]
  sketch-geometry (1):
    g0: Circle CenterX=123.4 CenterY=70.6 CenterZ=0 NormalX=0 NormalY=0 NormalZ=1 AngleXU=0 Radius=8
  constraints (3):
    c: DistanceX(g0) = 123.4
    c: DistanceY(g0) = 70.6
    c: Diameter(g0) = 16
FEATURE [PartDesign::Pocket] Pocket004
  BaseFeature = -> Pocket002
  Direction = (0,0,-1)
  Length = 10
  Length2 = 5
  Midplane = true
  Profile = -> Sketch005
  ReferenceAxis = -> Sketch005 [N_Axis]
  Type = 0
FEATURE [Sketcher::SketchObject] Sketch007
  FullyConstrained = true
  MapMode = 5
  Placement = pos=(0,0,5) rot=(0,0,1;0rad)
  Support = -> [DatumPlane]
  sketch-geometry (4):
    g0: LineSegment StartX=131 StartY=101.8 StartZ=0 EndX=120.5 EndY=101.8 EndZ=0
    g1: LineSegment StartX=120.5 StartY=101.8 StartZ=0 EndX=120.5 EndY=80.8 EndZ=0
    g2: LineSegment StartX=120.5 StartY=80.8 StartZ=0 EndX=131 EndY=80.8 EndZ=0
    g3: LineSegment StartX=131 StartY=80.8 StartZ=0 EndX=131 EndY=101.8 EndZ=0
  constraints (12):
    c: Coincident(g0,g1)
    c: Coincident(g1,g2)
    c: Coincident(g2,g3)
    c: Coincident(g3,g0)
    c: Horizontal(g0)
    c: Horizontal(g2)
    c: Vertical(g1)
    c: Vertical(g3)
    c: Distance(g2) = 10.5
    c: Distance(g3) = 21
    c: DistanceY(g0) = 101.8
    c: DistanceX(g0) = 131
FEATURE [Sketcher::SketchObject] Sketch008
  FullyConstrained = false
  MapMode = 5
  Placement = pos=(0,0,5) rot=(0,0,1;0rad)
  Support = -> [DatumPlane]
  sketch-geometry (6):
    g0: LineSegment StartX=127.329 StartY=102.8 StartZ=0 EndX=132 EndY=102.8 EndZ=0
    g1: LineSegment StartX=132 StartY=102.8 StartZ=0 EndX=132 EndY=79.4945 EndZ=0
    g2: LineSegment StartX=132 StartY=79.4945 StartZ=0 EndX=119.5 EndY=79.4945 EndZ=0
    g3: LineSegment StartX=119.5 StartY=79.4945 StartZ=0 EndX=119.5 EndY=94.9604 EndZ=0
    g4: LineSegment StartX=119.5 StartY=94.9604 StartZ=0 EndX=127.329 EndY=94.9604 EndZ=0
    g5: LineSegment StartX=127.329 StartY=94.9604 StartZ=0 EndX=127.329 EndY=102.8 EndZ=0
  constraints (15):
    c: Coincident(g0,g1)
    c: Vertical(g1)
    c: Coincident(g1,g2)
    c: Horizontal(g2)
    c: Coincident(g2,g3)
    c: Vertical(g3)
    c: Coincident(g3,g4)
    c: Horizontal(g4)
    c: Coincident(g4,g5)
    c: Coincident(g5,g0)
    c: Vertical(g5)
    c: Horizontal(g0)
    c: DistanceX(g0) = 132
    c: DistanceY(g0) = 102.8
    c: DistanceX(g2) = 119.5
FEATURE [PartDesign::Plane] DatumPlane002  label="oppoplane"
  AttachmentOffset = pos=(0,0,16) rot=(0,0,1;0rad)
  Length = 187.985
  MapMode = 5
  Placement = pos=(0,0,16) rot=(0,0,1;0rad)
  ResizeMode = 0
  Support = -> [XY_Plane]
  Width = 161.085
FEATURE [Sketcher::SketchObject] Sketch006
  FullyConstrained = false
  MapMode = 5
  Placement = pos=(0,0,16) rot=(0,0,1;0rad)
  Support = -> [DatumPlane002]
  sketch-geometry (6):
    g0: LineSegment StartX=116.7 StartY=102.3 StartZ=0 EndX=124.3 EndY=102.3 EndZ=0
    g1: LineSegment StartX=116.7 StartY=93.6 StartZ=0 EndX=116.7 EndY=102.3 EndZ=0
    g2: LineSegment StartX=124.3 StartY=102.3 StartZ=0 EndX=124.3 EndY=93.9 EndZ=0
    g3: LineSegment StartX=124.3 StartY=93.9 StartZ=0 EndX=124.3 EndY=93.6 EndZ=0
    g4: LineSegment StartX=124.3 StartY=93.6 StartZ=0 EndX=120.7 EndY=93.6 EndZ=0
    g5: LineSegment StartX=120.7 StartY=93.6 StartZ=0 EndX=116.7 EndY=93.6 EndZ=0
  constraints (16):
    c: Horizontal(g0)
    c: Vertical(g1)
    c: DistanceY(g0) = 102.3
    c: DistanceY(g3) = 93.6
    c: Vertical(g2)
    c: Vertical(g3)
    c: Horizontal(g4)
    c: Horizontal(g5)
    c: DistanceX(g0) = 124.3
    c: DistanceX(g0) = 116.7
    c: Coincident(g0,g1)
    c: Coincident(g0,g2)
    c: Coincident(g3,g4)
    c: Coincident(g2,g3)
    c: Coincident(g4,g5)
    c: Coincident(g1,g5)
FEATURE [PartDesign::Pocket] Pocket005
  BaseFeature = -> Pocket004
  Direction = (0,0,-1)
  Length = 4.4
  Length2 = 5
  Profile = -> Sketch006
  ReferenceAxis = -> Sketch006 [N_Axis]
  Type = 0
FEATURE [PartDesign::Pocket] Pocket006
  BaseFeature = -> Pocket005
  Direction = (0,0,-1)
  Length = 6
  Length2 = 5
  Profile = -> Sketch007
  ReferenceAxis = -> Sketch007 [N_Axis]
  Type = 0
FEATURE [Sketcher::SketchObject] Sketch009
  FullyConstrained = false
  MapMode = 5
  Placement = pos=(0,0,0) rot=(1,0,0;1.5708rad)
  Support = -> [XZ_Plane]
  expr: Constraints[5] = planB#<<data>>.clearance_m3
  expr: Constraints[9] = planB#<<data>>.insert_diameter
  sketch-geometry (8):
    g0: Circle CenterX=58.6 CenterY=8 CenterZ=0 NormalX=0 NormalY=0 NormalZ=1 AngleXU=0 Radius=1.75
    g1: Circle CenterX=8 CenterY=8 CenterZ=0 NormalX=0 NormalY=0 NormalZ=1 AngleXU=0 Radius=1.75
    g2: LineSegment StartX=58.6 StartY=8 StartZ=0 EndX=8 EndY=8 EndZ=0
    g3: Circle CenterX=125 CenterY=8 CenterZ=0 NormalX=0 NormalY=0 NormalZ=1 AngleXU=0 Radius=2.15
    g4: ArcOfCircle CenterX=38 CenterY=16 CenterZ=0 NormalX=0 NormalY=0 NormalZ=1 AngleXU=0 Radius=5 StartAngle=3.14159 EndAngle=6.28319
    g5: ArcOfCircle CenterX=38 CenterY=31.6735 CenterZ=0 NormalX=0 NormalY=0 NormalZ=1 AngleXU=0 Radius=5 StartAngle=2e-16 EndAngle=3.14159
    g6: LineSegment StartX=43 StartY=16 StartZ=0 EndX=43 EndY=31.6735 EndZ=0
    g7: LineSegment StartX=33 StartY=31.6735 StartZ=0 EndX=33 EndY=16 EndZ=0
  constraints (20):
    c: Coincident(g2,g0)
    c: Coincident(g2,g1)
    c: Horizontal(g2)
    c: DistanceY(g1) = 8
    c: Equal(g1,g0)
    c: Diameter(g0) = 3.5
    c: DistanceX(g-2,g1) = 8
    c: DistanceX(g0) = 58.6
    c: PointOnObject(g3,g2)
    c: Diameter(g3) = 4.3
    c: DistanceX(g3) = 125
    c: Tangent(g4,g6) = -1.5708
    c: Tangent(g6,g5) = -1.5708
    c: Tangent(g5,g7) = -1.5708
    c: Tangent(g7,g4) = -1.5708
    c: Equal(g4,g5)
    c: Vertical(g6)
    c: DistanceX(g4) = 38
    c: DistanceY(g4) = 16
    c: Diameter(g4) = 10
FEATURE [PartDesign::Pocket] Pocket007
  BaseFeature = -> Pocket006
  Direction = (0,0,-1)
  Length = 18
  Length2 = 5
  Profile = -> Sketch008
  ReferenceAxis = -> Sketch008 [N_Axis]
  Reversed = true
  Type = 0
FEATURE [PartDesign::Pocket] Pocket008
  BaseFeature = -> Pocket007
  Direction = (0,1,2e-16)
  Length = 86
  Length2 = 5
  Profile = -> Sketch009
  ReferenceAxis = -> Sketch009 [N_Axis]
  Type = 0
FEATURE [PartDesign::Body] Body
  Group = -> [Sketch,Pad,DatumPlane,Sketch001,Pocket,Sketch002,Pocket001,Sketch003,Pocket002,DatumPlane001,Sketch005,Pocket004,Sketch006,Pocket005,Sketch007,Pocket006,Sketch008,Pocket007,DatumPlane002,Sketch009,Pocket008]
  Origin = -> Origin
  Tip = -> Pocket008
FEATURE [App::Part] side_front_L  label="side_front_R"
  Group = -> [LCS_0,Body]
  Origin = -> Origin001
---- part side_front_R.FCStd = doc fcstd_70ea38e8b0e3 ----
FCSTD DOCUMENT  (FreeCAD 0.21R33668 +7 (Git))
Label: side_front_R
License: All rights reserved
LicenseURL: http://en.wikipedia.org/wiki/All_rights_reserved
objects: Sketcher::SketchObject×8, PartDesign::Pocket×7, PartDesign::Plane×2, PartDesign::Pad×1, PartDesign::CoordinateSystem×1, PartDesign::Body×1, App::Part×1
note: 28 computed .brp shape members not serialized (recipe doc carries the construction recipe); baked Part::Feature solids carry a one-line shape summary decoded from their .brp
EXTERNAL_REF file=planB.FCStd obj=Spreadsheet

FEATURE [Sketcher::SketchObject] Sketch
  FullyConstrained = false
  MapMode = 5
  Support = -> [XY_Plane]
  expr: Constraints[26] = planB#<<data>>.clearance_m4
  sketch-geometry (21):
    g0: LineSegment StartX=0 StartY=36 StartZ=0 EndX=75.6 EndY=36 EndZ=0
    g1: LineSegment StartX=75.6 StartY=36 StartZ=0 EndX=75.6 EndY=0 EndZ=0
    g2: LineSegment StartX=75.6 StartY=0 StartZ=0 EndX=134 EndY=0 EndZ=0
    g3: LineSegment StartX=126.5 StartY=107 StartZ=0 EndX=-1.5 EndY=107 EndZ=0
    g4: LineSegment StartX=-1.5 StartY=107 StartZ=0 EndX=-1.5 EndY=104.3 EndZ=0
    g5: LineSegment StartX=-1.5 StartY=104.3 StartZ=0 EndX=-5.7 EndY=104.3 EndZ=0
    g6: LineSegment StartX=-5.7 StartY=104.3 StartZ=0 EndX=-5.7 EndY=102.3 EndZ=0
    g7: LineSegment StartX=-5.7 StartY=102.3 StartZ=0 EndX=0 EndY=102.3 EndZ=0
    g8: LineSegment StartX=0 StartY=102.3 StartZ=0 EndX=0 EndY=36 EndZ=0
    g9: Circle CenterX=123.4 CenterY=70.6 CenterZ=0 NormalX=0 NormalY=0 NormalZ=1 AngleXU=0 Radius=2.25
    g10: LineSegment StartX=134 StartY=38.5 StartZ=0 EndX=134 EndY=36 EndZ=0
    g11: ArcOfCircle CenterX=126.5 CenterY=99.5 CenterZ=0 NormalX=0 NormalY=0 NormalZ=1 AngleXU=0 Radius=7.5 StartAngle=0 EndAngle=1.5708
    g12: GeomPoint X=134 Y=107 Z=0
    g13: LineSegment StartX=134 StartY=44.7645 StartZ=0 EndX=134 EndY=31 EndZ=0
    g14: LineSegment StartX=126.5 StartY=31 StartZ=0 EndX=75.6 EndY=31 EndZ=0
    g15: ArcOfCircle CenterX=126.5 CenterY=38.5 CenterZ=0 NormalX=0 NormalY=0 NormalZ=1 AngleXU=0 Radius=7.5 StartAngle=4.71239 EndAngle=5.94335
    g16: ArcOfCircle CenterX=126.5 CenterY=38.5 CenterZ=0 NormalX=0 NormalY=0 NormalZ=1 AngleXU=0 Radius=7.5 StartAngle=5.94335 EndAngle=6.28319
    g17: LineSegment StartX=75.6 StartY=36 StartZ=0 EndX=133.571 EndY=36 EndZ=0
    g18: LineSegment StartX=133.571 StartY=36 StartZ=0 EndX=134 EndY=36 EndZ=0
    g19: LineSegment StartX=134 StartY=36 StartZ=0 EndX=134 EndY=38.5 EndZ=0
    g20: LineSegment StartX=134 StartY=38.5 StartZ=0 EndX=134 EndY=99.5 EndZ=0
  constraints (58):
    c: PointOnObject(g0,g-2)
    c: Horizontal(g0)
    c: Coincident(g0,g1)
    c: PointOnObject(g1,g-1)
    c: Vertical(g1)
    c: Coincident(g1,g2)
    c: PointOnObject(g2,g-1)
    c: Horizontal(g3)
    c: Coincident(g3,g4)
    c: Vertical(g4)
    c: Coincident(g4,g5)
    c: Horizontal(g5)
    c: Coincident(g5,g6)
    c: Vertical(g6)
    c: Coincident(g6,g7)
    c: PointOnObject(g7,g-2)
    c: Horizontal(g7)
    c: Coincident(g7,g8)
    c: Coincident(g8,g0)
    c: Distance(g7) = 5.7
    c: Distance(g6) = 2
    c: Distance(g4) = 2.7
    c: Distance(g1) = 36
    c: DistanceX(g2) = 134
    c: DistanceY(g3) = 107
    c: DistanceX(g0) = 75.6
    c: Diameter(g9) = 4.5
    c: DistanceX(g9) = 123.4
    c: DistanceY(g9) = 70.6
    c: Coincident(g17,g0)
    c: Coincident(g10,g19)
    c: Vertical(g10)
    c: Coincident(g10,g18)
    c: PointOnObject(g12,g3)
    c: Tangent(g3,g11) = -1.5708
    c: Tangent(g20,g11) = -1.5708
    c: PointOnObject(g13,g10)
    c: PointOnObject(g14,g1)
    c: Horizontal(g14)
    c: Tangent(g14,g15) = 1.5708
    c: Tangent(g10,g16) = 1.5708
    c: Diameter(g11) = 15
    c: PointOnObject(g2,g13)
    c: Coincident(g15,g16)
    c: Coincident(g15,g16)
    c: Equal(g15,g11)
    c: Coincident(g17,g18)
    c: Horizontal(g17)
    c: Horizontal(g18)
    c: Distance(g13,g18) = 5
    c: Distance(g14,g17) = 5
    c: Coincident(g15,g17)
    c: Coincident(g19,g20)
    c: Vertical(g20)
    c: PointOnObject(g12,g20)
    c: PointOnObject(g13,g20)
    c: Coincident(g19,g16)
    c: DistanceX(g5,g5) = 4.2
FEATURE [PartDesign::Pad] Pad
  Direction = (0,0,1)
  Length = 16
  Length2 = 10
  Profile = -> Sketch
  ReferenceAxis = -> Sketch [N_Axis]
  Type = 0
FEATURE [PartDesign::CoordinateSystem] LCS_0
  AttacherType = Attacher::AttachEngine3D
  MapMode = 2
  Support = -> [X_Axis001]
FEATURE [PartDesign::Plane] DatumPlane
  AttachmentOffset = pos=(0,0,11) rot=(0,0,1;0rad)
  Length = 60
  MapMode = 5
  Placement = pos=(0,0,11) rot=(0,0,1;0rad)
  ResizeMode = 0
  Support = -> [XY_Plane]
  Width = 60
FEATURE [Sketcher::SketchObject] Sketch001
  FullyConstrained = false
  MapMode = 5
  Placement = pos=(0,0,11) rot=(0,0,1;0rad)
  Support = -> [DatumPlane]
  expr: Constraints[32] = planB#<<data>>.L_thickness + 0.4 * 2
  expr: Constraints[33] = planB#<<data>>.L_size - planB#<<data>>.L_thickness
  expr: Constraints[34] = planB#<<data>>.L_size + 2 * 0.4
  sketch-geometry (35):
    g0: LineSegment StartX=116.7 StartY=102.3 StartZ=0 EndX=124.3 EndY=102.3 EndZ=0
    g1: LineSegment StartX=116.7 StartY=93.6 StartZ=0 EndX=116.7 EndY=102.3 EndZ=0
    g2: LineSegment StartX=4 StartY=102.5 StartZ=0 EndX=4 EndY=41.6 EndZ=0
    g3: LineSegment StartX=128.6 StartY=101.8 StartZ=0 EndX=131 EndY=101.8 EndZ=0
    g4: LineSegment StartX=131 StartY=101.8 StartZ=0 EndX=131 EndY=79.9 EndZ=0
    g5: LineSegment StartX=131 StartY=79.9 StartZ=0 EndX=120.7 EndY=79.9 EndZ=0
    g6: LineSegment StartX=128.6 StartY=93.9 StartZ=0 EndX=128.6 EndY=101.8 EndZ=0
    g7: LineSegment StartX=4 StartY=41.6 StartZ=0 EndX=80 EndY=41.6 EndZ=0
    g8: LineSegment StartX=80 StartY=41.6 StartZ=0 EndX=80 EndY=5 EndZ=0
    g9: LineSegment StartX=80 StartY=5 StartZ=0 EndX=122 EndY=5 EndZ=0
    g10: LineSegment StartX=120.7 StartY=79.9 StartZ=0 EndX=120.7 EndY=93.6 EndZ=0
    g11: LineSegment StartX=120.7 StartY=93.6 StartZ=0 EndX=120.7 EndY=93.9 EndZ=0
    g12: LineSegment StartX=124.3 StartY=102.3 StartZ=0 EndX=124.3 EndY=93.9 EndZ=0
    g13: LineSegment StartX=124.3 StartY=93.9 StartZ=0 EndX=124.3 EndY=93.6 EndZ=0
    g14: LineSegment StartX=120.7 StartY=93.9 StartZ=0 EndX=124.3 EndY=93.9 EndZ=0
    g15: LineSegment StartX=124.3 StartY=93.9 StartZ=0 EndX=128.6 EndY=93.9 EndZ=0
    g16: LineSegment StartX=124.3 StartY=93.6 StartZ=0 EndX=120.7 EndY=93.6 EndZ=0
    g17: LineSegment StartX=120.7 StartY=93.6 StartZ=0 EndX=116.7 EndY=93.6 EndZ=0
    g18-g22: Circle x5 (B-spline internal-alignment scaffolding for g23; pole/knot coordinates omitted)
    g23: BSplineCurve PolesCount=5 KnotsCount=3 Degree=3 IsPeriodic=0
    g24: GeomPoint X=13.2891 Y=102.5 Z=0
    g25: GeomPoint X=58.9375 Y=89.0501 Z=0
    g26: GeomPoint X=97.4529 Y=102.5 Z=0
    g27: LineSegment StartX=13.2891 StartY=102.5 StartZ=0 EndX=4 EndY=102.5 EndZ=0
    g28: LineSegment StartX=109.7 StartY=102.5 StartZ=0 EndX=98.3319 EndY=102.5 EndZ=0
    g29: LineSegment StartX=98.3319 StartY=102.5 StartZ=0 EndX=13.2891 EndY=102.5 EndZ=0
    g30: LineSegment StartX=109.7 StartY=58 StartZ=0 EndX=109.7 EndY=102.5 EndZ=0
    g31: LineSegment StartX=122 StartY=58 StartZ=0 EndX=109.7 EndY=58 EndZ=0
    g32: LineSegment StartX=122 StartY=5 StartZ=0 EndX=122 EndY=41.6 EndZ=0
    g33: LineSegment StartX=122 StartY=41.6 StartZ=0 EndX=122 EndY=58 EndZ=0
    g34: LineSegment StartX=122 StartY=41.6 StartZ=0 EndX=80 EndY=41.6 EndZ=0
  constraints (82):
    c: Coincident(g0,g12)
    c: Coincident(g13,g16)
    c: Coincident(g17,g1)
    c: Coincident(g1,g0)
    c: Horizontal(g0)
    c: Vertical(g1)
    c: Coincident(g9,g32)
    c: Coincident(g30,g28)
    c: Coincident(g27,g2)
    c: Coincident(g2,g7)
    c: Vertical(g2)
    c: Horizontal(g3)
    c: Coincident(g3,g4)
    c: Vertical(g4)
    c: Coincident(g4,g5)
    c: Horizontal(g5)
    c: Coincident(g5,g10)
    c: Coincident(g11,g14)
    c: Coincident(g15,g6)
    c: Coincident(g6,g3)
    c: Vertical(g6)
    c: Coincident(g7,g8)
    c: Horizontal(g7)
    c: Coincident(g8,g9)
    c: Horizontal(g9)
    c: Vertical(g8)
    c: DistanceX(g-2,g27) = 4
    c: DistanceY(g2) = 41.6
    c: DistanceY(g8) = 5
    c: DistanceX(g8) = 80
    c: DistanceY(g0) = 102.3
    c: DistanceY(g13) = 93.6
    c: Distance(g3) = 2.4
    c: Distance(g6) = 7.9
    c: Distance(g5) = 10.3
    c: DistanceX(g15) = 128.6
    c: Coincident(g10,g11)
    c: Vertical(g10)
    c: Vertical(g11)
    c: Distance(g10,g11) = 14
    c: Coincident(g12,g13)
    c: Vertical(g12)
    c: Vertical(g13)
    c: Coincident(g14,g15)
    c: Horizontal(g14)
    c: Horizontal(g15)
    c: Coincident(g12,g14)
    c: Coincident(g16,g17)
    c: Horizontal(g16)
    c: Horizontal(g17)
    c: Distance(g11,g16) = 0.3
    c: Coincident(g16,g10)
    c: DistanceX(g0) = 124.3
    c: DistanceX(g0) = 116.7
    c: DistanceY(g27) = 102.5
    c: Weight(g18) = 1
    c: Equal(g18, g19-g22) x4
    c: InternalAlignment(g18-g22 -> g23) x5
    c: InternalAlignment(g24,g23)
    c: InternalAlignment(g25,g23)
    c: Coincident(g29,g27)
    c: Horizontal(g27)
    c: PointOnObject(g19,g27)
    c: Coincident(g28,g29)
    c: Horizontal(g28)
    c: Horizontal(g29)
    c: PointOnObject(g21,g28)
    c: Coincident(g23,g27)
    c: Coincident(g28,g23)
    c: Coincident(g31,g30)
    c: Vertical(g30)
    c: Distance(g1,g30) = 7
    c: Coincident(g33,g31)
    c: Horizontal(g31)
    c: DistanceX(g33) = 122
    c: DistanceY(g30) = 58
    c: Coincident(g32,g33)
    c: Vertical(g32)
    c: Vertical(g33)
    c: Coincident(g34,g33)
    c: Coincident(g34,g7)
    c: Horizontal(g34)
FEATURE [PartDesign::Pocket] Pocket
  BaseFeature = -> Pad
  Direction = (0,0,-1)
  Length = 21
  Length2 = 5
  Profile = -> Sketch001
  ReferenceAxis = -> Sketch001 [N_Axis]
  Type = 0
FEATURE [Sketcher::SketchObject] Sketch002
  FullyConstrained = false
  MapMode = 5
  Placement = pos=(0,0,0) rot=(0.57735,0.57735,0.57735;2.0944rad)
  Support = -> [YZ_Plane]
  expr: Constraints[0] = planB#<<data>>.clearance_m3
  sketch-geometry (4):
    g0: Circle CenterX=12 CenterY=8 CenterZ=0 NormalX=0 NormalY=0 NormalZ=1 AngleXU=0 Radius=1.75
    g1: LineSegment StartX=12 StartY=8 StartZ=0 EndX=134.137 EndY=8 EndZ=0
    g2: Circle CenterX=60 CenterY=8 CenterZ=0 NormalX=0 NormalY=0 NormalZ=1 AngleXU=0 Radius=1.75
    g3: Circle CenterX=90 CenterY=8 CenterZ=0 NormalX=0 NormalY=0 NormalZ=1 AngleXU=0 Radius=1.75
  constraints (11):
    c: Diameter(g0) = 3.5
    c: DistanceY(g0) = 8
    c: DistanceX(g0) = 12
    c: Coincident(g1,g0)
    c: Horizontal(g1)
    c: PointOnObject(g2,g1)
    c: PointOnObject(g3,g1)
    c: Equal(g0,g2)
    c: Equal(g2,g3)
    c: DistanceX(g2) = 60
    c: DistanceX(g3) = 90
FEATURE [PartDesign::Pocket] Pocket001
  BaseFeature = -> Pocket
  Direction = (-1,2e-16,-3e-16)
  Length = 23
  Length2 = 5
  Profile = -> Sketch002
  ReferenceAxis = -> Sketch002 [N_Axis]
  Reversed = true
  Type = 0
FEATURE [Sketcher::SketchObject] Sketch003
  FullyConstrained = true
  MapMode = 5
  Placement = pos=(0,0,0) rot=(1,0,0;1.5708rad)
  Support = -> [XZ_Plane]
  expr: Constraints[5] = planB#<<data>>.clearance_m3
  expr: Constraints[9] = planB#<<data>>.insert_diameter
  sketch-geometry (4):
    g0: Circle CenterX=58.6 CenterY=8 CenterZ=0 NormalX=0 NormalY=0 NormalZ=1 AngleXU=0 Radius=1.75
    g1: Circle CenterX=8 CenterY=8 CenterZ=0 NormalX=0 NormalY=0 NormalZ=1 AngleXU=0 Radius=1.75
    g2: LineSegment StartX=58.6 StartY=8 StartZ=0 EndX=8 EndY=8 EndZ=0
    g3: Circle CenterX=125 CenterY=8 CenterZ=0 NormalX=0 NormalY=0 NormalZ=1 AngleXU=0 Radius=2.15
  constraints (11):
    c: Coincident(g2,g0)
    c: Coincident(g2,g1)
    c: Horizontal(g2)
    c: DistanceY(g1) = 8
    c: Equal(g1,g0)
    c: Diameter(g0) = 3.5
    c: DistanceX(g-2,g1) = 8
    c: DistanceX(g0) = 58.6
    c: PointOnObject(g3,g2)
    c: Diameter(g3) = 4.3
    c: DistanceX(g3) = 125
FEATURE [PartDesign::Pocket] Pocket002
  BaseFeature = -> Pocket001
  Direction = (0,1,2e-16)
  Length = 46
  Length2 = 5
  Profile = -> Sketch003
  ReferenceAxis = -> Sketch003 [N_Axis]
  Type = 0
FEATURE [PartDesign::Plane] DatumPlane001
  AttachmentOffset = pos=(0,0,107) rot=(0,0,1;0rad)
  Length = 60
  MapMode = 5
  Placement = pos=(107,-2.38e-14,2.38e-14) rot=(0.57735,0.57735,0.57735;2.0944rad)
  ResizeMode = 0
  Support = -> [YZ_Plane]
  Width = 60
FEATURE [Sketcher::SketchObject] Sketch005
  FullyConstrained = true
  MapMode = 5
  Placement = pos=(0,0,11) rot=(0,0,1;0rad)
  Support = -> [DatumPlane]
  sketch-geometry (1):
    g0: Circle CenterX=123.4 CenterY=70.6 CenterZ=0 NormalX=0 NormalY=0 NormalZ=1 AngleXU=0 Radius=8
  constraints (3):
    c: DistanceX(g0) = 123.4
    c: DistanceY(g0) = 70.6
    c: Diameter(g0) = 16
FEATURE [PartDesign::Pocket] Pocket004
  BaseFeature = -> Pocket002
  Direction = (0,0,-1)
  Length = 10
  Length2 = 5
  Midplane = true
  Profile = -> Sketch005
  ReferenceAxis = -> Sketch005 [N_Axis]
  Type = 0
FEATURE [Sketcher::SketchObject] Sketch006
  FullyConstrained = false
  MapMode = 5
  Support = -> [XY_Plane001]
  sketch-geometry (6):
    g0: LineSegment StartX=116.7 StartY=102.3 StartZ=0 EndX=124.3 EndY=102.3 EndZ=0
    g1: LineSegment StartX=116.7 StartY=93.6 StartZ=0 EndX=116.7 EndY=102.3 EndZ=0
    g2: LineSegment StartX=124.3 StartY=102.3 StartZ=0 EndX=124.3 EndY=93.9 EndZ=0
    g3: LineSegment StartX=124.3 StartY=93.9 StartZ=0 EndX=124.3 EndY=93.6 EndZ=0
    g4: LineSegment StartX=124.3 StartY=93.6 StartZ=0 EndX=120.7 EndY=93.6 EndZ=0
    g5: LineSegment StartX=120.7 StartY=93.6 StartZ=0 EndX=116.7 EndY=93.6 EndZ=0
  constraints (16):
    c: Horizontal(g0)
    c: Vertical(g1)
    c: DistanceY(g0) = 102.3
    c: DistanceY(g3) = 93.6
    c: Vertical(g2)
    c: Vertical(g3)
    c: Horizontal(g4)
    c: Horizontal(g5)
    c: DistanceX(g0) = 124.3
    c: DistanceX(g0) = 116.7
    c: Coincident(g0,g1)
    c: Coincident(g0,g2)
    c: Coincident(g3,g4)
    c: Coincident(g2,g3)
    c: Coincident(g4,g5)
    c: Coincident(g1,g5)
FEATURE [PartDesign::Pocket] Pocket005
  BaseFeature = -> Pocket004
  Direction = (0,0,-1)
  Length = 4.4
  Length2 = 5
  Profile = -> Sketch006
  ReferenceAxis = -> Sketch006 [N_Axis]
  Reversed = true
  Type = 0
FEATURE [Sketcher::SketchObject] Sketch007
  FullyConstrained = true
  MapMode = 5
  Placement = pos=(0,0,11) rot=(0,0,1;0rad)
  Support = -> [DatumPlane]
  sketch-geometry (4):
    g0: LineSegment StartX=131 StartY=101.8 StartZ=0 EndX=120.5 EndY=101.8 EndZ=0
    g1: LineSegment StartX=120.5 StartY=101.8 StartZ=0 EndX=120.5 EndY=80.8 EndZ=0
    g2: LineSegment StartX=120.5 StartY=80.8 StartZ=0 EndX=131 EndY=80.8 EndZ=0
    g3: LineSegment StartX=131 StartY=80.8 StartZ=0 EndX=131 EndY=101.8 EndZ=0
  constraints (12):
    c: Coincident(g0,g1)
    c: Coincident(g1,g2)
    c: Coincident(g2,g3)
    c: Coincident(g3,g0)
    c: Horizontal(g0)
    c: Horizontal(g2)
    c: Vertical(g1)
    c: Vertical(g3)
    c: Distance(g2) = 10.5
    c: Distance(g3) = 21
    c: DistanceY(g0) = 101.8
    c: DistanceX(g0) = 131
FEATURE [PartDesign::Pocket] Pocket006
  BaseFeature = -> Pocket005
  Direction = (0,0,-1)
  Length = 5
  Length2 = 5
  Profile = -> Sketch007
  ReferenceAxis = -> Sketch007 [N_Axis]
  Reversed = true
  Type = 0
FEATURE [Sketcher::SketchObject] Sketch008
  FullyConstrained = false
  MapMode = 5
  Placement = pos=(0,0,11) rot=(0,0,1;0rad)
  Support = -> [DatumPlane]
  sketch-geometry (6):
    g0: LineSegment StartX=127.329 StartY=102.8 StartZ=0 EndX=132 EndY=102.8 EndZ=0
    g1: LineSegment StartX=132 StartY=102.8 StartZ=0 EndX=132 EndY=79.4945 EndZ=0
    g2: LineSegment StartX=132 StartY=79.4945 StartZ=0 EndX=119.5 EndY=79.4945 EndZ=0
    g3: LineSegment StartX=119.5 StartY=79.4945 StartZ=0 EndX=119.5 EndY=94.9604 EndZ=0
    g4: LineSegment StartX=119.5 StartY=94.9604 StartZ=0 EndX=127.329 EndY=94.9604 EndZ=0
    g5: LineSegment StartX=127.329 StartY=94.9604 StartZ=0 EndX=127.329 EndY=102.8 EndZ=0
  constraints (15):
    c: Coincident(g0,g1)
    c: Vertical(g1)
    c: Coincident(g1,g2)
    c: Horizontal(g2)
    c: Coincident(g2,g3)
    c: Vertical(g3)
    c: Coincident(g3,g4)
    c: Horizontal(g4)
    c: Coincident(g4,g5)
    c: Coincident(g5,g0)
    c: Vertical(g5)
    c: Horizontal(g0)
    c: DistanceX(g0) = 132
    c: DistanceY(g0) = 102.8
    c: DistanceX(g2) = 119.5
FEATURE [PartDesign::Pocket] Pocket007
  BaseFeature = -> Pocket006
  Direction = (0,0,-1)
  Length = 18
  Length2 = 5
  Profile = -> Sketch008
  ReferenceAxis = -> Sketch008 [N_Axis]
  Type = 0
FEATURE [PartDesign::Body] Body
  Group = -> [Sketch,Pad,DatumPlane,Sketch001,Pocket,Sketch002,Pocket001,Sketch003,Pocket002,DatumPlane001,Sketch005,Pocket004,Sketch006,Pocket005,Sketch007,Pocket006,Sketch008,Pocket007]
  Origin = -> Origin
  Tip = -> Pocket007
FEATURE [App::Part] side_front_L
  Group = -> [LCS_0,Body]
  Origin = -> Origin001
---- part speaker-enclosure-L.FCStd = doc fcstd_c7e8bbd3b1a0 ----
FCSTD DOCUMENT  (FreeCAD 0.21R33668 +7 (Git))
Label: speaker-enclosure-L
License: All rights reserved
LicenseURL: http://en.wikipedia.org/wiki/All_rights_reserved
objects: Sketcher::SketchObject×5, PartDesign::Pocket×3, PartDesign::Pad×2, PartDesign::CoordinateSystem×1, PartDesign::Plane×1, PartDesign::Body×1, App::Part×1
note: 18 computed .brp shape members not serialized (recipe doc carries the construction recipe); baked Part::Feature solids carry a one-line shape summary decoded from their .brp

FEATURE [Sketcher::SketchObject] Sketch
  FullyConstrained = true
  MapMode = 5
  Support = -> [XY_Plane]
  sketch-geometry (4):
    g0: LineSegment StartX=0 StartY=0 StartZ=0 EndX=54.7 EndY=0 EndZ=0
    g1: LineSegment StartX=54.7 StartY=0 StartZ=0 EndX=54.7 EndY=77 EndZ=0
    g2: LineSegment StartX=54.7 StartY=77 StartZ=0 EndX=0 EndY=77 EndZ=0
    g3: LineSegment StartX=0 StartY=77 StartZ=0 EndX=0 EndY=0 EndZ=0
  constraints (11):
    c: Coincident(g0,g1)
    c: Coincident(g1,g2)
    c: Coincident(g2,g3)
    c: Coincident(g3,g0)
    c: Horizontal(g0)
    c: Horizontal(g2)
    c: Vertical(g1)
    c: Vertical(g3)
    c: Coincident(g0,g-1)
    c: DistanceY(g3,g3) = 77
    c: DistanceX(g0,g0) = 54.7
FEATURE [PartDesign::Pad] Pad
  Direction = (0,0,1)
  Length = 53
  Length2 = 10
  Profile = -> Sketch
  ReferenceAxis = -> Sketch [N_Axis]
  Type = 0
FEATURE [Sketcher::SketchObject] Sketch001
  FullyConstrained = true
  MapMode = 5
  Support = -> [XY_Plane]
  sketch-geometry (4):
    g0: LineSegment StartX=2.51 StartY=2.51 StartZ=0 EndX=52.49 EndY=2.51 EndZ=0
    g1: LineSegment StartX=52.49 StartY=2.51 StartZ=0 EndX=52.49 EndY=74.49 EndZ=0
    g2: LineSegment StartX=52.49 StartY=74.49 StartZ=0 EndX=2.51 EndY=74.49 EndZ=0
    g3: LineSegment StartX=2.51 StartY=74.49 StartZ=0 EndX=2.51 EndY=2.51 EndZ=0
  constraints (12):
    c: Coincident(g0,g1)
    c: Coincident(g1,g2)
    c: Coincident(g2,g3)
    c: Coincident(g3,g0)
    c: Horizontal(g0)
    c: Horizontal(g2)
    c: Vertical(g1)
    c: Vertical(g3)
    c: DistanceX(g0) = 2.51
    c: DistanceY(g0) = 2.51
    c: DistanceY(g2) = 74.49
    c: DistanceX(g1) = 52.49
FEATURE [PartDesign::Pocket] Pocket
  BaseFeature = -> Pad
  Direction = (0,0,-1)
  Length = 52.3
  Length2 = 5
  Profile = -> Sketch001
  ReferenceAxis = -> Sketch001 [N_Axis]
  Reversed = true
  Type = 0
FEATURE [PartDesign::CoordinateSystem] LCS_0
  AttacherType = Attacher::AttachEngine3D
  MapMode = 2
  Support = -> [X_Axis001]
FEATURE [Sketcher::SketchObject] Sketch002
  FullyConstrained = true
  MapMode = 5
  Placement = pos=(0,0,0) rot=(0.57735,0.57735,0.57735;2.0944rad)
  Support = -> [YZ_Plane]
  sketch-geometry (1):
    g0: Circle CenterX=20 CenterY=40 CenterZ=0 NormalX=0 NormalY=0 NormalZ=1 AngleXU=0 Radius=5
  constraints (3):
    c: DistanceX(g0) = 20
    c: DistanceY(g0) = 40
    c: Diameter(g0) = 10
FEATURE [PartDesign::Pocket] Pocket001
  BaseFeature = -> Pocket
  Direction = (-1,2e-16,-3e-16)
  Length = 5
  Length2 = 5
  Profile = -> Sketch002
  ReferenceAxis = -> Sketch002 [N_Axis]
  Reversed = true
  Type = 0
FEATURE [PartDesign::Plane] DatumPlane
  AttachmentOffset = pos=(0,0,55) rot=(0,0,1;0rad)
  Length = 60
  MapMode = 5
  Placement = pos=(55,-1.22e-14,1.22e-14) rot=(0.57735,0.57735,0.57735;2.0944rad)
  ResizeMode = 0
  Support = -> [YZ_Plane]
  Width = 60
FEATURE [Sketcher::SketchObject] Sketch003
  FullyConstrained = true
  MapMode = 5
  Placement = pos=(55,-1.22e-14,1.22e-14) rot=(0.57735,0.57735,0.57735;2.0944rad)
  Support = -> [DatumPlane]
  sketch-geometry (1):
    g0: Circle CenterX=0 CenterY=27.3 CenterZ=0 NormalX=0 NormalY=0 NormalZ=1 AngleXU=0 Radius=8
  constraints (3):
    c: PointOnObject(g0,g-2)
    c: Diameter(g0) = 16
    c: DistanceY(g0) = 27.3
FEATURE [Sketcher::SketchObject] Sketch004
  FullyConstrained = true
  MapMode = 5
  Placement = pos=(55,-1.22e-14,1.22e-14) rot=(0.57735,0.57735,0.57735;2.0944rad)
  Support = -> [DatumPlane]
  sketch-geometry (2):
    g0: ArcOfCircle CenterX=0 CenterY=27.3 CenterZ=0 NormalX=0 NormalY=0 NormalZ=1 AngleXU=0 Radius=9.5 StartAngle=4.71239 EndAngle=7.85398
    g1: LineSegment StartX=2.9e-15 StartY=36.8 StartZ=0 EndX=2.9e-15 EndY=17.8 EndZ=0
  constraints (7):
    c: PointOnObject(g0,g-2)
    c: Diameter(g0) = 19
    c: DistanceY(g0) = 27.3
    c: Vertical(g1)
    c: PointOnObject(g1,g-2)
    c: Coincident(g0,g1)
    c: Coincident(g0,g1)
FEATURE [PartDesign::Pad] Pad001
  BaseFeature = -> Pocket001
  Direction = (1,-1e-16,1e-16)
  Length = 18
  Length2 = 10
  Profile = -> Sketch004
  ReferenceAxis = -> Sketch004 [N_Axis]
  Reversed = true
  Type = 0
FEATURE [PartDesign::Pocket] Pocket002
  BaseFeature = -> Pad001
  Direction = (-1,1e-16,-1e-16)
  Length = 32
  Length2 = 5
  Midplane = true
  Profile = -> Sketch003
  ReferenceAxis = -> Sketch003 [N_Axis]
  Type = 0
FEATURE [PartDesign::Body] Body
  Group = -> [Sketch,Pad,Sketch001,Pocket,Sketch002,Pocket001,DatumPlane,Sketch003,Sketch004,Pad001,Pocket002]
  Origin = -> Origin
  Tip = -> Pocket002
FEATURE [App::Part] enc_L
  Group = -> [LCS_0,Body]
  Origin = -> Origin001
---- part speaker-enclosure-R.FCStd = doc fcstd_be412e16a0c8 ----
FCSTD DOCUMENT  (FreeCAD 0.21R33668 +7 (Git))
Label: speaker-enclosure-R
License: All rights reserved
LicenseURL: http://en.wikipedia.org/wiki/All_rights_reserved
objects: Sketcher::SketchObject×5, PartDesign::Pocket×3, PartDesign::Pad×2, PartDesign::CoordinateSystem×1, PartDesign::Plane×1, PartDesign::Body×1, App::Part×1
note: 18 computed .brp shape members not serialized (recipe doc carries the construction recipe); baked Part::Feature solids carry a one-line shape summary decoded from their .brp

FEATURE [Sketcher::SketchObject] Sketch
  FullyConstrained = true
  MapMode = 5
  Support = -> [XY_Plane]
  sketch-geometry (4):
    g0: LineSegment StartX=0 StartY=0 StartZ=0 EndX=54.7 EndY=0 EndZ=0
    g1: LineSegment StartX=54.7 StartY=0 StartZ=0 EndX=54.7 EndY=127 EndZ=0
    g2: LineSegment StartX=54.7 StartY=127 StartZ=0 EndX=0 EndY=127 EndZ=0
    g3: LineSegment StartX=0 StartY=127 StartZ=0 EndX=0 EndY=0 EndZ=0
  constraints (11):
    c: Coincident(g0,g1)
    c: Coincident(g1,g2)
    c: Coincident(g2,g3)
    c: Coincident(g3,g0)
    c: Horizontal(g0)
    c: Horizontal(g2)
    c: Vertical(g1)
    c: Vertical(g3)
    c: Coincident(g0,g-1)
    c: DistanceY(g3,g3) = 127
    c: DistanceX(g0,g0) = 54.7
FEATURE [PartDesign::Pad] Pad
  Direction = (0,0,1)
  Length = 32
  Length2 = 10
  Profile = -> Sketch
  ReferenceAxis = -> Sketch [N_Axis]
  Type = 0
FEATURE [Sketcher::SketchObject] Sketch001
  FullyConstrained = true
  MapMode = 5
  Support = -> [XY_Plane]
  sketch-geometry (4):
    g0: LineSegment StartX=2.51 StartY=2.51 StartZ=0 EndX=52.49 EndY=2.51 EndZ=0
    g1: LineSegment StartX=52.49 StartY=2.51 StartZ=0 EndX=52.49 EndY=124.49 EndZ=0
    g2: LineSegment StartX=52.49 StartY=124.49 StartZ=0 EndX=2.51 EndY=124.49 EndZ=0
    g3: LineSegment StartX=2.51 StartY=124.49 StartZ=0 EndX=2.51 EndY=2.51 EndZ=0
  constraints (12):
    c: Coincident(g0,g1)
    c: Coincident(g1,g2)
    c: Coincident(g2,g3)
    c: Coincident(g3,g0)
    c: Horizontal(g0)
    c: Horizontal(g2)
    c: Vertical(g1)
    c: Vertical(g3)
    c: DistanceX(g0) = 2.51
    c: DistanceY(g0) = 2.51
    c: DistanceY(g2) = 124.49
    c: DistanceX(g1) = 52.49
FEATURE [PartDesign::Pocket] Pocket
  BaseFeature = -> Pad
  Direction = (0,0,-1)
  Length = 31.3
  Length2 = 5
  Profile = -> Sketch001
  ReferenceAxis = -> Sketch001 [N_Axis]
  Reversed = true
  Type = 0
FEATURE [PartDesign::CoordinateSystem] LCS_0
  AttacherType = Attacher::AttachEngine3D
  MapMode = 2
  Support = -> [X_Axis001]
FEATURE [PartDesign::Plane] DatumPlane
  AttachmentOffset = pos=(0,0,55) rot=(0,0,1;0rad)
  Length = 60
  MapMode = 5
  Placement = pos=(55,-1.22e-14,1.22e-14) rot=(0.57735,0.57735,0.57735;2.0944rad)
  ResizeMode = 0
  Support = -> [YZ_Plane]
  Width = 60
FEATURE [Sketcher::SketchObject] Sketch002
  FullyConstrained = true
  MapMode = 5
  Placement = pos=(0,0,0) rot=(0.57735,0.57735,0.57735;2.0944rad)
  Support = -> [YZ_Plane]
  sketch-geometry (1):
    g0: Circle CenterX=0 CenterY=26 CenterZ=0 NormalX=0 NormalY=0 NormalZ=1 AngleXU=0 Radius=7.5
  constraints (3):
    c: PointOnObject(g0,g-2)
    c: Diameter(g0) = 15
    c: DistanceY(g0) = 26
FEATURE [Sketcher::SketchObject] Sketch003
  FullyConstrained = true
  MapMode = 5
  Placement = pos=(0,0,0) rot=(0.57735,0.57735,0.57735;2.0944rad)
  Support = -> [YZ_Plane]
  sketch-geometry (3):
    g0: ArcOfCircle CenterX=0 CenterY=26 CenterZ=0 NormalX=0 NormalY=0 NormalZ=1 AngleXU=0 Radius=9 StartAngle=4.71239 EndAngle=7.01291
    g1: LineSegment StartX=-1.7e-15 StartY=32 StartZ=0 EndX=-1.7e-15 EndY=17 EndZ=0
    g2: LineSegment StartX=-1.7e-15 StartY=32 StartZ=0 EndX=6.7082 EndY=32 EndZ=0
  constraints (10):
    c: PointOnObject(g0,g-2)
    c: Diameter(g0) = 18
    c: DistanceY(g0) = 26
    c: Vertical(g1)
    c: PointOnObject(g1,g-2)
    c: Coincident(g0,g1)
    c: Horizontal(g2)
    c: DistanceY(g2) = 32
    c: Coincident(g0,g2)
    c: Coincident(g1,g2)
FEATURE [PartDesign::Pad] Pad001
  BaseFeature = -> Pocket
  Direction = (1,-2e-16,3e-16)
  Length = 16
  Length2 = 10
  Profile = -> Sketch003
  ReferenceAxis = -> Sketch003 [N_Axis]
  Type = 0
FEATURE [PartDesign::Pocket] Pocket001
  BaseFeature = -> Pad001
  Direction = (-1,2e-16,-3e-16)
  Length = 14
  Length2 = 5
  Profile = -> Sketch002
  ReferenceAxis = -> Sketch002 [N_Axis]
  Reversed = true
  Type = 0
FEATURE [Sketcher::SketchObject] Sketch004
  FullyConstrained = false
  MapMode = 5
  Placement = pos=(55,-1.22e-14,1.22e-14) rot=(0.57735,0.57735,0.57735;2.0944rad)
  Support = -> [DatumPlane]
  sketch-geometry (1):
    g0: Circle CenterX=20.006 CenterY=23 CenterZ=0 NormalX=0 NormalY=0 NormalZ=1 AngleXU=0 Radius=5
  constraints (2):
    c: Diameter(g0) = 10
    c: DistanceY(g0) = 23
FEATURE [PartDesign::Pocket] Pocket002
  BaseFeature = -> Pocket001
  Direction = (-1,1e-16,-1e-16)
  Length = 5
  Length2 = 5
  Profile = -> Sketch004
  ReferenceAxis = -> Sketch004 [N_Axis]
  Type = 0
FEATURE [PartDesign::Body] Body
  Group = -> [Sketch,Pad,Sketch001,Pocket,DatumPlane,Pad001,Sketch002,Pocket001,Sketch003,Sketch004,Pocket002]
  Origin = -> Origin
  Tip = -> Pocket002
FEATURE [App::Part] enc_L  label="enc_R"
  Group = -> [LCS_0,Body]
  Origin = -> Origin001
---- part speaker-enclosure-lid-L.FCStd = doc fcstd_d64e1ba33d2b ----
FCSTD DOCUMENT  (FreeCAD 0.21R33668 +7 (Git))
Label: speaker-enclosure-lid-L
License: All rights reserved
LicenseURL: http://en.wikipedia.org/wiki/All_rights_reserved
objects: Sketcher::SketchObject×4, PartDesign::Pad×3, PartDesign::Pocket×1, PartDesign::CoordinateSystem×1, PartDesign::Body×1, App::Part×1
note: 14 computed .brp shape members not serialized (recipe doc carries the construction recipe); baked Part::Feature solids carry a one-line shape summary decoded from their .brp
EXTERNAL_REF file=planB.FCStd obj=Spreadsheet

FEATURE [Sketcher::SketchObject] Sketch
  FullyConstrained = true
  MapMode = 5
  Support = -> [XY_Plane]
  sketch-geometry (4):
    g0: LineSegment StartX=0 StartY=0 StartZ=0 EndX=54.7 EndY=0 EndZ=0
    g1: LineSegment StartX=54.7 StartY=0 StartZ=0 EndX=54.7 EndY=127 EndZ=0
    g2: LineSegment StartX=54.7 StartY=127 StartZ=0 EndX=0 EndY=127 EndZ=0
    g3: LineSegment StartX=0 StartY=127 StartZ=0 EndX=0 EndY=0 EndZ=0
  constraints (11):
    c: Coincident(g0,g1)
    c: Coincident(g1,g2)
    c: Coincident(g2,g3)
    c: Coincident(g3,g0)
    c: Horizontal(g0)
    c: Horizontal(g2)
    c: Vertical(g1)
    c: Vertical(g3)
    c: Coincident(g0,g-1)
    c: DistanceX(g0,g0) = 54.7
    c: DistanceY(g3,g3) = 127
FEATURE [PartDesign::Pad] Pad
  Direction = (0,0,1)
  Length = 5
  Length2 = 10
  Profile = -> Sketch
  ReferenceAxis = -> Sketch [N_Axis]
  Reversed = true
  Type = 0
FEATURE [Sketcher::SketchObject] Sketch001
  FullyConstrained = false
  MapMode = 5
  Support = -> [XY_Plane]
  expr: Constraints[18] = planB#<<data>>.insert_diameter
  sketch-geometry (9):
    g0: LineSegment StartX=2.8 StartY=2.8 StartZ=0 EndX=51.9 EndY=2.8 EndZ=0
    g1: LineSegment StartX=51.9 StartY=2.8 StartZ=0 EndX=51.9 EndY=74.2 EndZ=0
    g2: LineSegment StartX=51.9 StartY=74.2 StartZ=0 EndX=2.8 EndY=74.2 EndZ=0
    g3: LineSegment StartX=2.8 StartY=74.2 StartZ=0 EndX=2.8 EndY=2.8 EndZ=0
    g4: Circle CenterX=27.35 CenterY=12.8239 CenterZ=0 NormalX=0 NormalY=0 NormalZ=1 AngleXU=0 Radius=2.15
    g5: Circle CenterX=27.35 CenterY=64.2239 CenterZ=0 NormalX=0 NormalY=0 NormalZ=1 AngleXU=0 Radius=2.15
    g6: LineSegment StartX=27.35 StartY=12.8239 StartZ=0 EndX=27.35 EndY=64.2239 EndZ=0
    g7: GeomPoint X=27.35 Y=38.5239 Z=0
    g8: Circle CenterX=27.35 CenterY=38.5239 CenterZ=0 NormalX=0 NormalY=0 NormalZ=1 AngleXU=0 Radius=22.5
  constraints (21):
    c: Coincident(g0,g1)
    c: Coincident(g1,g2)
    c: Coincident(g2,g3)
    c: Coincident(g3,g0)
    c: Horizontal(g0)
    c: Horizontal(g2)
    c: Vertical(g1)
    c: Vertical(g3)
    c: Coincident(g6,g4)
    c: Coincident(g6,g5)
    c: DistanceY(g6,g6) = 51.4
    c: DistanceX(g4) = 27.35
    c: DistanceX(g0) = 2.8
    c: DistanceY(g0) = 2.8
    c: Symmetric(g4,g5,g7)
    c: Equal(g4,g5)
    c: Coincident(g8,g7)
    c: Diameter(g8) = 45
    c: Diameter(g5) = 4.3
    c: DistanceY(g2) = 74.2
    c: Symmetric(g0,g0,g6)
FEATURE [PartDesign::Pad] Pad001
  BaseFeature = -> Pad
  Direction = (0,0,1)
  Length = 5
  Length2 = 10
  Profile = -> Sketch001
  ReferenceAxis = -> Sketch001 [N_Axis]
  Type = 0
FEATURE [Sketcher::SketchObject] Sketch002
  FullyConstrained = false
  MapMode = 5
  Support = -> [XY_Plane]
  expr: Constraints[18] = planB#<<data>>.insert_diameter
  sketch-geometry (9):
    g0: LineSegment StartX=2.8 StartY=2.8 StartZ=0 EndX=51.9 EndY=2.8 EndZ=0
    g1: LineSegment StartX=51.9 StartY=2.8 StartZ=0 EndX=51.9 EndY=74.2 EndZ=0
    g2: LineSegment StartX=51.9 StartY=74.2 StartZ=0 EndX=2.8 EndY=74.2 EndZ=0
    g3: LineSegment StartX=2.8 StartY=74.2 StartZ=0 EndX=2.8 EndY=2.8 EndZ=0
    g4: Circle CenterX=27.35 CenterY=12.8239 CenterZ=0 NormalX=0 NormalY=0 NormalZ=1 AngleXU=0 Radius=2.15
    g5: Circle CenterX=27.35 CenterY=64.2239 CenterZ=0 NormalX=0 NormalY=0 NormalZ=1 AngleXU=0 Radius=2.15
    g6: LineSegment StartX=27.35 StartY=12.8239 StartZ=0 EndX=27.35 EndY=64.2239 EndZ=0
    g7: GeomPoint X=27.35 Y=38.5239 Z=0
    g8: Circle CenterX=27.35 CenterY=38.5239 CenterZ=0 NormalX=0 NormalY=0 NormalZ=1 AngleXU=0 Radius=22.5
  constraints (21):
    c: Coincident(g0,g1)
    c: Coincident(g1,g2)
    c: Coincident(g2,g3)
    c: Coincident(g3,g0)
    c: Horizontal(g0)
    c: Horizontal(g2)
    c: Vertical(g1)
    c: Vertical(g3)
    c: Coincident(g6,g4)
    c: Coincident(g6,g5)
    c: DistanceY(g6,g6) = 51.4
    c: DistanceX(g4) = 27.35
    c: DistanceX(g0) = 2.8
    c: DistanceY(g0) = 2.8
    c: Symmetric(g4,g5,g7)
    c: Equal(g4,g5)
    c: Coincident(g8,g7)
    c: Diameter(g8) = 45
    c: Diameter(g5) = 4.3
    c: DistanceY(g2) = 74.2
    c: Symmetric(g0,g0,g6)
FEATURE [PartDesign::Pocket] Pocket
  BaseFeature = -> Pad001
  Direction = (0,0,-1)
  Length = 3
  Length2 = 5
  Profile = -> Sketch002
  ReferenceAxis = -> Sketch002 [N_Axis]
  Type = 0
FEATURE [PartDesign::CoordinateSystem] LCS_0
  AttacherType = Attacher::AttachEngine3D
  MapMode = 2
  Support = -> [X_Axis001]
FEATURE [Sketcher::SketchObject] Sketch003
  FullyConstrained = false
  MapMode = 5
  Support = -> [XY_Plane]
  sketch-geometry (8):
    g0: LineSegment StartX=0 StartY=77.3 StartZ=0 EndX=2.51 EndY=77.3 EndZ=0
    g1: LineSegment StartX=2.51 StartY=77.3 StartZ=0 EndX=2.51 EndY=127 EndZ=0
    g2: LineSegment StartX=2.51 StartY=127 StartZ=0 EndX=0 EndY=127 EndZ=0
    g3: LineSegment StartX=0 StartY=127 StartZ=0 EndX=0 EndY=77.3 EndZ=0
    g4: LineSegment StartX=51.7245 StartY=127 StartZ=0 EndX=54.2345 EndY=127 EndZ=0
    g5: LineSegment StartX=54.2345 StartY=127 StartZ=0 EndX=54.2345 EndY=77.3 EndZ=0
    g6: LineSegment StartX=54.2345 StartY=77.3 StartZ=0 EndX=51.7245 EndY=77.3 EndZ=0
    g7: LineSegment StartX=51.7245 StartY=77.3 StartZ=0 EndX=51.7245 EndY=127 EndZ=0
  constraints (23):
    c: Coincident(g0,g1)
    c: Coincident(g1,g2)
    c: Coincident(g2,g3)
    c: Coincident(g3,g0)
    c: Horizontal(g0)
    c: Horizontal(g2)
    c: Vertical(g1)
    c: Vertical(g3)
    c: PointOnObject(g0,g-2)
    c: Coincident(g4,g5)
    c: Coincident(g5,g6)
    c: Coincident(g6,g7)
    c: Coincident(g7,g4)
    c: Horizontal(g4)
    c: Horizontal(g6)
    c: Vertical(g5)
    c: Vertical(g7)
    c: PointOnObject(g0,g6)
    c: PointOnObject(g1,g4)
    c: Equal(g2,g4)
    c: DistanceX(g0,g0) = 2.51
    c: DistanceY(g0) = 77.3
    c: DistanceY(g1) = 127
FEATURE [PartDesign::Pad] Pad002
  BaseFeature = -> Pocket
  Direction = (0,0,1)
  Length = 12
  Length2 = 10
  Profile = -> Sketch003
  ReferenceAxis = -> Sketch003 [N_Axis]
  Type = 0
FEATURE [PartDesign::Body] Body
  Group = -> [Sketch,Pad,Sketch001,Pad001,Sketch002,Pocket,Sketch003,Pad002]
  Origin = -> Origin
  Tip = -> Pad002
FEATURE [App::Part] enc_lid_L  label="enc_lid__L"
  Group = -> [LCS_0,Body]
  Origin = -> Origin001
---- part speaker-enclosure-lid-R.FCStd = doc fcstd_3751ce8ea2d0 ----
FCSTD DOCUMENT  (FreeCAD 0.21R33668 +7 (Git))
Label: speaker-enclosure-lid-R
License: All rights reserved
LicenseURL: http://en.wikipedia.org/wiki/All_rights_reserved
objects: Sketcher::SketchObject×3, PartDesign::Pad×2, PartDesign::Pocket×1, PartDesign::Body×1, PartDesign::CoordinateSystem×1, App::Part×1
note: 11 computed .brp shape members not serialized (recipe doc carries the construction recipe); baked Part::Feature solids carry a one-line shape summary decoded from their .brp
EXTERNAL_REF file=planB.FCStd obj=Spreadsheet

FEATURE [Sketcher::SketchObject] Sketch
  FullyConstrained = true
  MapMode = 5
  Support = -> [XY_Plane]
  sketch-geometry (4):
    g0: LineSegment StartX=0 StartY=0 StartZ=0 EndX=54.7 EndY=0 EndZ=0
    g1: LineSegment StartX=54.7 StartY=0 StartZ=0 EndX=54.7 EndY=127 EndZ=0
    g2: LineSegment StartX=54.7 StartY=127 StartZ=0 EndX=0 EndY=127 EndZ=0
    g3: LineSegment StartX=0 StartY=127 StartZ=0 EndX=0 EndY=0 EndZ=0
  constraints (11):
    c: Coincident(g0,g1)
    c: Coincident(g1,g2)
    c: Coincident(g2,g3)
    c: Coincident(g3,g0)
    c: Horizontal(g0)
    c: Horizontal(g2)
    c: Vertical(g1)
    c: Vertical(g3)
    c: Coincident(g0,g-1)
    c: DistanceX(g0,g0) = 54.7
    c: DistanceY(g3,g3) = 127
FEATURE [PartDesign::Pad] Pad
  Direction = (0,0,1)
  Length = 5
  Length2 = 10
  Profile = -> Sketch
  ReferenceAxis = -> Sketch [N_Axis]
  Reversed = true
  Type = 0
FEATURE [Sketcher::SketchObject] Sketch001
  FullyConstrained = false
  MapMode = 5
  Support = -> [XY_Plane]
  expr: Constraints[18] = planB#<<data>>.insert_diameter
  sketch-geometry (12):
    g0: LineSegment StartX=2.8 StartY=2.8 StartZ=0 EndX=51.9 EndY=2.8 EndZ=0
    g1: LineSegment StartX=51.9 StartY=2.8 StartZ=0 EndX=51.9 EndY=74.2 EndZ=0
    g2: LineSegment StartX=51.9 StartY=74.2 StartZ=0 EndX=2.8 EndY=74.2 EndZ=0
    g3: LineSegment StartX=2.8 StartY=74.2 StartZ=0 EndX=2.8 EndY=2.8 EndZ=0
    g4: Circle CenterX=27.35 CenterY=12.8239 CenterZ=0 NormalX=0 NormalY=0 NormalZ=1 AngleXU=0 Radius=2.15
    g5: Circle CenterX=27.35 CenterY=64.2239 CenterZ=0 NormalX=0 NormalY=0 NormalZ=1 AngleXU=0 Radius=2.15
    g6: LineSegment StartX=27.35 StartY=12.8239 StartZ=0 EndX=27.35 EndY=64.2239 EndZ=0
    g7: GeomPoint X=27.35 Y=38.5239 Z=0
    g8: Circle CenterX=27.35 CenterY=38.5239 CenterZ=0 NormalX=0 NormalY=0 NormalZ=1 AngleXU=0 Radius=22.5
    g9: LineSegment StartX=2.8 StartY=74.2 StartZ=0 EndX=2.8 EndY=124.2 EndZ=0
    g10: LineSegment StartX=2.8 StartY=124.2 StartZ=0 EndX=51.9 EndY=124.2 EndZ=0
    g11: LineSegment StartX=51.9 StartY=124.2 StartZ=0 EndX=51.9 EndY=74.2 EndZ=0
  constraints (29):
    c: Coincident(g0,g1)
    c: Coincident(g1,g2)
    c: Coincident(g2,g3)
    c: Coincident(g3,g0)
    c: Horizontal(g0)
    c: Horizontal(g2)
    c: Vertical(g1)
    c: Vertical(g3)
    c: Coincident(g6,g4)
    c: Coincident(g6,g5)
    c: DistanceY(g6,g6) = 51.4
    c: DistanceX(g4) = 27.35
    c: DistanceX(g0) = 2.8
    c: DistanceY(g0) = 2.8
    c: Symmetric(g4,g5,g7)
    c: Equal(g4,g5)
    c: Coincident(g8,g7)
    c: Diameter(g8) = 45
    c: Diameter(g5) = 4.3
    c: DistanceY(g2) = 74.2
    c: Symmetric(g0,g0,g6)
    c: Coincident(g3,g9)
    c: Vertical(g9)
    c: Coincident(g9,g10)
    c: Horizontal(g10)
    c: Coincident(g10,g11)
    c: Coincident(g11,g1)
    c: Vertical(g11)
    c: DistanceY(g9,g9) = 50
FEATURE [PartDesign::Pad] Pad001
  BaseFeature = -> Pad
  Direction = (0,0,1)
  Length = 5
  Length2 = 10
  Profile = -> Sketch001
  ReferenceAxis = -> Sketch001 [N_Axis]
  Type = 0
FEATURE [Sketcher::SketchObject] Sketch002
  FullyConstrained = false
  MapMode = 5
  Support = -> [XY_Plane]
  expr: Constraints[18] = planB#<<data>>.insert_diameter
  sketch-geometry (9):
    g0: LineSegment StartX=2.8 StartY=2.8 StartZ=0 EndX=51.9 EndY=2.8 EndZ=0
    g1: LineSegment StartX=51.9 StartY=2.8 StartZ=0 EndX=51.9 EndY=74.2 EndZ=0
    g2: LineSegment StartX=51.9 StartY=74.2 StartZ=0 EndX=2.8 EndY=74.2 EndZ=0
    g3: LineSegment StartX=2.8 StartY=74.2 StartZ=0 EndX=2.8 EndY=2.8 EndZ=0
    g4: Circle CenterX=27.35 CenterY=12.8239 CenterZ=0 NormalX=0 NormalY=0 NormalZ=1 AngleXU=0 Radius=2.15
    g5: Circle CenterX=27.35 CenterY=64.2239 CenterZ=0 NormalX=0 NormalY=0 NormalZ=1 AngleXU=0 Radius=2.15
    g6: LineSegment StartX=27.35 StartY=12.8239 StartZ=0 EndX=27.35 EndY=64.2239 EndZ=0
    g7: GeomPoint X=27.35 Y=38.5239 Z=0
    g8: Circle CenterX=27.35 CenterY=38.5239 CenterZ=0 NormalX=0 NormalY=0 NormalZ=1 AngleXU=0 Radius=22.5
  constraints (21):
    c: Coincident(g0,g1)
    c: Coincident(g1,g2)
    c: Coincident(g2,g3)
    c: Coincident(g3,g0)
    c: Horizontal(g0)
    c: Horizontal(g2)
    c: Vertical(g1)
    c: Vertical(g3)
    c: Coincident(g6,g4)
    c: Coincident(g6,g5)
    c: DistanceY(g6,g6) = 51.4
    c: DistanceX(g4) = 27.35
    c: DistanceX(g0) = 2.8
    c: DistanceY(g0) = 2.8
    c: Symmetric(g4,g5,g7)
    c: Equal(g4,g5)
    c: Coincident(g8,g7)
    c: Diameter(g8) = 45
    c: Diameter(g5) = 4.3
    c: DistanceY(g2) = 74.2
    c: Symmetric(g0,g0,g6)
FEATURE [PartDesign::Pocket] Pocket
  BaseFeature = -> Pad001
  Direction = (0,0,-1)
  Length = 3
  Length2 = 5
  Profile = -> Sketch002
  ReferenceAxis = -> Sketch002 [N_Axis]
  Type = 0
FEATURE [PartDesign::Body] Body
  Group = -> [Sketch,Pad,Sketch001,Pad001,Sketch002,Pocket]
  Origin = -> Origin
  Tip = -> Pocket
FEATURE [PartDesign::CoordinateSystem] LCS_0
  AttacherType = Attacher::AttachEngine3D
  MapMode = 2
  Support = -> [X_Axis001]
FEATURE [App::Part] enc_lid_L  label="enc_lid_R"
  Group = -> [LCS_0,Body]
  Origin = -> Origin001
---- part speaker.FCStd = doc fcstd_d16aff92c74e ----
FCSTD DOCUMENT  (FreeCAD 0.21R33668 +7 (Git))
Label: speaker
License: All rights reserved
LicenseURL: http://en.wikipedia.org/wiki/All_rights_reserved
objects: Sketcher::SketchObject×1, PartDesign::Pad×1, PartDesign::Body×1, PartDesign::CoordinateSystem×1, App::Part×1
note: 5 computed .brp shape members not serialized (recipe doc carries the construction recipe); baked Part::Feature solids carry a one-line shape summary decoded from their .brp

FEATURE [Sketcher::SketchObject] Sketch
  FullyConstrained = false
  MapMode = 5
  Support = -> [XY_Plane]
  sketch-geometry (8):
    g0: Circle CenterX=0 CenterY=25.7 CenterZ=0 NormalX=0 NormalY=0 NormalZ=1 AngleXU=0 Radius=1.75
    g1: Circle CenterX=0 CenterY=-25.7 CenterZ=0 NormalX=0 NormalY=0 NormalZ=1 AngleXU=0 Radius=1.75
    g2: LineSegment StartX=0 StartY=30.5 StartZ=0 EndX=-15.1903 EndY=16.5984 EndZ=0
    g3: LineSegment StartX=0 StartY=30.5 StartZ=0 EndX=15.1903 EndY=16.5984 EndZ=0
    g4: LineSegment StartX=0 StartY=-30.5 StartZ=0 EndX=-15.1925 EndY=-16.5963 EndZ=0
    g5: LineSegment StartX=0 StartY=-30.5 StartZ=0 EndX=15.1903 EndY=-16.5984 EndZ=0
    g6: ArcOfCircle CenterX=0 CenterY=0 CenterZ=0 NormalX=0 NormalY=0 NormalZ=1 AngleXU=0 Radius=22.5 StartAngle=2.31193 EndAngle=3.97112
    g7: ArcOfCircle CenterX=0 CenterY=0 CenterZ=0 NormalX=0 NormalY=0 NormalZ=1 AngleXU=0 Radius=22.5 StartAngle=5.45352 EndAngle=7.11285
  constraints (6):
    c: Coincident(g4,g6)
    c: Coincident(g4,g5)
    c: Coincident(g5,g7)
    c: Coincident(g3,g7)
    c: Coincident(g2,g3)
    c: Coincident(g2,g6)
FEATURE [PartDesign::Pad] Pad
  Direction = (0,0,1)
  Length = 26
  Length2 = 10
  Profile = -> Sketch
  ReferenceAxis = -> Sketch [N_Axis]
  Type = 0
FEATURE [PartDesign::Body] Body
  Group = -> [Sketch,Pad]
  Origin = -> Origin
  Tip = -> Pad
FEATURE [PartDesign::CoordinateSystem] LCS_0
  AttacherType = Attacher::AttachEngine3D
  MapMode = 2
  Support = -> [X_Axis001]
FEATURE [App::Part] speaker
  Group = -> [LCS_0,Body]
  Origin = -> Origin001
---- part speakerbox-L.FCStd = doc fcstd_28ac6a1aeb2d ----
FCSTD DOCUMENT  (FreeCAD 0.21R33668 +7 (Git))
Label: speakerbox-L
License: All rights reserved
LicenseURL: http://en.wikipedia.org/wiki/All_rights_reserved
objects: Sketcher::SketchObject×14, PartDesign::Pocket×11, PartDesign::Plane×4, PartDesign::Pad×2, PartDesign::CoordinateSystem×1, PartDesign::Chamfer×1, PartDesign::Body×1, App::Part×1
note: 48 computed .brp shape members not serialized (recipe doc carries the construction recipe); baked Part::Feature solids carry a one-line shape summary decoded from their .brp
EXTERNAL_REF file=planB.FCStd obj=Spreadsheet

FEATURE [Sketcher::SketchObject] Sketch
  FullyConstrained = true
  MapMode = 5
  Support = -> [XY_Plane]
  expr: Constraints[12] = planB#<<data>>.central_h + planB#<<data>>.mungo_d + 2
  sketch-geometry (10):
    g0: LineSegment StartX=0 StartY=0 StartZ=0 EndX=82 EndY=0 EndZ=0
    g1: LineSegment StartX=158.6 StartY=82 StartZ=0 EndX=7.5 EndY=82 EndZ=0
    g2: LineSegment StartX=0 StartY=74.5 StartZ=0 EndX=0 EndY=0 EndZ=0
    g3: LineSegment StartX=82 StartY=0 StartZ=0 EndX=82 EndY=23 EndZ=0
    g4: LineSegment StartX=82 StartY=23 StartZ=0 EndX=152.6 EndY=23 EndZ=0
    g5: LineSegment StartX=152.6 StartY=23 StartZ=0 EndX=152.6 EndY=77 EndZ=0
    g6: LineSegment StartX=152.6 StartY=77 StartZ=0 EndX=158.6 EndY=77 EndZ=0
    g7: LineSegment StartX=158.6 StartY=77 StartZ=0 EndX=158.6 EndY=82 EndZ=0
    g8: ArcOfCircle CenterX=7.5 CenterY=74.5 CenterZ=0 NormalX=0 NormalY=0 NormalZ=1 AngleXU=0 Radius=7.5 StartAngle=1.5708 EndAngle=3.14159
    g9: GeomPoint X=0 Y=82 Z=0
  constraints (27):
    c: Coincident(g0,g3)
    c: Coincident(g7,g1)
    c: Coincident(g2,g0)
    c: Horizontal(g0)
    c: Horizontal(g1)
    c: Vertical(g2)
    c: Coincident(g0,g-1)
    c: Coincident(g3,g4)
    c: Vertical(g3)
    c: Coincident(g4,g5)
    c: Horizontal(g4)
    c: Distance(g3) = 23
    c: Distance(g0) = 82
    c: DistanceX(g4) = 152.6
    c: Coincident(g5,g6)
    c: Vertical(g5)
    c: Coincident(g6,g7)
    c: Vertical(g7)
    c: Horizontal(g6)
    c: Distance(g6) = 6
    c: Distance(g5) = 54
    c: Distance(g7) = 5
    c: PointOnObject(g9,g1)
    c: PointOnObject(g9,g2)
    c: Tangent(g1,g8) = -1.5708
    c: Tangent(g2,g8) = -1.5708
    c: Diameter(g8) = 15
FEATURE [PartDesign::Pad] Pad
  Direction = (0,0,1)
  Length = 60
  Length2 = 10
  Profile = -> Sketch
  ReferenceAxis = -> Sketch [N_Axis]
  Type = 0
  expr: Length = planB#<<data>>.speaker_w
FEATURE [PartDesign::Plane] DatumPlane
  AttachmentOffset = pos=(0,0,5) rot=(0,0,1;0rad)
  Length = 60
  MapMode = 2
  Placement = pos=(0,0,5) rot=(0,0,1;0rad)
  ResizeMode = 0
  Support = -> [XY_Plane]
  Width = 60
  expr: .AttachmentOffset.Base.z = planB#<<data>>.base_t
FEATURE [Sketcher::SketchObject] Sketch001
  FullyConstrained = false
  MapMode = 5
  Support = -> [XY_Plane001]
  expr: Constraints[10] = planB#<<data>>.base_t
  sketch-geometry (26):
    g0: LineSegment StartX=7.90621 StartY=137.395 StartZ=0 EndX=153.6 EndY=137.395 EndZ=0
    g1: LineSegment StartX=147.6 StartY=28 StartZ=0 EndX=77 EndY=28 EndZ=0
    g2: LineSegment StartX=77 StartY=28 StartZ=0 EndX=77 EndY=5 EndZ=0
    g3: LineSegment StartX=77 StartY=5 StartZ=0 EndX=22.8287 EndY=5 EndZ=0
    g4: LineSegment StartX=153.6 StartY=137.395 StartZ=0 EndX=153.6 EndY=92 EndZ=0
    g5: LineSegment StartX=153.6 StartY=92 StartZ=0 EndX=143.6 EndY=92 EndZ=0
    g6: LineSegment StartX=7.90621 StartY=92 StartZ=0 EndX=7.90621 EndY=137.395 EndZ=0
    g7: LineSegment StartX=20 StartY=92 StartZ=0 EndX=7.90621 EndY=92 EndZ=0
    g8: LineSegment StartX=22.8287 StartY=50 StartZ=0 EndX=20 EndY=55 EndZ=0
    g9: LineSegment StartX=147.6 StartY=82.6874 StartZ=0 EndX=147.6 EndY=28 EndZ=0
    g10: LineSegment StartX=143.6 StartY=92 StartZ=0 EndX=143.6 EndY=85 EndZ=0
    g11: LineSegment StartX=143.6 StartY=85 StartZ=0 EndX=147.6 EndY=82.6874 EndZ=0
    g12: LineSegment StartX=22.8287 StartY=5 StartZ=0 EndX=22.8287 EndY=28 EndZ=0
    g13: LineSegment StartX=22.8287 StartY=28 StartZ=0 EndX=22.8287 EndY=50 EndZ=0
    g14: LineSegment StartX=22.8287 StartY=28 StartZ=0 EndX=102.6 EndY=28 EndZ=0
    g15: LineSegment StartX=102.6 StartY=28 StartZ=0 EndX=107.6 EndY=28 EndZ=0
    g16: LineSegment StartX=107.6 StartY=28 StartZ=0 EndX=77 EndY=28 EndZ=0
    g17: LineSegment StartX=102.6 StartY=28 StartZ=0 EndX=102.6 EndY=92 EndZ=0
    g18: LineSegment StartX=102.6 StartY=92 StartZ=0 EndX=107.6 EndY=92 EndZ=0
    g19: LineSegment StartX=107.6 StartY=92 StartZ=0 EndX=107.6 EndY=28 EndZ=0
    g20: Circle CenterX=18 CenterY=49 CenterZ=0 NormalX=0 NormalY=0 NormalZ=1 AngleXU=0 Radius=3
    g21: LineSegment StartX=20 StartY=55 StartZ=0 EndX=20 EndY=74 EndZ=0
    g22: LineSegment StartX=20 StartY=74 StartZ=0 EndX=20 EndY=92 EndZ=0
    g23: LineSegment StartX=20 StartY=74 StartZ=0 EndX=70 EndY=74 EndZ=0
    g24: LineSegment StartX=70 StartY=74 StartZ=0 EndX=70 EndY=92 EndZ=0
    g25: LineSegment StartX=70 StartY=92 StartZ=0 EndX=20 EndY=92 EndZ=0
  constraints (70):
    c: Coincident(g6,g0)
    c: Horizontal(g0)
    c: Coincident(g0,g4)
    c: Coincident(g9,g1)
    c: Horizontal(g1)
    c: Coincident(g1,g2)
    c: Vertical(g2)
    c: Coincident(g2,g3)
    c: Coincident(g3,g12)
    c: Horizontal(g3)
    c: DistanceY(g12) = 5
    c: DistanceX(g2) = 77
    c: DistanceX(g9) = 147.6
    c: Coincident(g4,g5)
    c: Vertical(g4)
    c: Coincident(g5,g10)
    c: Horizontal(g5)
    c: Distance(g2) = 23
    c: Coincident(g7,g6)
    c: Vertical(g6)
    c: Coincident(g22,g7)
    c: Coincident(g13,g8)
    c: Horizontal(g7)
    c: PointOnObject(g7,g5)
    c: Distance(g13,g7) = 42
    c: Coincident(g8,g21)
    c: Coincident(g11,g9)
    c: Vertical(g9)
    c: Distance(g11,g4) = 6
    c: Distance(g1,g5) = 64
    c: Distance(g5) = 10
    c: Coincident(g10,g11)
    c: Vertical(g10)
    c: Distance(g10) = 7
    c: Coincident(g12,g13)
    c: Vertical(g12)
    c: Vertical(g13)
    c: Coincident(g14,g12)
    c: Coincident(g16,g1)
    c: Coincident(g14,g15)
    c: Horizontal(g14)
    c: Coincident(g15,g16)
    c: Horizontal(g15)
    c: Horizontal(g16)
    c: Coincident(g14,g17)
    c: Vertical(g17)
    c: Coincident(g17,g18)
    c: Horizontal(g18)
    c: Coincident(g18,g19)
    c: Coincident(g19,g15)
    c: Vertical(g19)
    c: PointOnObject(g17,g7)
    c: Distance(g18) = 5
    c: Distance(g18,g9) = 40
    c: DistanceX(g20) = 18
    c: DistanceY(g20) = 49
    c: Diameter(g20) = 6
    c: Coincident(g21,g22)
    c: Distance(g21,g22) = 37
    c: Vertical(g21)
    c: Vertical(g22)
    c: Coincident(g21,g23)
    c: Horizontal(g23)
    c: Coincident(g23,g24)
    c: Vertical(g24)
    c: Coincident(g24,g25)
    c: Coincident(g25,g7)
    c: Horizontal(g25)
    c: DistanceY(g24,g24) = 18
    c: DistanceX(g24) = 70
FEATURE [PartDesign::Pocket] Pocket  label="hollow out"
  BaseFeature = -> Pad
  Direction = (0,0,-1)
  Length = 110
  Length2 = 5
  Midplane = true
  Profile = -> Sketch001
  ReferenceAxis = -> Sketch001 [N_Axis]
  Type = 0
  expr: Length = 2 * (planB#<<data>>.speaker_w - planB#<<data>>.base_t)
FEATURE [PartDesign::CoordinateSystem] LCS_0
  AttacherType = Attacher::AttachEngine3D
  MapMode = 2
  Support = -> [X_Axis001]
FEATURE [PartDesign::Plane] DatumPlane001
  AttachmentOffset = pos=(0,0,60) rot=(0,0,1;0rad)
  Length = 60
  MapMode = 5
  Placement = pos=(0,0,60) rot=(0,0,1;0rad)
  ResizeMode = 0
  Support = -> [XY_Plane]
  Width = 60
  expr: .AttachmentOffset.Base.z = planB#<<data>>.speaker_w
FEATURE [Sketcher::SketchObject] Sketch002
  FullyConstrained = false
  MapMode = 5
  Support = -> [XY_Plane001]
  expr: Constraints[0] = planB#<<data>>.clearance_m4
  expr: Constraints[16] = planB#<<data>>.L_thickness + 0.4 * 2
  expr: Constraints[17] = planB#<<data>>.L_size + 0.4 * 2
  expr: Constraints[18] = planB#<<data>>.L_size - planB#<<data>>.L_thickness
  sketch-geometry (11):
    g0: Circle CenterX=18 CenterY=49 CenterZ=0 NormalX=0 NormalY=0 NormalZ=1 AngleXU=0 Radius=2.25
    g1: LineSegment StartX=6 StartY=78.6 StartZ=0 EndX=6 EndY=56.7 EndZ=0
    g2: LineSegment StartX=6 StartY=56.7 StartZ=0 EndX=16.3 EndY=56.7 EndZ=0
    g3: LineSegment StartX=16.3 StartY=56.7 StartZ=0 EndX=16.3 EndY=70.7 EndZ=0
    g4: LineSegment StartX=16.3 StartY=70.7 StartZ=0 EndX=8.4 EndY=70.7 EndZ=0
    g5: LineSegment StartX=8.4 StartY=70.7 StartZ=0 EndX=8.4 EndY=78.6 EndZ=0
    g6: LineSegment StartX=8.4 StartY=78.6 StartZ=0 EndX=6 EndY=78.6 EndZ=0
    g7: ArcOfCircle CenterX=117.436 CenterY=40.4082 CenterZ=0 NormalX=0 NormalY=0 NormalZ=1 AngleXU=0 Radius=7.5 StartAngle=1.5708 EndAngle=4.71239
    g8: ArcOfCircle CenterX=137.436 CenterY=40.4082 CenterZ=0 NormalX=0 NormalY=0 NormalZ=1 AngleXU=0 Radius=7.5 StartAngle=4.71239 EndAngle=7.85398
    g9: LineSegment StartX=117.436 StartY=32.9082 StartZ=0 EndX=137.436 EndY=32.9082 EndZ=0
    g10: LineSegment StartX=137.436 StartY=47.9082 StartZ=0 EndX=117.436 EndY=47.9082 EndZ=0
  constraints (29):
    c: Diameter(g0) = 4.5
    c: Vertical(g1)
    c: Coincident(g1,g2)
    c: Horizontal(g2)
    c: Coincident(g2,g3)
    c: Vertical(g3)
    c: Coincident(g3,g4)
    c: Horizontal(g4)
    c: Coincident(g4,g5)
    c: Vertical(g5)
    c: Coincident(g5,g6)
    c: Coincident(g6,g1)
    c: Horizontal(g6)
    c: DistanceX(g0) = 18
    c: DistanceY(g0) = 49
    c: DistanceX(g1) = 6
    c: Distance(g6) = 2.4
    c: Distance(g2) = 10.3
    c: Distance(g5) = 7.9
    c: Distance(g3) = 14
    c: DistanceY(g1) = 78.6
    c: Tangent(g7,g9) = -1.5708
    c: Tangent(g9,g8) = -1.5708
    c: Tangent(g8,g10) = -1.5708
    c: Tangent(g10,g7) = -1.5708
    c: Equal(g7,g8)
    c: Horizontal(g9)
    c: Distance(g9) = 20
    c: Distance(g7,g10) = 15
FEATURE [Sketcher::SketchObject] Sketch003
  FullyConstrained = false
  MapMode = 5
  Support = -> [XY_Plane001]
  sketch-geometry (4):
    g0: LineSegment StartX=5 StartY=0 StartZ=0 EndX=82.9999 EndY=0 EndZ=0
    g1: LineSegment StartX=82.9999 StartY=0 StartZ=0 EndX=82.9999 EndY=23 EndZ=0
    g2: LineSegment StartX=82.9999 StartY=23 StartZ=0 EndX=5 EndY=23 EndZ=0
    g3: LineSegment StartX=5 StartY=23 StartZ=0 EndX=5 EndY=0 EndZ=0
  constraints (11):
    c: Coincident(g0,g1)
    c: Coincident(g1,g2)
    c: Coincident(g2,g3)
    c: Coincident(g3,g0)
    c: Horizontal(g0)
    c: Horizontal(g2)
    c: Vertical(g1)
    c: Vertical(g3)
    c: Distance(g1) = 23
    c: PointOnObject(g0,g-1)
    c: DistanceX(g0) = 5
FEATURE [Sketcher::SketchObject] Sketch004
  FullyConstrained = true
  MapMode = 5
  Placement = pos=(0,0,0) rot=(1,0,0;1.5708rad)
  Support = -> [XZ_Plane]
  expr: Constraints[3] = planB#<<data>>.speaker_w - 8
  expr: Constraints[5] = planB#<<data>>.insert_diameter
  sketch-geometry (4):
    g0: Circle CenterX=12 CenterY=52 CenterZ=0 NormalX=0 NormalY=0 NormalZ=1 AngleXU=0 Radius=2.15
    g1: Circle CenterX=70 CenterY=52 CenterZ=0 NormalX=0 NormalY=0 NormalZ=1 AngleXU=0 Radius=2.15
    g2: LineSegment StartX=12 StartY=52 StartZ=0 EndX=70 EndY=52 EndZ=0
    g3: Circle CenterX=99 CenterY=52 CenterZ=0 NormalX=0 NormalY=0 NormalZ=1 AngleXU=0 Radius=2.15
  constraints (11):
    c: Coincident(g2,g0)
    c: Coincident(g2,g1)
    c: Horizontal(g2)
    c: DistanceY(g-1,g0) = 52
    c: Equal(g0,g1)
    c: Diameter(g1) = 4.3
    c: DistanceX(g0) = 12
    c: DistanceX(g1) = 70
    c: PointOnObject(g3,g2)
    c: Equal(g1,g3)
    c: DistanceX(g3) = 99
FEATURE [PartDesign::Plane] DatumPlane002
  AttachmentOffset = pos=(0,0,138) rot=(0,0,1;0rad)
  Length = 60
  MapMode = 5
  Placement = pos=(138,-3.06e-14,3.06e-14) rot=(0.57735,0.57735,0.57735;2.0944rad)
  ResizeMode = 0
  Support = -> [YZ_Plane]
  Width = 60
FEATURE [Sketcher::SketchObject] Sketch005
  FullyConstrained = true
  MapMode = 5
  Placement = pos=(138,-3.06e-14,3.06e-14) rot=(0.57735,0.57735,0.57735;2.0944rad)
  Support = -> [DatumPlane002]
  expr: Constraints[1] = planB#<<data>>.insert_diameter
  expr: Constraints[5] = planB#<<data>>.speaker_w - 8
  sketch-geometry (3):
    g0: Circle CenterX=35 CenterY=52 CenterZ=0 NormalX=0 NormalY=0 NormalZ=1 AngleXU=0 Radius=2.15
    g1: Circle CenterX=65 CenterY=52 CenterZ=0 NormalX=0 NormalY=0 NormalZ=1 AngleXU=0 Radius=2.15
    g2: LineSegment StartX=35 StartY=52 StartZ=0 EndX=65 EndY=52 EndZ=0
  constraints (8):
    c: Equal(g1,g0)
    c: Diameter(g1) = 4.3
    c: Coincident(g2,g0)
    c: Coincident(g2,g1)
    c: Horizontal(g2)
    c: DistanceY(g-1,g0) = 52
    c: DistanceX(g0) = 35
    c: DistanceX(g1) = 65
FEATURE [Sketcher::SketchObject] Sketch006
  FullyConstrained = true
  MapMode = 5
  Placement = pos=(138,-3.06e-14,3.06e-14) rot=(0.57735,0.57735,0.57735;2.0944rad)
  Support = -> [DatumPlane002]
  expr: Constraints[5] = planB#<<data>>.speaker_w - 8
  sketch-geometry (3):
    g0: Circle CenterX=35 CenterY=52 CenterZ=0 NormalX=0 NormalY=0 NormalZ=1 AngleXU=0 Radius=4
    g1: Circle CenterX=65 CenterY=52 CenterZ=0 NormalX=0 NormalY=0 NormalZ=1 AngleXU=0 Radius=4
    g2: LineSegment StartX=35 StartY=52 StartZ=0 EndX=65 EndY=52 EndZ=0
  constraints (8):
    c: Equal(g1,g0)
    c: Diameter(g1) = 8
    c: Coincident(g2,g0)
    c: Coincident(g2,g1)
    c: Horizontal(g2)
    c: DistanceY(g-1,g0) = 52
    c: DistanceX(g0) = 35
    c: DistanceX(g1) = 65
FEATURE [Sketcher::SketchObject] Sketch009
  FullyConstrained = true
  MapMode = 5
  Placement = pos=(0,0,60) rot=(0,0,1;0rad)
  Support = -> [DatumPlane001]
  expr: Constraints[13] = planB#<<data>>.L_thickness + 0.4 * 2
  expr: Constraints[14] = planB#<<data>>.L_size + 0.4 * 2
  expr: Constraints[15] = planB#<<data>>.L_size - planB#<<data>>.L_thickness
  sketch-geometry (6):
    g0: LineSegment StartX=6 StartY=78.6 StartZ=0 EndX=6 EndY=56.7 EndZ=0
    g1: LineSegment StartX=6 StartY=56.7 StartZ=0 EndX=16.3 EndY=56.7 EndZ=0
    g2: LineSegment StartX=16.3 StartY=56.7 StartZ=0 EndX=16.3 EndY=70.7 EndZ=0
    g3: LineSegment StartX=16.3 StartY=70.7 StartZ=0 EndX=8.4 EndY=70.7 EndZ=0
    g4: LineSegment StartX=8.4 StartY=70.7 StartZ=0 EndX=8.4 EndY=78.6 EndZ=0
    g5: LineSegment StartX=8.4 StartY=78.6 StartZ=0 EndX=6 EndY=78.6 EndZ=0
  constraints (18):
    c: Vertical(g0)
    c: Coincident(g0,g1)
    c: Horizontal(g1)
    c: Coincident(g1,g2)
    c: Vertical(g2)
    c: Coincident(g2,g3)
    c: Horizontal(g3)
    c: Coincident(g3,g4)
    c: Vertical(g4)
    c: Coincident(g4,g5)
    c: Coincident(g5,g0)
    c: Horizontal(g5)
    c: DistanceX(g0) = 6
    c: Distance(g5) = 2.4
    c: Distance(g1) = 10.3
    c: Distance(g4) = 7.9
    c: Distance(g2) = 14
    c: DistanceY(g0) = 78.6
FEATURE [Sketcher::SketchObject] Sketch010
  FullyConstrained = true
  MapMode = 5
  Placement = pos=(0,0,60) rot=(0,0,1;0rad)
  Support = -> [DatumPlane001]
  sketch-geometry (4):
    g0: LineSegment StartX=7 StartY=78.6 StartZ=0 EndX=16.3 EndY=78.6 EndZ=0
    g1: LineSegment StartX=16.3 StartY=78.6 StartZ=0 EndX=16.3 EndY=57.7 EndZ=0
    g2: LineSegment StartX=16.3 StartY=57.7 StartZ=0 EndX=7 EndY=57.7 EndZ=0
    g3: LineSegment StartX=7 StartY=57.7 StartZ=0 EndX=7 EndY=78.6 EndZ=0
  constraints (12):
    c: Coincident(g0,g1)
    c: Coincident(g1,g2)
    c: Coincident(g2,g3)
    c: Coincident(g3,g0)
    c: Horizontal(g0)
    c: Horizontal(g2)
    c: Vertical(g1)
    c: Vertical(g3)
    c: DistanceX(g0) = 7
    c: DistanceY(g0) = 78.6
    c: DistanceX(g1) = 16.3
    c: DistanceY(g1) = 57.7
FEATURE [PartDesign::Plane] DatumPlane003
  AttachmentOffset = pos=(0,0,100) rot=(0,0,1;0rad)
  Length = 60
  MapMode = 5
  Placement = pos=(0,100,2.22e-14) rot=(0,0.707107,0.707107;3.14159rad)
  ResizeMode = 0
  Support = -> [XZ_Plane]
  Width = 60
FEATURE [Sketcher::SketchObject] Sketch011
  FullyConstrained = true
  MapMode = 5
  Placement = pos=(0,100,2.22e-14) rot=(0,0.707107,0.707107;3.14159rad)
  Support = -> [DatumPlane003]
  sketch-geometry (10):
    g0: Circle CenterX=-152.6 CenterY=50 CenterZ=0 NormalX=0 NormalY=0 NormalZ=1 AngleXU=0 Radius=3.2
    g1: LineSegment StartX=-152.6 StartY=50 StartZ=0 EndX=-14 EndY=50 EndZ=0
    g2: LineSegment StartX=-14 StartY=50 StartZ=0 EndX=-14 EndY=10 EndZ=0
    g3: LineSegment StartX=-14 StartY=10 StartZ=0 EndX=-152.6 EndY=10 EndZ=0
    g4: LineSegment StartX=-152.6 StartY=10 StartZ=0 EndX=-152.6 EndY=50 EndZ=0
    g5: Circle CenterX=-152.6 CenterY=10 CenterZ=0 NormalX=0 NormalY=0 NormalZ=1 AngleXU=0 Radius=3.2
    g6: Circle CenterX=-14 CenterY=10 CenterZ=0 NormalX=0 NormalY=0 NormalZ=1 AngleXU=0 Radius=3.2
    g7: Circle CenterX=-14 CenterY=50 CenterZ=0 NormalX=0 NormalY=0 NormalZ=1 AngleXU=0 Radius=3.2
    g8: Circle CenterX=-35 CenterY=27.5 CenterZ=0 NormalX=0 NormalY=0 NormalZ=1 AngleXU=0 Radius=4.5
    g9: Circle CenterX=-63 CenterY=15 CenterZ=0 NormalX=0 NormalY=0 NormalZ=1 AngleXU=0 Radius=3.5
  constraints (26):
    c: Coincident(g1,g2)
    c: Coincident(g2,g3)
    c: Coincident(g3,g4)
    c: Coincident(g4,g1)
    c: Horizontal(g1)
    c: Horizontal(g3)
    c: Vertical(g2)
    c: Vertical(g4)
    c: Coincident(g1,g0)
    c: Coincident(g5,g3)
    c: Coincident(g6,g2)
    c: Coincident(g7,g1)
    c: Equal(g0,g7)
    c: Equal(g7,g6)
    c: Equal(g6,g5)
    c: Diameter(g6) = 6.4
    c: DistanceY(g5) = 10
    c: DistanceX(g6) = -14
    c: DistanceY(g4,g4) = 40
    c: DistanceX(g5) = -152.6
    c: DistanceX(g8) = -35
    c: Diameter(g8) = 9
    c: DistanceY(g8) = 27.5
    c: Diameter(g9) = 7
    c: DistanceY(g9) = 15
    c: DistanceX(g9) = -63
FEATURE [Sketcher::SketchObject] Sketch012
  FullyConstrained = true
  MapMode = 5
  Placement = pos=(0,0,60) rot=(0,0,1;0rad)
  Support = -> [DatumPlane001]
  sketch-geometry (1):
    g0: Circle CenterX=18 CenterY=49 CenterZ=0 NormalX=0 NormalY=0 NormalZ=1 AngleXU=0 Radius=8
  constraints (3):
    c: Diameter(g0) = 16
    c: DistanceX(g0) = 18
    c: DistanceY(g0) = 49
FEATURE [Sketcher::SketchObject] Sketch013
  FullyConstrained = true
  MapMode = 5
  Placement = pos=(0,0,60) rot=(0,0,1;0rad)
  Support = -> [DatumPlane001]
  sketch-geometry (1):
    g0: Circle CenterX=18 CenterY=49 CenterZ=0 NormalX=0 NormalY=0 NormalZ=1 AngleXU=0 Radius=12
  constraints (3):
    c: DistanceX(g0) = 18
    c: DistanceY(g0) = 49
    c: Diameter(g0) = 24
FEATURE [PartDesign::Pad] Pad001
  BaseFeature = -> Pocket
  Direction = (0,0,1)
  Length = 16
  Length2 = 10
  Profile = -> Sketch013
  ReferenceAxis = -> Sketch013 [N_Axis]
  Reversed = true
  Type = 0
FEATURE [PartDesign::Pocket] Pocket001  label="threaded rod, power outlet"
  BaseFeature = -> Pad001
  Direction = (0,0,-1)
  Length = 30
  Length2 = 5
  Profile = -> Sketch002
  ReferenceAxis = -> Sketch002 [N_Axis]
  Reversed = true
  Type = 1
FEATURE [PartDesign::Pocket] Pocket008  label="L hole"
  BaseFeature = -> Pocket001
  Direction = (0,0,-1)
  Length = 156
  Length2 = 5
  Midplane = true
  Profile = -> Sketch009
  ReferenceAxis = -> Sketch009 [N_Axis]
  Type = 1
FEATURE [PartDesign::Pocket] Pocket002  label="hollow for psu"
  BaseFeature = -> Pocket008
  Direction = (0,0,-1)
  Length = 44
  Length2 = 5
  Profile = -> Sketch003
  ReferenceAxis = -> Sketch003 [N_Axis]
  Reversed = true
  Type = 0
  expr: Length = planB#<<data>>.speaker_w - 16
FEATURE [PartDesign::Pocket] Pocket004  label="side screwholes"
  BaseFeature = -> Pocket002
  Direction = (-1,1e-16,-1e-16)
  Length = 9
  Length2 = 5
  Profile = -> Sketch005
  ReferenceAxis = -> Sketch005 [N_Axis]
  Reversed = true
  Type = 1
FEATURE [PartDesign::Pocket] Pocket009
  BaseFeature = -> Pocket004
  Direction = (0,0,-1)
  Length = 5
  Length2 = 5
  Profile = -> Sketch010
  ReferenceAxis = -> Sketch010 [N_Axis]
  Type = 0
FEATURE [PartDesign::Pocket] Pocket010  label="volume knob hole"
  BaseFeature = -> Pocket009
  Direction = (0,-1,-2e-16)
  Length = 32
  Length2 = 5
  Profile = -> Sketch011
  ReferenceAxis = -> Sketch011 [N_Axis]
  Type = 0
FEATURE [PartDesign::Pocket] Pocket003  label="bottom screwholes"
  BaseFeature = -> Pocket010
  Direction = (0,1,2e-16)
  Length = 34
  Length2 = 5
  Profile = -> Sketch004
  ReferenceAxis = -> Sketch004 [N_Axis]
  Type = 0
FEATURE [PartDesign::Pocket] Pocket011
  BaseFeature = -> Pocket003
  Direction = (0,0,-1)
  Length = 16
  Length2 = 5
  Midplane = true
  Profile = -> Sketch012
  ReferenceAxis = -> Sketch012 [N_Axis]
  Type = 0
FEATURE [PartDesign::Chamfer] Chamfer
  Angle = 45
  Base = -> Pocket011 [Edge7,Edge8]
  BaseFeature = -> Pocket011
  ChamferType = 0
  FlipDirection = false
  Size = 1
  Size2 = 1
  SupportTransform = false
  UseAllEdges = false
FEATURE [Sketcher::SketchObject] Sketch014
  FullyConstrained = false
  MapMode = 5
  Placement = pos=(0,0,0) rot=(1,0,0;1.5708rad)
  Support = -> [XZ_Plane]
  sketch-geometry (4):
    g0: LineSegment StartX=22 StartY=44 StartZ=0 EndX=138 EndY=44 EndZ=0
    g1: LineSegment StartX=138 StartY=44 StartZ=0 EndX=138 EndY=-30.3457 EndZ=0
    g2: LineSegment StartX=138 StartY=-30.3457 StartZ=0 EndX=22 EndY=-30.3457 EndZ=0
    g3: LineSegment StartX=22 StartY=-30.3457 StartZ=0 EndX=22 EndY=44 EndZ=0
  constraints (11):
    c: Coincident(g0,g1)
    c: Coincident(g1,g2)
    c: Coincident(g2,g3)
    c: Coincident(g3,g0)
    c: Horizontal(g0)
    c: Horizontal(g2)
    c: Vertical(g1)
    c: Vertical(g3)
    c: DistanceY(g0) = 44
    c: DistanceX(g0) = 22
    c: DistanceX(g0) = 138
FEATURE [PartDesign::Pocket] Pocket012
  BaseFeature = -> Chamfer
  Direction = (0,1,2e-16)
  Length = 37
  Length2 = 5
  Profile = -> Sketch014
  ReferenceAxis = -> Sketch014 [N_Axis]
  Type = 0
FEATURE [Sketcher::SketchObject] Sketch015
  FullyConstrained = true
  MapMode = 5
  Placement = pos=(0,100,2.22e-14) rot=(0,0.707107,0.707107;3.14159rad)
  Support = -> [DatumPlane003]
  sketch-geometry (1):
    g0: Circle CenterX=-35 CenterY=27.6 CenterZ=0 NormalX=0 NormalY=0 NormalZ=1 AngleXU=0 Radius=12.5
  constraints (3):
    c: DistanceX(g0) = -35
    c: DistanceY(g0) = 27.6
    c: Diameter(g0) = 25
FEATURE [PartDesign::Pocket] Pocket013
  BaseFeature = -> Pocket012
  Direction = (0,-1,-2e-16)
  Length = 22
  Length2 = 5
  Profile = -> Sketch015
  ReferenceAxis = -> Sketch015 [N_Axis]
  Type = 0
FEATURE [PartDesign::Body] Body
  Group = -> [Sketch,Pad,DatumPlane,Sketch001,Pocket,DatumPlane001,Pad001,Sketch002,Pocket001,Pocket008,Sketch003,Pocket002,Sketch004,DatumPlane002,Sketch005,Pocket004,Sketch006,Sketch009,Sketch010,Pocket009,DatumPlane003,Sketch011,Pocket010,Pocket003,Sketch012,Pocket011,Sketch013,Chamfer,Sketch014,Pocket012,Sketch015,Pocket013]
  Origin = -> Origin
  Tip = -> Pocket013
FEATURE [App::Part] speakerbox  label="speakerbox-L"
  Group = -> [LCS_0,Body]
  Origin = -> Origin001
---- part speakerbox.FCStd = doc fcstd_504be9c8a76e ----
FCSTD DOCUMENT  (FreeCAD 0.21R33668 +7 (Git))
Label: speakerbox
License: All rights reserved
LicenseURL: http://en.wikipedia.org/wiki/All_rights_reserved
objects: Sketcher::SketchObject×13, PartDesign::Pocket×12, PartDesign::Plane×3, PartDesign::Pad×1, PartDesign::CoordinateSystem×1, PartDesign::Chamfer×1, PartDesign::Body×1, App::Part×1
note: 46 computed .brp shape members not serialized (recipe doc carries the construction recipe); baked Part::Feature solids carry a one-line shape summary decoded from their .brp
EXTERNAL_REF file=planB.FCStd obj=Spreadsheet

FEATURE [Sketcher::SketchObject] Sketch
  FullyConstrained = true
  MapMode = 5
  Support = -> [XY_Plane]
  expr: Constraints[12] = planB#<<data>>.central_h + planB#<<data>>.mungo_d + 2
  sketch-geometry (10):
    g0: LineSegment StartX=0 StartY=0 StartZ=0 EndX=82 EndY=0 EndZ=0
    g1: LineSegment StartX=158.6 StartY=82 StartZ=0 EndX=7.5 EndY=82 EndZ=0
    g2: LineSegment StartX=0 StartY=74.5 StartZ=0 EndX=0 EndY=0 EndZ=0
    g3: LineSegment StartX=82 StartY=0 StartZ=0 EndX=82 EndY=37 EndZ=0
    g4: LineSegment StartX=82 StartY=37 StartZ=0 EndX=152.6 EndY=37 EndZ=0
    g5: LineSegment StartX=152.6 StartY=37 StartZ=0 EndX=152.6 EndY=77 EndZ=0
    g6: LineSegment StartX=152.6 StartY=77 StartZ=0 EndX=158.6 EndY=77 EndZ=0
    g7: LineSegment StartX=158.6 StartY=77 StartZ=0 EndX=158.6 EndY=82 EndZ=0
    g8: ArcOfCircle CenterX=7.5 CenterY=74.5 CenterZ=0 NormalX=0 NormalY=0 NormalZ=1 AngleXU=0 Radius=7.5 StartAngle=1.5708 EndAngle=3.14159
    g9: GeomPoint X=0 Y=82 Z=0
  constraints (27):
    c: Coincident(g0,g3)
    c: Coincident(g7,g1)
    c: Coincident(g2,g0)
    c: Horizontal(g0)
    c: Horizontal(g1)
    c: Vertical(g2)
    c: Coincident(g0,g-1)
    c: Coincident(g3,g4)
    c: Vertical(g3)
    c: Coincident(g4,g5)
    c: Horizontal(g4)
    c: Distance(g3) = 37
    c: Distance(g0) = 82
    c: DistanceX(g4) = 152.6
    c: Coincident(g5,g6)
    c: Vertical(g5)
    c: Coincident(g6,g7)
    c: Vertical(g7)
    c: Horizontal(g6)
    c: Distance(g6) = 6
    c: Distance(g7) = 5
    c: DistanceY(g6) = 77
    c: PointOnObject(g9,g1)
    c: PointOnObject(g9,g2)
    c: Tangent(g1,g8) = -1.5708
    c: Tangent(g2,g8) = -1.5708
    c: Diameter(g8) = 15
FEATURE [PartDesign::Pad] Pad
  Direction = (0,0,1)
  Length = 60
  Length2 = 10
  Profile = -> Sketch
  ReferenceAxis = -> Sketch [N_Axis]
  Type = 0
  expr: Length = planB#<<data>>.speaker_w
FEATURE [PartDesign::Plane] DatumPlane
  AttachmentOffset = pos=(0,0,5) rot=(0,0,1;0rad)
  Length = 211.632
  MapMode = 2
  Placement = pos=(0,0,5) rot=(0,0,1;0rad)
  ResizeMode = 0
  Support = -> [XY_Plane]
  Width = 135.032
  expr: .AttachmentOffset.Base.z = planB#<<data>>.base_t
FEATURE [Sketcher::SketchObject] Sketch001
  FullyConstrained = false
  MapMode = 5
  Placement = pos=(0,0,5) rot=(0,0,1;0rad)
  Support = -> [DatumPlane]
  sketch-geometry (15):
    g0: LineSegment StartX=5 StartY=129.209 StartZ=0 EndX=153.6 EndY=129.209 EndZ=0
    g1: LineSegment StartX=77 StartY=42 StartZ=0 EndX=77 EndY=5 EndZ=0
    g2: LineSegment StartX=153.6 StartY=129.209 StartZ=0 EndX=153.6 EndY=93.7761 EndZ=0
    g3: LineSegment StartX=153.6 StartY=93.7761 StartZ=0 EndX=143.6 EndY=93.7761 EndZ=0
    g4: LineSegment StartX=5 StartY=93.7761 StartZ=0 EndX=5 EndY=129.209 EndZ=0
    g5: LineSegment StartX=20 StartY=93.7761 StartZ=0 EndX=5 EndY=93.7761 EndZ=0
    g6: LineSegment StartX=23.5636 StartY=53.7761 StartZ=0 EndX=20 EndY=56.7761 EndZ=0
    g7: LineSegment StartX=20 StartY=56.7761 StartZ=0 EndX=20 EndY=93.7761 EndZ=0
    g8: LineSegment StartX=147.6 StartY=82.69 StartZ=0 EndX=147.6 EndY=42 EndZ=0
    g9: LineSegment StartX=143.6 StartY=93.7761 StartZ=0 EndX=143.6 EndY=86.7761 EndZ=0
    g10: LineSegment StartX=143.6 StartY=86.7761 StartZ=0 EndX=147.6 EndY=82.69 EndZ=0
    g11: LineSegment StartX=23.5636 StartY=42 StartZ=0 EndX=77 EndY=42 EndZ=0
    g12: LineSegment StartX=77 StartY=42 StartZ=0 EndX=77 EndY=42 EndZ=0
    g13: LineSegment StartX=77 StartY=42 StartZ=0 EndX=147.6 EndY=42 EndZ=0
    g14: LineSegment StartX=23.5636 StartY=42 StartZ=0 EndX=23.5636 EndY=53.7761 EndZ=0
  constraints (39):
    c: Coincident(g4,g0)
    c: Horizontal(g0)
    c: Coincident(g0,g2)
    c: Vertical(g1)
    c: DistanceX(g1) = 77
    c: DistanceX(g8) = 147.6
    c: Coincident(g2,g3)
    c: Vertical(g2)
    c: Coincident(g3,g9)
    c: Horizontal(g3)
    c: Distance(g1) = 37
    c: Coincident(g5,g4)
    c: Vertical(g4)
    c: Coincident(g7,g5)
    c: Horizontal(g5)
    c: PointOnObject(g5,g3)
    c: Coincident(g6,g7)
    c: Distance(g7) = 37
    c: Vertical(g7)
    c: Coincident(g10,g8)
    c: Vertical(g8)
    c: Distance(g10,g2) = 6
    c: Distance(g3) = 10
    c: Coincident(g9,g10)
    c: Vertical(g9)
    c: Distance(g9) = 7
    c: DistanceX(g-2,g4) = 5
    c: DistanceX(g5,g5) = 15
    c: DistanceY(g8) = 82.69
    c: PointOnObject(g11,g1)
    c: Horizontal(g11)
    c: Coincident(g11,g12)
    c: Coincident(g13,g12)
    c: Coincident(g13,g8)
    c: Horizontal(g13)
    c: Coincident(g14,g6)
    c: Vertical(g14)
    c: Distance(g6,g5) = 40
    c: Coincident(g14,g11)
FEATURE [PartDesign::Pocket] Pocket  label="hollow out"
  BaseFeature = -> Pad
  Direction = (0,0,-1)
  Length = 50
  Length2 = 5
  Profile = -> Sketch001
  ReferenceAxis = -> Sketch001 [N_Axis]
  Reversed = true
  Type = 1
  expr: Length = planB#<<data>>.speaker_w - 2 * planB#<<data>>.base_t
FEATURE [PartDesign::CoordinateSystem] LCS_0
  AttacherType = Attacher::AttachEngine3D
  MapMode = 2
  Support = -> [X_Axis001]
FEATURE [PartDesign::Plane] DatumPlane001
  AttachmentOffset = pos=(0,0,60) rot=(0,0,1;0rad)
  Length = 211.632
  MapMode = 5
  Placement = pos=(0,0,60) rot=(0,0,1;0rad)
  ResizeMode = 0
  Support = -> [XY_Plane]
  Width = 135.032
  expr: .AttachmentOffset.Base.z = planB#<<data>>.speaker_w
FEATURE [Sketcher::SketchObject] Sketch002
  FullyConstrained = false
  MapMode = 5
  Placement = pos=(0,0,60) rot=(0,0,1;0rad)
  Support = -> [DatumPlane001]
  expr: Constraints[0] = planB#<<data>>.clearance_m4
  expr: Constraints[16] = planB#<<data>>.L_thickness + 0.4 * 2
  expr: Constraints[17] = planB#<<data>>.L_size + 0.4 * 2
  expr: Constraints[18] = planB#<<data>>.L_size - planB#<<data>>.L_thickness
  sketch-geometry (11):
    g0: Circle CenterX=18 CenterY=49 CenterZ=0 NormalX=0 NormalY=0 NormalZ=1 AngleXU=0 Radius=2.25
    g1: LineSegment StartX=6 StartY=78.6 StartZ=0 EndX=6 EndY=56.7 EndZ=0
    g2: LineSegment StartX=6 StartY=56.7 StartZ=0 EndX=16.3 EndY=56.7 EndZ=0
    g3: LineSegment StartX=16.3 StartY=56.7 StartZ=0 EndX=16.3 EndY=70.7 EndZ=0
    g4: LineSegment StartX=16.3 StartY=70.7 StartZ=0 EndX=8.4 EndY=70.7 EndZ=0
    g5: LineSegment StartX=8.4 StartY=70.7 StartZ=0 EndX=8.4 EndY=78.6 EndZ=0
    g6: LineSegment StartX=8.4 StartY=78.6 StartZ=0 EndX=6 EndY=78.6 EndZ=0
    g7: ArcOfCircle CenterX=117.436 CenterY=40.4082 CenterZ=0 NormalX=0 NormalY=0 NormalZ=1 AngleXU=0 Radius=7.5 StartAngle=1.5708 EndAngle=4.71239
    g8: ArcOfCircle CenterX=137.436 CenterY=40.4082 CenterZ=0 NormalX=0 NormalY=0 NormalZ=1 AngleXU=0 Radius=7.5 StartAngle=4.71239 EndAngle=7.85398
    g9: LineSegment StartX=117.436 StartY=32.9082 StartZ=0 EndX=137.436 EndY=32.9082 EndZ=0
    g10: LineSegment StartX=137.436 StartY=47.9082 StartZ=0 EndX=117.436 EndY=47.9082 EndZ=0
  constraints (29):
    c: Diameter(g0) = 4.5
    c: Vertical(g1)
    c: Coincident(g1,g2)
    c: Horizontal(g2)
    c: Coincident(g2,g3)
    c: Vertical(g3)
    c: Coincident(g3,g4)
    c: Horizontal(g4)
    c: Coincident(g4,g5)
    c: Vertical(g5)
    c: Coincident(g5,g6)
    c: Coincident(g6,g1)
    c: Horizontal(g6)
    c: DistanceX(g0) = 18
    c: DistanceY(g0) = 49
    c: DistanceX(g1) = 6
    c: Distance(g6) = 2.4
    c: Distance(g2) = 10.3
    c: Distance(g5) = 7.9
    c: Distance(g3) = 14
    c: DistanceY(g1) = 78.6
    c: Tangent(g7,g9) = -1.5708
    c: Tangent(g9,g8) = -1.5708
    c: Tangent(g8,g10) = -1.5708
    c: Tangent(g10,g7) = -1.5708
    c: Equal(g7,g8)
    c: Horizontal(g9)
    c: Distance(g9) = 20
    c: Distance(g7,g10) = 15
FEATURE [PartDesign::Pocket] Pocket001  label="threaded rod, power outlet"
  BaseFeature = -> Pocket
  Direction = (0,0,-1)
  Length = 57
  Length2 = 5
  Profile = -> Sketch002
  ReferenceAxis = -> Sketch002 [N_Axis]
  Type = 0
FEATURE [Sketcher::SketchObject] Sketch003
  FullyConstrained = false
  MapMode = 5
  Placement = pos=(0,0,60) rot=(0,0,1;0rad)
  Support = -> [DatumPlane001]
  sketch-geometry (4):
    g0: LineSegment StartX=10 StartY=0 StartZ=0 EndX=82.9999 EndY=0 EndZ=0
    g1: LineSegment StartX=82.9999 StartY=0 StartZ=0 EndX=82.9999 EndY=32 EndZ=0
    g2: LineSegment StartX=82.9999 StartY=32 StartZ=0 EndX=10 EndY=32 EndZ=0
    g3: LineSegment StartX=10 StartY=32 StartZ=0 EndX=10 EndY=0 EndZ=0
  constraints (11):
    c: Coincident(g0,g1)
    c: Coincident(g1,g2)
    c: Coincident(g2,g3)
    c: Coincident(g3,g0)
    c: Horizontal(g0)
    c: Horizontal(g2)
    c: Vertical(g1)
    c: Vertical(g3)
    c: Distance(g1) = 32
    c: PointOnObject(g0,g-1)
    c: DistanceX(g0) = 10
FEATURE [Sketcher::SketchObject] Sketch004
  FullyConstrained = true
  MapMode = 5
  Placement = pos=(0,0,0) rot=(1,0,0;1.5708rad)
  Support = -> [XZ_Plane]
  expr: Constraints[5] = planB#<<data>>.insert_diameter
  sketch-geometry (4):
    g0: Circle CenterX=12 CenterY=8 CenterZ=0 NormalX=0 NormalY=0 NormalZ=1 AngleXU=0 Radius=2.15
    g1: Circle CenterX=70 CenterY=8 CenterZ=0 NormalX=0 NormalY=0 NormalZ=1 AngleXU=0 Radius=2.15
    g2: LineSegment StartX=12 StartY=8 StartZ=0 EndX=70 EndY=8 EndZ=0
    g3: Circle CenterX=98 CenterY=8 CenterZ=0 NormalX=0 NormalY=0 NormalZ=1 AngleXU=0 Radius=2.15
  constraints (11):
    c: Coincident(g2,g0)
    c: Coincident(g2,g1)
    c: Horizontal(g2)
    c: DistanceY(g-1,g0) = 8
    c: Equal(g0,g1)
    c: Diameter(g1) = 4.3
    c: DistanceX(g0) = 12
    c: DistanceX(g1) = 70
    c: PointOnObject(g3,g2)
    c: Equal(g1,g3)
    c: DistanceX(g3) = 98
FEATURE [PartDesign::Plane] DatumPlane002
  AttachmentOffset = pos=(0,0,138) rot=(0,0,1;0rad)
  Length = 126.074
  MapMode = 5
  Placement = pos=(138,-3.06e-14,3.06e-14) rot=(0.57735,0.57735,0.57735;2.0944rad)
  ResizeMode = 0
  Support = -> [YZ_Plane]
  Width = 104.074
FEATURE [Sketcher::SketchObject] Sketch005
  FullyConstrained = true
  MapMode = 5
  Placement = pos=(138,-3.06e-14,3.06e-14) rot=(0.57735,0.57735,0.57735;2.0944rad)
  Support = -> [DatumPlane002]
  expr: Constraints[1] = planB#<<data>>.clearance_m3
  sketch-geometry (3):
    g0: Circle CenterX=35 CenterY=8 CenterZ=0 NormalX=0 NormalY=0 NormalZ=1 AngleXU=0 Radius=1.75
    g1: Circle CenterX=65 CenterY=8 CenterZ=0 NormalX=0 NormalY=0 NormalZ=1 AngleXU=0 Radius=1.75
    g2: LineSegment StartX=35 StartY=8 StartZ=0 EndX=65 EndY=8 EndZ=0
  constraints (8):
    c: Equal(g1,g0)
    c: Diameter(g1) = 3.5
    c: Coincident(g2,g0)
    c: Coincident(g2,g1)
    c: Horizontal(g2)
    c: DistanceY(g-1,g0) = 8
    c: DistanceX(g0) = 35
    c: DistanceX(g1) = 65
FEATURE [Sketcher::SketchObject] Sketch006
  FullyConstrained = true
  MapMode = 5
  Placement = pos=(138,-3.06e-14,3.06e-14) rot=(0.57735,0.57735,0.57735;2.0944rad)
  Support = -> [DatumPlane002]
  sketch-geometry (3):
    g0: Circle CenterX=35 CenterY=8 CenterZ=0 NormalX=0 NormalY=0 NormalZ=1 AngleXU=0 Radius=4
    g1: Circle CenterX=65 CenterY=8 CenterZ=0 NormalX=0 NormalY=0 NormalZ=1 AngleXU=0 Radius=4
    g2: LineSegment StartX=35 StartY=8 StartZ=0 EndX=65 EndY=8 EndZ=0
  constraints (8):
    c: Equal(g1,g0)
    c: Diameter(g1) = 8
    c: Coincident(g2,g0)
    c: Coincident(g2,g1)
    c: Horizontal(g2)
    c: DistanceY(g-1,g0) = 8
    c: DistanceX(g0) = 35
    c: DistanceX(g1) = 65
FEATURE [Sketcher::SketchObject] Sketch007
  FullyConstrained = true
  MapMode = 5
  Placement = pos=(0,0,0) rot=(0.57735,0.57735,0.57735;2.0944rad)
  Support = -> [YZ_Plane]
  sketch-geometry (15):
    g0: Circle CenterX=17.5 CenterY=30 CenterZ=0 NormalX=0 NormalY=0 NormalZ=1 AngleXU=0 Radius=12
    g1: LineSegment StartX=4 StartY=46.5 StartZ=0 EndX=31 EndY=46.5 EndZ=0
    g2: LineSegment StartX=31 StartY=46.5 StartZ=0 EndX=31 EndY=13.5 EndZ=0
    g3: LineSegment StartX=31 StartY=13.5 StartZ=0 EndX=4 EndY=13.5 EndZ=0
    g4: LineSegment StartX=4 StartY=13.5 StartZ=0 EndX=4 EndY=46.5 EndZ=0
    g5: Circle CenterX=27.5 CenterY=43 CenterZ=0 NormalX=0 NormalY=0 NormalZ=1 AngleXU=0 Radius=1.75
    g6: Circle CenterX=7.5 CenterY=17 CenterZ=0 NormalX=0 NormalY=0 NormalZ=1 AngleXU=0 Radius=1.75
    g7: LineSegment StartX=7.5 StartY=17 StartZ=0 EndX=4 EndY=17 EndZ=0
    g8: LineSegment StartX=4 StartY=17 StartZ=0 EndX=4 EndY=13.5 EndZ=0
    g9: LineSegment StartX=4 StartY=13.5 StartZ=0 EndX=7.5 EndY=13.5 EndZ=0
    g10: LineSegment StartX=7.5 StartY=13.5 StartZ=0 EndX=7.5 EndY=17 EndZ=0
    g11: LineSegment StartX=27.5 StartY=43 StartZ=0 EndX=31 EndY=43 EndZ=0
    g12: LineSegment StartX=31 StartY=43 StartZ=0 EndX=31 EndY=46.5 EndZ=0
    g13: LineSegment StartX=31 StartY=46.5 StartZ=0 EndX=27.5 EndY=46.5 EndZ=0
    g14: LineSegment StartX=27.5 StartY=46.5 StartZ=0 EndX=27.5 EndY=43 EndZ=0
  constraints (40):
    c: Coincident(g1,g2)
    c: Coincident(g3,g4)
    c: Horizontal(g1)
    c: Horizontal(g3)
    c: Vertical(g2)
    c: Vertical(g4)
    c: Symmetric(g2,g1,g0)
    c: DistanceX(g1,g1) = 27
    c: DistanceY(g2,g2) = 33
    c: Diameter(g0) = 24
    c: Equal(g6,g5)
    c: Diameter(g5) = 3.5
    c: Coincident(g7,g8)
    c: Coincident(g8,g9)
    c: Coincident(g9,g10)
    c: Coincident(g10,g7)
    c: Horizontal(g7)
    c: Horizontal(g9)
    c: Vertical(g8)
    c: Vertical(g10)
    c: Coincident(g7,g6)
    c: Coincident(g8,g3)
    c: Coincident(g11,g12)
    c: Coincident(g12,g13)
    c: Coincident(g13,g14)
    c: Coincident(g14,g11)
    c: Horizontal(g11)
    c: Horizontal(g13)
    c: Vertical(g12)
    c: Vertical(g14)
    c: Coincident(g11,g5)
    c: Coincident(g12,g1)
    c: Equal(g14,g11)
    c: Equal(g11,g7)
    c: Equal(g7,g10)
    c: Distance(g10) = 3.5
    c: Coincident(g1,g4)
    c: Coincident(g2,g3)
    c: DistanceY(g0) = 30
    c: DistanceX(g0) = 17.5
FEATURE [Sketcher::SketchObject] Sketch008
  FullyConstrained = true
  MapMode = 5
  Placement = pos=(0,0,0) rot=(0.57735,0.57735,0.57735;2.0944rad)
  Support = -> [YZ_Plane]
  expr: Constraints[11] = planB#<<data>>.insert_diameter
  sketch-geometry (15):
    g0: Circle CenterX=17.5 CenterY=30 CenterZ=0 NormalX=0 NormalY=0 NormalZ=1 AngleXU=0 Radius=12
    g1: LineSegment StartX=5 StartY=45.5 StartZ=0 EndX=30 EndY=45.5 EndZ=0
    g2: LineSegment StartX=30 StartY=45.5 StartZ=0 EndX=30 EndY=14.5 EndZ=0
    g3: LineSegment StartX=30 StartY=14.5 StartZ=0 EndX=5 EndY=14.5 EndZ=0
    g4: LineSegment StartX=5 StartY=14.5 StartZ=0 EndX=5 EndY=45.5 EndZ=0
    g5: Circle CenterX=26.5 CenterY=42 CenterZ=0 NormalX=0 NormalY=0 NormalZ=1 AngleXU=0 Radius=2.15
    g6: Circle CenterX=8.5 CenterY=18 CenterZ=0 NormalX=0 NormalY=0 NormalZ=1 AngleXU=0 Radius=2.15
    g7: LineSegment StartX=8.5 StartY=18 StartZ=0 EndX=5 EndY=18 EndZ=0
    g8: LineSegment StartX=5 StartY=18 StartZ=0 EndX=5 EndY=14.5 EndZ=0
    g9: LineSegment StartX=5 StartY=14.5 StartZ=0 EndX=8.5 EndY=14.5 EndZ=0
    g10: LineSegment StartX=8.5 StartY=14.5 StartZ=0 EndX=8.5 EndY=18 EndZ=0
    g11: LineSegment StartX=26.5 StartY=42 StartZ=0 EndX=30 EndY=42 EndZ=0
    g12: LineSegment StartX=30 StartY=42 StartZ=0 EndX=30 EndY=45.5 EndZ=0
    g13: LineSegment StartX=30 StartY=45.5 StartZ=0 EndX=26.5 EndY=45.5 EndZ=0
    g14: LineSegment StartX=26.5 StartY=45.5 StartZ=0 EndX=26.5 EndY=42 EndZ=0
  constraints (40):
    c: Coincident(g1,g2)
    c: Coincident(g3,g4)
    c: Horizontal(g1)
    c: Horizontal(g3)
    c: Vertical(g2)
    c: Vertical(g4)
    c: Symmetric(g2,g1,g0)
    c: DistanceX(g1,g1) = 25
    c: DistanceY(g2,g2) = 31
    c: Diameter(g0) = 24
    c: Equal(g6,g5)
    c: Diameter(g5) = 4.3
    c: Coincident(g7,g8)
    c: Coincident(g8,g9)
    c: Coincident(g9,g10)
    c: Coincident(g10,g7)
    c: Horizontal(g7)
    c: Horizontal(g9)
    c: Vertical(g8)
    c: Vertical(g10)
    c: Coincident(g7,g6)
    c: Coincident(g8,g3)
    c: Coincident(g11,g12)
    c: Coincident(g12,g13)
    c: Coincident(g13,g14)
    c: Coincident(g14,g11)
    c: Horizontal(g11)
    c: Horizontal(g13)
    c: Vertical(g12)
    c: Vertical(g14)
    c: Coincident(g11,g5)
    c: Coincident(g12,g1)
    c: Equal(g14,g11)
    c: Equal(g11,g7)
    c: Equal(g7,g10)
    c: Distance(g10) = 3.5
    c: Coincident(g1,g4)
    c: Coincident(g2,g3)
    c: DistanceY(g0) = 30
    c: DistanceX(g0) = 17.5
FEATURE [Sketcher::SketchObject] Sketch009
  FullyConstrained = true
  MapMode = 5
  Placement = pos=(0,0,60) rot=(0,0,1;0rad)
  Support = -> [DatumPlane001]
  expr: Constraints[13] = planB#<<data>>.L_thickness + 0.4 * 2
  expr: Constraints[14] = planB#<<data>>.L_size + 0.4 * 2
  expr: Constraints[15] = planB#<<data>>.L_size - planB#<<data>>.L_thickness
  sketch-geometry (6):
    g0: LineSegment StartX=6 StartY=78.6 StartZ=0 EndX=6 EndY=56.7 EndZ=0
    g1: LineSegment StartX=6 StartY=56.7 StartZ=0 EndX=16.3 EndY=56.7 EndZ=0
    g2: LineSegment StartX=16.3 StartY=56.7 StartZ=0 EndX=16.3 EndY=70.7 EndZ=0
    g3: LineSegment StartX=16.3 StartY=70.7 StartZ=0 EndX=8.4 EndY=70.7 EndZ=0
    g4: LineSegment StartX=8.4 StartY=70.7 StartZ=0 EndX=8.4 EndY=78.6 EndZ=0
    g5: LineSegment StartX=8.4 StartY=78.6 StartZ=0 EndX=6 EndY=78.6 EndZ=0
  constraints (18):
    c: Vertical(g0)
    c: Coincident(g0,g1)
    c: Horizontal(g1)
    c: Coincident(g1,g2)
    c: Vertical(g2)
    c: Coincident(g2,g3)
    c: Horizontal(g3)
    c: Coincident(g3,g4)
    c: Vertical(g4)
    c: Coincident(g4,g5)
    c: Coincident(g5,g0)
    c: Horizontal(g5)
    c: DistanceX(g0) = 6
    c: Distance(g5) = 2.4
    c: Distance(g1) = 10.3
    c: Distance(g4) = 7.9
    c: Distance(g2) = 14
    c: DistanceY(g0) = 78.6
FEATURE [PartDesign::Pocket] Pocket008  label="L hole"
  BaseFeature = -> Pocket001
  Direction = (0,0,-1)
  Length = 56
  Length2 = 5
  Profile = -> Sketch009
  ReferenceAxis = -> Sketch009 [N_Axis]
  Type = 0
FEATURE [PartDesign::Pocket] Pocket002  label="hollow for psu"
  BaseFeature = -> Pocket008
  Direction = (0,0,-1)
  Length = 44
  Length2 = 5
  Profile = -> Sketch003
  ReferenceAxis = -> Sketch003 [N_Axis]
  Type = 0
  expr: Length = planB#<<data>>.speaker_w - 16
FEATURE [PartDesign::Pocket] Pocket003  label="bottom screwholes"
  BaseFeature = -> Pocket002
  Direction = (0,1,2e-16)
  Length = 34
  Length2 = 5
  Profile = -> Sketch004
  ReferenceAxis = -> Sketch004 [N_Axis]
  Type = 0
FEATURE [PartDesign::Pocket] Pocket004  label="side screwholes"
  BaseFeature = -> Pocket003
  Direction = (-1,1e-16,-1e-16)
  Length = 9
  Length2 = 5
  Profile = -> Sketch005
  ReferenceAxis = -> Sketch005 [N_Axis]
  Reversed = true
  Type = 1
FEATURE [PartDesign::Pocket] Pocket005
  BaseFeature = -> Pocket004
  Direction = (-1,1e-16,-1e-16)
  Length = 10
  Length2 = 5
  Profile = -> Sketch006
  ReferenceAxis = -> Sketch006 [N_Axis]
  Reversed = true
  Type = 0
FEATURE [PartDesign::Pocket] Pocket006  label="power socket outline"
  BaseFeature = -> Pocket005
  Direction = (-1,2e-16,-3e-16)
  Length = 4
  Length2 = 5
  Profile = -> Sketch007
  ReferenceAxis = -> Sketch007 [N_Axis]
  Reversed = true
  Type = 0
FEATURE [PartDesign::Pocket] Pocket007  label="power socket holes"
  BaseFeature = -> Pocket006
  Direction = (-1,2e-16,-3e-16)
  Length = 36
  Length2 = 5
  Profile = -> Sketch008
  ReferenceAxis = -> Sketch008 [N_Axis]
  Reversed = true
  Type = 0
FEATURE [Sketcher::SketchObject] Sketch010
  FullyConstrained = true
  MapMode = 5
  Support = -> [XY_Plane]
  sketch-geometry (4):
    g0: LineSegment StartX=7 StartY=77.6 StartZ=0 EndX=15.3 EndY=77.6 EndZ=0
    g1: LineSegment StartX=15.3 StartY=77.6 StartZ=0 EndX=15.3 EndY=57.7 EndZ=0
    g2: LineSegment StartX=15.3 StartY=57.7 StartZ=0 EndX=7 EndY=57.7 EndZ=0
    g3: LineSegment StartX=7 StartY=57.7 StartZ=0 EndX=7 EndY=77.6 EndZ=0
  constraints (12):
    c: Coincident(g0,g1)
    c: Coincident(g1,g2)
    c: Coincident(g2,g3)
    c: Coincident(g3,g0)
    c: Horizontal(g0)
    c: Horizontal(g2)
    c: Vertical(g1)
    c: Vertical(g3)
    c: DistanceX(g0) = 7
    c: DistanceX(g1) = 15.3
    c: DistanceY(g0) = 77.6
    c: DistanceY(g1) = 57.7
FEATURE [PartDesign::Pocket] Pocket009
  BaseFeature = -> Pocket007
  Direction = (0,0,-1)
  Length = 5
  Length2 = 5
  Profile = -> Sketch010
  ReferenceAxis = -> Sketch010 [N_Axis]
  Reversed = true
  Type = 0
FEATURE [Sketcher::SketchObject] Sketch011
  FullyConstrained = true
  MapMode = 5
  Support = -> [XY_Plane]
  expr: Constraints[8] = planB#<<data>>.rme_w + 2
  expr: Constraints[9] = planB#<<data>>.rme_h + 2
  sketch-geometry (4):
    g0: LineSegment StartX=152.6 StartY=37 StartZ=0 EndX=22.6 EndY=37 EndZ=0
    g1: LineSegment StartX=22.6 StartY=37 StartZ=0 EndX=22.6 EndY=61 EndZ=0
    g2: LineSegment StartX=22.6 StartY=61 StartZ=0 EndX=152.6 EndY=61 EndZ=0
    g3: LineSegment StartX=152.6 StartY=61 StartZ=0 EndX=152.6 EndY=37 EndZ=0
  constraints (12):
    c: Coincident(g0,g1)
    c: Coincident(g1,g2)
    c: Coincident(g2,g3)
    c: Coincident(g3,g0)
    c: Horizontal(g0)
    c: Horizontal(g2)
    c: Vertical(g1)
    c: Vertical(g3)
    c: DistanceX(g2,g2) = 130
    c: DistanceY(g1,g1) = 24
    c: DistanceX(g0) = 152.6
    c: DistanceY(g0) = 37
FEATURE [PartDesign::Pocket] Pocket010
  BaseFeature = -> Pocket009
  Direction = (0,0,-1)
  Length = 75
  Length2 = 5
  Profile = -> Sketch011
  ReferenceAxis = -> Sketch011 [N_Axis]
  Reversed = true
  Type = 0
FEATURE [Sketcher::SketchObject] Sketch012
  FullyConstrained = false
  MapMode = 5
  Placement = pos=(0,0,5) rot=(0,0,1;0rad)
  Support = -> [DatumPlane]
  sketch-geometry (8):
    g0: LineSegment StartX=14.25 StartY=52.75 StartZ=0 EndX=21.75 EndY=52.75 EndZ=0
    g1: LineSegment StartX=21.75 StartY=52.75 StartZ=0 EndX=21.75 EndY=45.25 EndZ=0
    g2: LineSegment StartX=21.75 StartY=45.25 StartZ=0 EndX=14.25 EndY=45.25 EndZ=0
    g3: LineSegment StartX=14.25 StartY=45.25 StartZ=0 EndX=14.25 EndY=52.75 EndZ=0
    g4: GeomPoint X=18 Y=49 Z=0
    g5: LineSegment StartX=21.75 StartY=52.75 StartZ=0 EndX=29.454 EndY=52.75 EndZ=0
    g6: LineSegment StartX=29.454 StartY=52.75 StartZ=0 EndX=29.454 EndY=45.25 EndZ=0
    g7: LineSegment StartX=29.454 StartY=45.25 StartZ=0 EndX=21.75 EndY=45.25 EndZ=0
  constraints (20):
    c: Coincident(g0,g1)
    c: Coincident(g1,g2)
    c: Coincident(g2,g3)
    c: Coincident(g3,g0)
    c: Horizontal(g0)
    c: Horizontal(g2)
    c: Vertical(g1)
    c: Vertical(g3)
    c: Symmetric(g0,g1,g4)
    c: DistanceX(g4) = 18
    c: DistanceY(g4) = 49
    c: DistanceX(g2,g2) = 7.5
    c: DistanceY(g3,g3) = 7.5
    c: Horizontal(g5)
    c: Coincident(g5,g6)
    c: Vertical(g6)
    c: Coincident(g6,g7)
    c: Coincident(g7,g2)
    c: Horizontal(g7)
    c: Coincident(g5,g0)
FEATURE [PartDesign::Pocket] Pocket011
  BaseFeature = -> Pocket010
  Direction = (0,0,-1)
  Length = 4
  Length2 = 5
  Profile = -> Sketch012
  ReferenceAxis = -> Sketch012 [N_Axis]
  Reversed = true
  Type = 0
FEATURE [PartDesign::Chamfer] Chamfer
  Angle = 45
  Base = -> Pocket011 [Edge25,Edge28,Edge27,Edge26]
  BaseFeature = -> Pocket011
  ChamferType = 1
  FlipDirection = false
  Size = 1
  Size2 = 3.99
  SupportTransform = false
  UseAllEdges = false
FEATURE [PartDesign::Body] Body
  Group = -> [Sketch,Pad,DatumPlane,Sketch001,Pocket,DatumPlane001,Sketch002,Pocket001,Pocket008,Sketch003,Pocket002,Sketch004,Pocket003,DatumPlane002,Sketch005,Pocket004,Sketch006,Pocket005,Sketch007,Pocket006,Sketch008,Pocket007,Sketch009,Sketch010,Pocket009,Sketch011,Pocket010,Sketch012,Pocket011,Chamfer]
  Origin = -> Origin
  Tip = -> Chamfer
FEATURE [App::Part] speakerbox
  Group = -> [LCS_0,Body]
  Origin = -> Origin001
